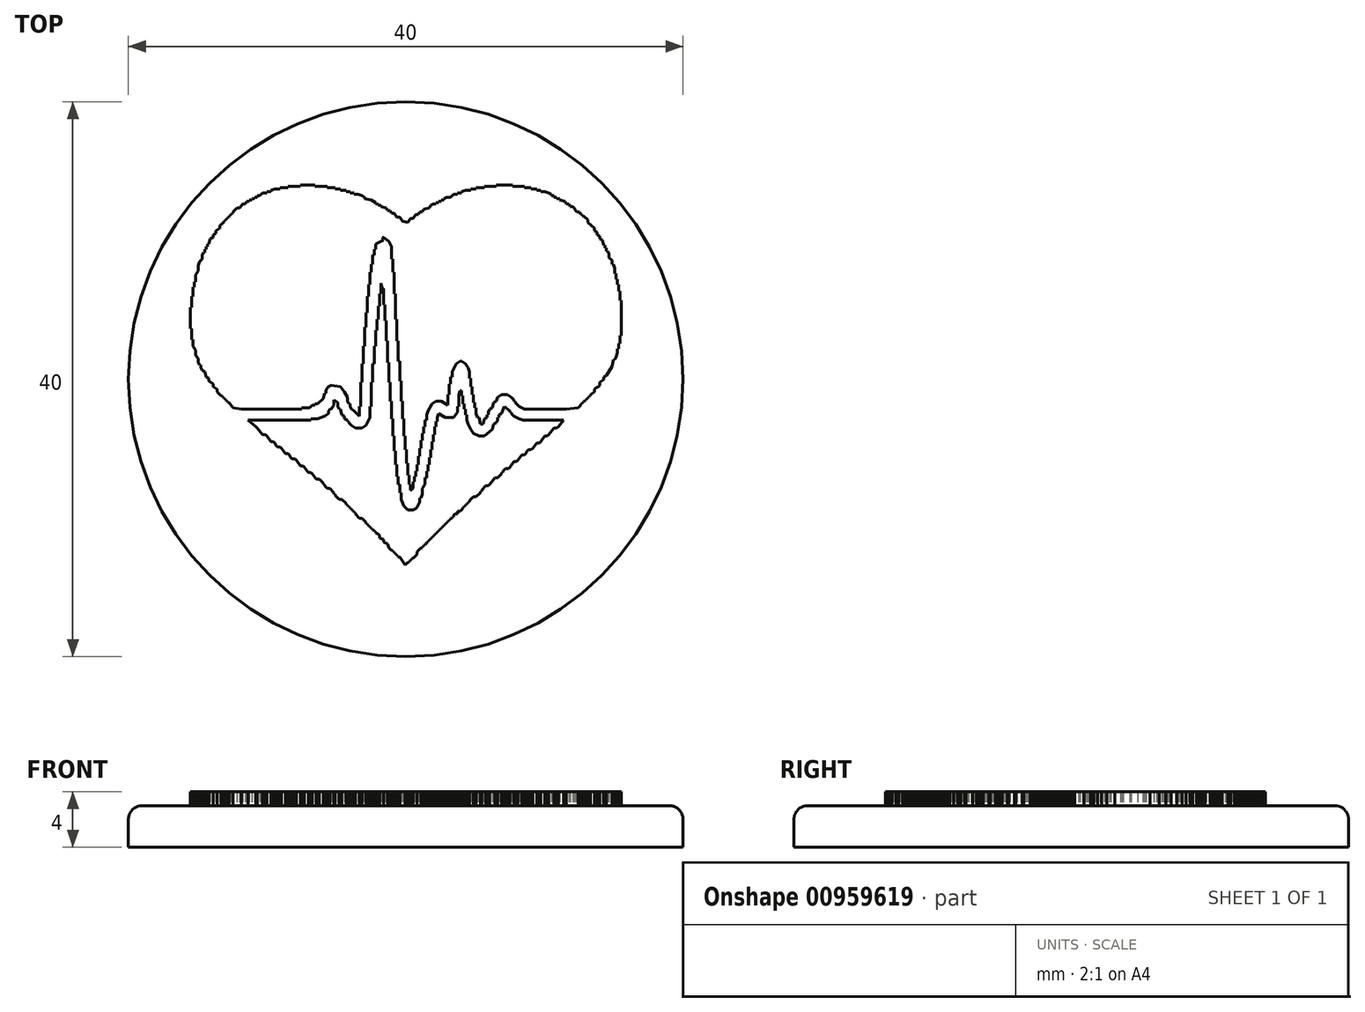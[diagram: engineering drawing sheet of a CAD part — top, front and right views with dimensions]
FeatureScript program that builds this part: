
annotation { "Feature Type Name" : "Feature", "Feature Type Description" : "" }
export const myFeature = defineFeature(function(context is Context, id is Id, definition is map)
    precondition{}
    {
        {
            var Q0;
            Q0=qCreatedBy(makeId("Front.planeOp"),FACE);
            var sketch = newSketch(context, id + "F0", { "sketchPlane" : qUnion([Q0])});
            skLineSegment(sketch, "E0.bottom", {"start": v(-20, 0) * mm, "end": v(0, 0) * mm});
            skLineSegment(sketch, "E0.top", {"start": v(-20, 3) * mm, "end": v(0, 3) * mm});
            skLineSegment(sketch, "E0.left", {"start": v(-20, 0) * mm, "end": v(-20, 3) * mm});
            skLineSegment(sketch, "E0.right", {"start": v(0, 0) * mm, "end": v(0, 3) * mm});
            skSolve(sketch);
        }
        {
            var Q0;
            Q0=qSketchRegion(id+"F0",true);
            var Q1;
            Q1=sQuery(id+"F0.wireOp",EDGE,"E0.right");
            revolve(context, id + "F1", {"surfaceOperationType" : NewSurfaceOperationType.NEW, "entities" : qUnion([Q0]), "axis" : qUnion([Q1]), "revolveType" : RevolveType.FULL});
        }
        {
            var Q0;
            Q0=qCreatedBy(makeId("Top.planeOp"),FACE);
            cPlane(context, id + "F2", {"entities" : qUnion([Q0]), "cplaneType" : CPlaneType.OFFSET, "offset" : 3 * mm, "width" : 150 * mm, "height" : 150 * mm});
        }
        {
            var Q0;
            Q0=qCreatedBy(id+"F2.planeOp",FACE);
            var sketch = newSketch(context, id + "F3", { "sketchPlane" : qUnion([Q0])});
            skLineSegment(sketch, "E1", {"start": v(-7.6, 14) * mm, "end": v(-7.6, 13.9) * mm});
            skLineSegment(sketch, "E2", {"start": v(-7.6, 13.9) * mm, "end": v(-7.9, 13.9) * mm});
            skLineSegment(sketch, "E3", {"start": v(-7.9, 13.9) * mm, "end": v(-8.18, 13.9) * mm});
            skLineSegment(sketch, "E4", {"start": v(-8.18, 13.9) * mm, "end": v(-8.47, 13.9) * mm});
            skLineSegment(sketch, "E5", {"start": v(-8.47, 13.9) * mm, "end": v(-8.47, 13.8) * mm});
            skLineSegment(sketch, "E6", {"start": v(-8.47, 13.8) * mm, "end": v(-9.06, 13.8) * mm});
            skLineSegment(sketch, "E7", {"start": v(-9.06, 13.8) * mm, "end": v(-9.06, 13.7) * mm});
            skLineSegment(sketch, "E8", {"start": v(-9.06, 13.7) * mm, "end": v(-9.44, 13.7) * mm});
            skLineSegment(sketch, "E9", {"start": v(-9.44, 13.7) * mm, "end": v(-9.73, 13.61) * mm});
            skLineSegment(sketch, "E10", {"start": v(-9.73, 13.61) * mm, "end": v(-9.73, 13.52) * mm});
            skLineSegment(sketch, "E11", {"start": v(-9.73, 13.52) * mm, "end": v(-10.02, 13.52) * mm});
            skLineSegment(sketch, "E12", {"start": v(-10.02, 13.52) * mm, "end": v(-10.02, 13.42) * mm});
            skLineSegment(sketch, "E13", {"start": v(-10.02, 13.42) * mm, "end": v(-10.31, 13.42) * mm});
            skLineSegment(sketch, "E14", {"start": v(-10.31, 13.42) * mm, "end": v(-10.5, 13.23) * mm});
            skLineSegment(sketch, "E15", {"start": v(-10.5, 13.23) * mm, "end": v(-10.7, 13.23) * mm});
            skLineSegment(sketch, "E16", {"start": v(-10.7, 13.23) * mm, "end": v(-10.7, 13.13) * mm});
            skLineSegment(sketch, "E17", {"start": v(-10.7, 13.13) * mm, "end": v(-10.9, 13.13) * mm});
            skLineSegment(sketch, "E18", {"start": v(-10.9, 13.13) * mm, "end": v(-10.9, 13.03) * mm});
            skLineSegment(sketch, "E19", {"start": v(-10.9, 13.03) * mm, "end": v(-11.09, 13.03) * mm});
            skLineSegment(sketch, "E20", {"start": v(-11.09, 13.03) * mm, "end": v(-11.09, 12.93) * mm});
            skLineSegment(sketch, "E21", {"start": v(-11.09, 12.93) * mm, "end": v(-11.28, 12.93) * mm});
            skLineSegment(sketch, "E22", {"start": v(-11.28, 12.93) * mm, "end": v(-11.28, 12.84) * mm});
            skLineSegment(sketch, "E23", {"start": v(-11.28, 12.84) * mm, "end": v(-11.48, 12.84) * mm});
            skLineSegment(sketch, "E24", {"start": v(-11.48, 12.84) * mm, "end": v(-11.57, 12.64) * mm});
            skLineSegment(sketch, "E25", {"start": v(-11.57, 12.64) * mm, "end": v(-11.77, 12.64) * mm});
            skLineSegment(sketch, "E26", {"start": v(-11.77, 12.64) * mm, "end": v(-11.96, 12.35) * mm});
            skLineSegment(sketch, "E27", {"start": v(-11.96, 12.35) * mm, "end": v(-12.15, 12.35) * mm});
            skLineSegment(sketch, "E28", {"start": v(-12.15, 12.35) * mm, "end": v(-12.25, 12.26) * mm});
            skLineSegment(sketch, "E29", {"start": v(-12.25, 12.26) * mm, "end": v(-12.45, 12.06) * mm});
            skLineSegment(sketch, "E30", {"start": v(-12.45, 12.06) * mm, "end": v(-12.45, 11.97) * mm});
            skLineSegment(sketch, "E31", {"start": v(-12.45, 11.97) * mm, "end": v(-12.54, 11.97) * mm});
            skLineSegment(sketch, "E32", {"start": v(-12.54, 11.97) * mm, "end": v(-12.54, 11.87) * mm});
            skLineSegment(sketch, "E33", {"start": v(-12.54, 11.87) * mm, "end": v(-12.64, 11.87) * mm});
            skLineSegment(sketch, "E34", {"start": v(-12.64, 11.87) * mm, "end": v(-12.64, 11.77) * mm});
            skLineSegment(sketch, "E35", {"start": v(-12.64, 11.77) * mm, "end": v(-12.74, 11.77) * mm});
            skLineSegment(sketch, "E36", {"start": v(-12.74, 11.77) * mm, "end": v(-12.74, 11.68) * mm});
            skLineSegment(sketch, "E37", {"start": v(-12.74, 11.68) * mm, "end": v(-12.83, 11.68) * mm});
            skLineSegment(sketch, "E38", {"start": v(-12.83, 11.68) * mm, "end": v(-12.83, 11.58) * mm});
            skLineSegment(sketch, "E39", {"start": v(-12.83, 11.58) * mm, "end": v(-12.93, 11.58) * mm});
            skLineSegment(sketch, "E40", {"start": v(-12.93, 11.58) * mm, "end": v(-12.93, 11.48) * mm});
            skLineSegment(sketch, "E41", {"start": v(-12.93, 11.48) * mm, "end": v(-13.03, 11.48) * mm});
            skLineSegment(sketch, "E42", {"start": v(-13.03, 11.48) * mm, "end": v(-13.03, 11.38) * mm});
            skLineSegment(sketch, "E43", {"start": v(-13.03, 11.38) * mm, "end": v(-13.12, 11.38) * mm});
            skLineSegment(sketch, "E44", {"start": v(-13.12, 11.38) * mm, "end": v(-13.12, 11.29) * mm});
            skLineSegment(sketch, "E45", {"start": v(-13.12, 11.29) * mm, "end": v(-13.41, 11.1) * mm});
            skLineSegment(sketch, "E46", {"start": v(-13.41, 11.1) * mm, "end": v(-13.41, 10.9) * mm});
            skLineSegment(sketch, "E47", {"start": v(-13.41, 10.9) * mm, "end": v(-13.7, 10.7) * mm});
            skLineSegment(sketch, "E48", {"start": v(-13.7, 10.7) * mm, "end": v(-13.7, 10.51) * mm});
            skLineSegment(sketch, "E49", {"start": v(-13.7, 10.51) * mm, "end": v(-13.9, 10.42) * mm});
            skLineSegment(sketch, "E50", {"start": v(-13.9, 10.42) * mm, "end": v(-13.9, 10.22) * mm});
            skLineSegment(sketch, "E51", {"start": v(-13.9, 10.22) * mm, "end": v(-14.1, 10.13) * mm});
            skLineSegment(sketch, "E52", {"start": v(-14.1, 10.13) * mm, "end": v(-14.19, 9.74) * mm});
            skLineSegment(sketch, "E53", {"start": v(-14.19, 9.74) * mm, "end": v(-14.29, 9.74) * mm});
            skLineSegment(sketch, "E54", {"start": v(-14.29, 9.74) * mm, "end": v(-14.29, 9.54) * mm});
            skLineSegment(sketch, "E55", {"start": v(-14.29, 9.54) * mm, "end": v(-14.38, 9.54) * mm});
            skLineSegment(sketch, "E56", {"start": v(-14.38, 9.54) * mm, "end": v(-14.38, 9.35) * mm});
            skLineSegment(sketch, "E57", {"start": v(-14.38, 9.35) * mm, "end": v(-14.48, 9.35) * mm});
            skLineSegment(sketch, "E58", {"start": v(-14.48, 9.35) * mm, "end": v(-14.48, 9.16) * mm});
            skLineSegment(sketch, "E59", {"start": v(-14.48, 9.16) * mm, "end": v(-14.58, 9.16) * mm});
            skLineSegment(sketch, "E60", {"start": v(-14.58, 9.16) * mm, "end": v(-14.67, 8.96) * mm});
            skLineSegment(sketch, "E61", {"start": v(-14.67, 8.96) * mm, "end": v(-14.67, 8.67) * mm});
            skLineSegment(sketch, "E62", {"start": v(-14.67, 8.67) * mm, "end": v(-14.87, 8.48) * mm});
            skLineSegment(sketch, "E63", {"start": v(-14.87, 8.48) * mm, "end": v(-14.96, 8.19) * mm});
            skLineSegment(sketch, "E64", {"start": v(-14.96, 8.19) * mm, "end": v(-14.96, 7.8) * mm});
            skLineSegment(sketch, "E65", {"start": v(-14.96, 7.8) * mm, "end": v(-15.16, 7.51) * mm});
            skLineSegment(sketch, "E66", {"start": v(-15.16, 7.51) * mm, "end": v(-15.16, 7.03) * mm});
            skLineSegment(sketch, "E67", {"start": v(-15.16, 7.03) * mm, "end": v(-15.25, 7.03) * mm});
            skLineSegment(sketch, "E68", {"start": v(-15.25, 7.03) * mm, "end": v(-15.25, 6.64) * mm});
            skLineSegment(sketch, "E69", {"start": v(-15.25, 6.64) * mm, "end": v(-15.35, 6.64) * mm});
            skLineSegment(sketch, "E70", {"start": v(-15.35, 6.64) * mm, "end": v(-15.35, 5.96) * mm});
            skLineSegment(sketch, "E71", {"start": v(-15.35, 5.96) * mm, "end": v(-15.45, 5.96) * mm});
            skLineSegment(sketch, "E72", {"start": v(-15.45, 5.96) * mm, "end": v(-15.45, 5.19) * mm});
            skLineSegment(sketch, "E73", {"start": v(-15.45, 5.19) * mm, "end": v(-15.54, 5.19) * mm});
            skLineSegment(sketch, "E74", {"start": v(-15.54, 5.19) * mm, "end": v(-15.54, 4.9) * mm});
            skLineSegment(sketch, "E75", {"start": v(-15.54, 4.9) * mm, "end": v(-15.54, 4.5) * mm});
            skLineSegment(sketch, "E76", {"start": v(-15.54, 4.5) * mm, "end": v(-15.54, 4.41) * mm});
            skLineSegment(sketch, "E77", {"start": v(-15.54, 4.41) * mm, "end": v(-15.54, 4.31) * mm});
            skLineSegment(sketch, "E78", {"start": v(-15.54, 4.31) * mm, "end": v(-15.54, 4.22) * mm});
            skLineSegment(sketch, "E79", {"start": v(-15.54, 4.22) * mm, "end": v(-15.54, 3.64) * mm});
            skLineSegment(sketch, "E80", {"start": v(-15.54, 3.64) * mm, "end": v(-15.45, 3.64) * mm});
            skLineSegment(sketch, "E81", {"start": v(-15.45, 3.64) * mm, "end": v(-15.45, 2.86) * mm});
            skLineSegment(sketch, "E82", {"start": v(-15.45, 2.86) * mm, "end": v(-15.35, 2.86) * mm});
            skLineSegment(sketch, "E83", {"start": v(-15.35, 2.86) * mm, "end": v(-15.35, 2.38) * mm});
            skLineSegment(sketch, "E84", {"start": v(-15.35, 2.38) * mm, "end": v(-15.16, 2.09) * mm});
            skLineSegment(sketch, "E85", {"start": v(-15.16, 2.09) * mm, "end": v(-15.16, 1.7) * mm});
            skLineSegment(sketch, "E86", {"start": v(-15.16, 1.7) * mm, "end": v(-14.96, 1.5) * mm});
            skLineSegment(sketch, "E87", {"start": v(-14.96, 1.5) * mm, "end": v(-14.96, 1.22) * mm});
            skLineSegment(sketch, "E88", {"start": v(-14.96, 1.22) * mm, "end": v(-14.87, 1.02) * mm});
            skLineSegment(sketch, "E89", {"start": v(-14.87, 1.02) * mm, "end": v(-14.77, 1.02) * mm});
            skLineSegment(sketch, "E90", {"start": v(-14.77, 1.02) * mm, "end": v(-14.77, 0.83) * mm});
            skLineSegment(sketch, "E91", {"start": v(-14.77, 0.83) * mm, "end": v(-14.67, 0.63) * mm});
            skLineSegment(sketch, "E92", {"start": v(-14.67, 0.63) * mm, "end": v(-14.48, 0.54) * mm});
            skLineSegment(sketch, "E93", {"start": v(-14.48, 0.54) * mm, "end": v(-14.38, 0.15) * mm});
            skLineSegment(sketch, "E94", {"start": v(-14.38, 0.15) * mm, "end": v(-14.19, 0.05) * mm});
            skLineSegment(sketch, "E95", {"start": v(-14.19, 0.05) * mm, "end": v(-14.19, -0.14) * mm});
            skLineSegment(sketch, "E96", {"start": v(-14.19, -0.14) * mm, "end": v(-13.9, -0.33) * mm});
            skLineSegment(sketch, "E97", {"start": v(-13.9, -0.33) * mm, "end": v(-13.9, -0.53) * mm});
            skLineSegment(sketch, "E98", {"start": v(-13.9, -0.53) * mm, "end": v(-13.6, -0.72) * mm});
            skLineSegment(sketch, "E99", {"start": v(-13.6, -0.72) * mm, "end": v(-13.6, -0.92) * mm});
            skLineSegment(sketch, "E100", {"start": v(-13.6, -0.92) * mm, "end": v(-13.51, -1.01) * mm});
            skLineSegment(sketch, "E101", {"start": v(-13.51, -1.01) * mm, "end": v(-13.32, -1.2) * mm});
            skLineSegment(sketch, "E102", {"start": v(-13.32, -1.2) * mm, "end": v(-13.22, -1.2) * mm});
            skLineSegment(sketch, "E103", {"start": v(-13.22, -1.2) * mm, "end": v(-13.22, -1.3) * mm});
            skLineSegment(sketch, "E104", {"start": v(-13.22, -1.3) * mm, "end": v(-13.12, -1.3) * mm});
            skLineSegment(sketch, "E105", {"start": v(-13.12, -1.3) * mm, "end": v(-13.12, -1.4) * mm});
            skLineSegment(sketch, "E106", {"start": v(-13.12, -1.4) * mm, "end": v(-13.03, -1.4) * mm});
            skLineSegment(sketch, "E107", {"start": v(-13.03, -1.4) * mm, "end": v(-13.03, -1.5) * mm});
            skLineSegment(sketch, "E108", {"start": v(-13.03, -1.5) * mm, "end": v(-12.93, -1.5) * mm});
            skLineSegment(sketch, "E109", {"start": v(-12.93, -1.5) * mm, "end": v(-12.93, -1.6) * mm});
            skLineSegment(sketch, "E110", {"start": v(-12.93, -1.6) * mm, "end": v(-12.83, -1.6) * mm});
            skLineSegment(sketch, "E111", {"start": v(-12.83, -1.6) * mm, "end": v(-12.83, -1.7) * mm});
            skLineSegment(sketch, "E112", {"start": v(-12.83, -1.7) * mm, "end": v(-12.74, -1.7) * mm});
            skLineSegment(sketch, "E113", {"start": v(-12.74, -1.7) * mm, "end": v(-12.45, -2.08) * mm});
            skLineSegment(sketch, "E114", {"start": v(-12.45, -2.08) * mm, "end": v(-12.83, -2.08) * mm});
            skLineSegment(sketch, "E115", {"start": v(-12.83, -2.08) * mm, "end": v(-12.93, -2.08) * mm});
            skLineSegment(sketch, "E116", {"start": v(-12.93, -2.08) * mm, "end": v(-13.03, -2.08) * mm});
            skLineSegment(sketch, "E117", {"start": v(-13.03, -2.08) * mm, "end": v(-13.12, -2.08) * mm});
            skLineSegment(sketch, "E118", {"start": v(-13.12, -2.08) * mm, "end": v(-13.22, -2.08) * mm});
            skLineSegment(sketch, "E119", {"start": v(-13.22, -2.08) * mm, "end": v(-13.32, -2.08) * mm});
            skLineSegment(sketch, "E120", {"start": v(-13.32, -2.08) * mm, "end": v(-13.41, -2.08) * mm});
            skLineSegment(sketch, "E121", {"start": v(-13.41, -2.08) * mm, "end": v(-13.51, -2.08) * mm});
            skLineSegment(sketch, "E122", {"start": v(-13.51, -2.08) * mm, "end": v(-13.6, -2.08) * mm});
            skLineSegment(sketch, "E123", {"start": v(-13.6, -2.08) * mm, "end": v(-13.7, -2.08) * mm});
            skLineSegment(sketch, "E124", {"start": v(-13.7, -2.08) * mm, "end": v(-13.8, -2.08) * mm});
            skLineSegment(sketch, "E125", {"start": v(-13.8, -2.08) * mm, "end": v(-13.9, -2.08) * mm});
            skLineSegment(sketch, "E126", {"start": v(-13.9, -2.08) * mm, "end": v(-14, -2.08) * mm});
            skLineSegment(sketch, "E127", {"start": v(-14, -2.08) * mm, "end": v(-14.1, -2.08) * mm});
            skLineSegment(sketch, "E128", {"start": v(-14.1, -2.08) * mm, "end": v(-14.19, -2.08) * mm});
            skLineSegment(sketch, "E129", {"start": v(-14.19, -2.08) * mm, "end": v(-14.29, -2.08) * mm});
            skLineSegment(sketch, "E130", {"start": v(-14.29, -2.08) * mm, "end": v(-14.38, -2.08) * mm});
            skLineSegment(sketch, "E131", {"start": v(-14.38, -2.08) * mm, "end": v(-14.48, -2.08) * mm});
            skLineSegment(sketch, "E132", {"start": v(-14.48, -2.08) * mm, "end": v(-14.58, -2.08) * mm});
            skLineSegment(sketch, "E133", {"start": v(-14.58, -2.08) * mm, "end": v(-14.67, -2.08) * mm});
            skLineSegment(sketch, "E134", {"start": v(-14.67, -2.08) * mm, "end": v(-14.77, -2.08) * mm});
            skLineSegment(sketch, "E135", {"start": v(-14.77, -2.08) * mm, "end": v(-14.87, -2.08) * mm});
            skLineSegment(sketch, "E136", {"start": v(-14.87, -2.08) * mm, "end": v(-14.96, -2.08) * mm});
            skLineSegment(sketch, "E137", {"start": v(-14.96, -2.08) * mm, "end": v(-15.06, -2.08) * mm});
            skLineSegment(sketch, "E138", {"start": v(-15.06, -2.08) * mm, "end": v(-15.16, -2.08) * mm});
            skLineSegment(sketch, "E139", {"start": v(-15.16, -2.08) * mm, "end": v(-15.25, -2.08) * mm});
            skLineSegment(sketch, "E140", {"start": v(-15.25, -2.08) * mm, "end": v(-15.35, -2.08) * mm});
            skLineSegment(sketch, "E141", {"start": v(-15.35, -2.08) * mm, "end": v(-15.45, -2.08) * mm});
            skLineSegment(sketch, "E142", {"start": v(-15.45, -2.08) * mm, "end": v(-15.54, -2.08) * mm});
            skLineSegment(sketch, "E143", {"start": v(-15.54, -2.08) * mm, "end": v(-15.64, -2.08) * mm});
            skLineSegment(sketch, "E144", {"start": v(-15.64, -2.08) * mm, "end": v(-15.74, -2.08) * mm});
            skLineSegment(sketch, "E145", {"start": v(-15.74, -2.08) * mm, "end": v(-15.84, -2.08) * mm});
            skLineSegment(sketch, "E146", {"start": v(-15.84, -2.08) * mm, "end": v(-15.93, -2.08) * mm});
            skLineSegment(sketch, "E147", {"start": v(-15.93, -2.08) * mm, "end": v(-16.03, -2.08) * mm});
            skLineSegment(sketch, "E148", {"start": v(-16.03, -2.08) * mm, "end": v(-16.13, -2.08) * mm});
            skLineSegment(sketch, "E149", {"start": v(-16.13, -2.08) * mm, "end": v(-16.22, -2.08) * mm});
            skLineSegment(sketch, "E150", {"start": v(-16.22, -2.08) * mm, "end": v(-16.32, -2.08) * mm});
            skLineSegment(sketch, "E151", {"start": v(-16.32, -2.08) * mm, "end": v(-16.42, -2.08) * mm});
            skLineSegment(sketch, "E152", {"start": v(-16.42, -2.08) * mm, "end": v(-16.51, -2.08) * mm});
            skLineSegment(sketch, "E153", {"start": v(-16.51, -2.08) * mm, "end": v(-16.61, -2.08) * mm});
            skLineSegment(sketch, "E154", {"start": v(-16.61, -2.08) * mm, "end": v(-16.7, -2.08) * mm});
            skLineSegment(sketch, "E155", {"start": v(-16.7, -2.08) * mm, "end": v(-16.8, -2.08) * mm});
            skLineSegment(sketch, "E156", {"start": v(-16.8, -2.08) * mm, "end": v(-16.9, -2.08) * mm});
            skLineSegment(sketch, "E157", {"start": v(-16.9, -2.08) * mm, "end": v(-17, -2.08) * mm});
            skLineSegment(sketch, "E158", {"start": v(-17, -2.08) * mm, "end": v(-17.1, -2.08) * mm});
            skLineSegment(sketch, "E159", {"start": v(-17.1, -2.08) * mm, "end": v(-17.2, -2.08) * mm});
            skLineSegment(sketch, "E160", {"start": v(-17.2, -2.08) * mm, "end": v(-17.29, -2.08) * mm});
            skLineSegment(sketch, "E161", {"start": v(-17.29, -2.08) * mm, "end": v(-17.38, -2.08) * mm});
            skLineSegment(sketch, "E162", {"start": v(-17.38, -2.08) * mm, "end": v(-17.48, -2.08) * mm});
            skLineSegment(sketch, "E163", {"start": v(-17.48, -2.08) * mm, "end": v(-17.58, -2.08) * mm});
            skLineSegment(sketch, "E164", {"start": v(-17.58, -2.08) * mm, "end": v(-17.68, -2.08) * mm});
            skLineSegment(sketch, "E165", {"start": v(-17.68, -2.08) * mm, "end": v(-17.77, -2.08) * mm});
            skLineSegment(sketch, "E166", {"start": v(-17.77, -2.08) * mm, "end": v(-17.87, -2.08) * mm});
            skLineSegment(sketch, "E167", {"start": v(-17.87, -2.08) * mm, "end": v(-17.97, -2.08) * mm});
            skLineSegment(sketch, "E168", {"start": v(-17.97, -2.08) * mm, "end": v(-18.06, -2.08) * mm});
            skLineSegment(sketch, "E169", {"start": v(-18.06, -2.08) * mm, "end": v(-18.16, -2.08) * mm});
            skLineSegment(sketch, "E170", {"start": v(-18.16, -2.08) * mm, "end": v(-18.26, -2.08) * mm});
            skLineSegment(sketch, "E171", {"start": v(-18.26, -2.08) * mm, "end": v(-18.35, -2.08) * mm});
            skLineSegment(sketch, "E172", {"start": v(-18.35, -2.08) * mm, "end": v(-18.45, -2.08) * mm});
            skLineSegment(sketch, "E173", {"start": v(-18.45, -2.08) * mm, "end": v(-18.55, -2.08) * mm});
            skLineSegment(sketch, "E174", {"start": v(-18.55, -2.08) * mm, "end": v(-18.64, -2.08) * mm});
            skLineSegment(sketch, "E175", {"start": v(-18.64, -2.08) * mm, "end": v(-18.74, -2.08) * mm});
            skLineSegment(sketch, "E176", {"start": v(-18.74, -2.08) * mm, "end": v(-18.84, -2.08) * mm});
            skLineSegment(sketch, "E177", {"start": v(-18.84, -2.08) * mm, "end": v(-18.93, -2.08) * mm});
            skLineSegment(sketch, "E178", {"start": v(-18.93, -2.08) * mm, "end": v(-19.03, -2.08) * mm});
            skLineSegment(sketch, "E179", {"start": v(-19.03, -2.08) * mm, "end": v(-19.13, -2.08) * mm});
            skLineSegment(sketch, "E180", {"start": v(-19.13, -2.08) * mm, "end": v(-19.23, -2.08) * mm});
            skLineSegment(sketch, "E181", {"start": v(-19.23, -2.08) * mm, "end": v(-19.32, -2.08) * mm});
            skLineSegment(sketch, "E182", {"start": v(-19.32, -2.08) * mm, "end": v(-19.7, -2.08) * mm});
            skLineSegment(sketch, "E183", {"start": v(-19.7, -2.95) * mm, "end": v(-19.32, -2.95) * mm});
            skLineSegment(sketch, "E184", {"start": v(-19.32, -2.95) * mm, "end": v(-19.23, -2.95) * mm});
            skLineSegment(sketch, "E185", {"start": v(-19.23, -2.95) * mm, "end": v(-19.13, -2.95) * mm});
            skLineSegment(sketch, "E186", {"start": v(-19.13, -2.95) * mm, "end": v(-19.03, -2.95) * mm});
            skLineSegment(sketch, "E187", {"start": v(-19.03, -2.95) * mm, "end": v(-18.93, -2.95) * mm});
            skLineSegment(sketch, "E188", {"start": v(-18.93, -2.95) * mm, "end": v(-18.84, -2.95) * mm});
            skLineSegment(sketch, "E189", {"start": v(-18.84, -2.95) * mm, "end": v(-18.74, -2.95) * mm});
            skLineSegment(sketch, "E190", {"start": v(-18.74, -2.95) * mm, "end": v(-18.64, -2.95) * mm});
            skLineSegment(sketch, "E191", {"start": v(-18.64, -2.95) * mm, "end": v(-18.55, -2.95) * mm});
            skLineSegment(sketch, "E192", {"start": v(-18.55, -2.95) * mm, "end": v(-18.45, -2.95) * mm});
            skLineSegment(sketch, "E193", {"start": v(-18.45, -2.95) * mm, "end": v(-18.35, -2.95) * mm});
            skLineSegment(sketch, "E194", {"start": v(-18.35, -2.95) * mm, "end": v(-18.26, -2.95) * mm});
            skLineSegment(sketch, "E195", {"start": v(-18.26, -2.95) * mm, "end": v(-18.16, -2.95) * mm});
            skLineSegment(sketch, "E196", {"start": v(-18.16, -2.95) * mm, "end": v(-18.06, -2.95) * mm});
            skLineSegment(sketch, "E197", {"start": v(-18.06, -2.95) * mm, "end": v(-17.97, -2.95) * mm});
            skLineSegment(sketch, "E198", {"start": v(-17.97, -2.95) * mm, "end": v(-17.87, -2.95) * mm});
            skLineSegment(sketch, "E199", {"start": v(-17.87, -2.95) * mm, "end": v(-17.77, -2.95) * mm});
            skLineSegment(sketch, "E200", {"start": v(-17.77, -2.95) * mm, "end": v(-17.68, -2.95) * mm});
            skLineSegment(sketch, "E201", {"start": v(-17.68, -2.95) * mm, "end": v(-17.58, -2.95) * mm});
            skLineSegment(sketch, "E202", {"start": v(-17.58, -2.95) * mm, "end": v(-17.48, -2.95) * mm});
            skLineSegment(sketch, "E203", {"start": v(-17.48, -2.95) * mm, "end": v(-17.38, -2.95) * mm});
            skLineSegment(sketch, "E204", {"start": v(-17.38, -2.95) * mm, "end": v(-17.29, -2.95) * mm});
            skLineSegment(sketch, "E205", {"start": v(-17.29, -2.95) * mm, "end": v(-17.2, -2.95) * mm});
            skLineSegment(sketch, "E206", {"start": v(-17.2, -2.95) * mm, "end": v(-17.1, -2.95) * mm});
            skLineSegment(sketch, "E207", {"start": v(-17.1, -2.95) * mm, "end": v(-17, -2.95) * mm});
            skLineSegment(sketch, "E208", {"start": v(-17, -2.95) * mm, "end": v(-16.9, -2.95) * mm});
            skLineSegment(sketch, "E209", {"start": v(-16.9, -2.95) * mm, "end": v(-16.8, -2.95) * mm});
            skLineSegment(sketch, "E210", {"start": v(-16.8, -2.95) * mm, "end": v(-16.7, -2.95) * mm});
            skLineSegment(sketch, "E211", {"start": v(-16.7, -2.95) * mm, "end": v(-16.61, -2.95) * mm});
            skLineSegment(sketch, "E212", {"start": v(-16.61, -2.95) * mm, "end": v(-16.51, -2.95) * mm});
            skLineSegment(sketch, "E213", {"start": v(-16.51, -2.95) * mm, "end": v(-16.42, -2.95) * mm});
            skLineSegment(sketch, "E214", {"start": v(-16.42, -2.95) * mm, "end": v(-16.32, -2.95) * mm});
            skLineSegment(sketch, "E215", {"start": v(-16.32, -2.95) * mm, "end": v(-16.22, -2.95) * mm});
            skLineSegment(sketch, "E216", {"start": v(-16.22, -2.95) * mm, "end": v(-16.13, -2.95) * mm});
            skLineSegment(sketch, "E217", {"start": v(-16.13, -2.95) * mm, "end": v(-16.03, -2.95) * mm});
            skLineSegment(sketch, "E218", {"start": v(-16.03, -2.95) * mm, "end": v(-15.93, -2.95) * mm});
            skLineSegment(sketch, "E219", {"start": v(-15.93, -2.95) * mm, "end": v(-15.84, -2.95) * mm});
            skLineSegment(sketch, "E220", {"start": v(-15.84, -2.95) * mm, "end": v(-15.74, -2.95) * mm});
            skLineSegment(sketch, "E221", {"start": v(-15.74, -2.95) * mm, "end": v(-15.64, -2.95) * mm});
            skLineSegment(sketch, "E222", {"start": v(-15.64, -2.95) * mm, "end": v(-15.54, -2.95) * mm});
            skLineSegment(sketch, "E223", {"start": v(-15.54, -2.95) * mm, "end": v(-15.45, -2.95) * mm});
            skLineSegment(sketch, "E224", {"start": v(-15.45, -2.95) * mm, "end": v(-15.35, -2.95) * mm});
            skLineSegment(sketch, "E225", {"start": v(-15.35, -2.95) * mm, "end": v(-15.25, -2.95) * mm});
            skLineSegment(sketch, "E226", {"start": v(-15.25, -2.95) * mm, "end": v(-15.16, -2.95) * mm});
            skLineSegment(sketch, "E227", {"start": v(-15.16, -2.95) * mm, "end": v(-15.06, -2.95) * mm});
            skLineSegment(sketch, "E228", {"start": v(-15.06, -2.95) * mm, "end": v(-14.96, -2.95) * mm});
            skLineSegment(sketch, "E229", {"start": v(-14.96, -2.95) * mm, "end": v(-14.87, -2.95) * mm});
            skLineSegment(sketch, "E230", {"start": v(-14.87, -2.95) * mm, "end": v(-14.77, -2.95) * mm});
            skLineSegment(sketch, "E231", {"start": v(-14.77, -2.95) * mm, "end": v(-14.67, -2.95) * mm});
            skLineSegment(sketch, "E232", {"start": v(-14.67, -2.95) * mm, "end": v(-14.58, -2.95) * mm});
            skLineSegment(sketch, "E233", {"start": v(-14.58, -2.95) * mm, "end": v(-14.48, -2.95) * mm});
            skLineSegment(sketch, "E234", {"start": v(-14.48, -2.95) * mm, "end": v(-14.38, -2.95) * mm});
            skLineSegment(sketch, "E235", {"start": v(-14.38, -2.95) * mm, "end": v(-14.29, -2.95) * mm});
            skLineSegment(sketch, "E236", {"start": v(-14.29, -2.95) * mm, "end": v(-14.19, -2.95) * mm});
            skLineSegment(sketch, "E237", {"start": v(-14.19, -2.95) * mm, "end": v(-14.1, -2.95) * mm});
            skLineSegment(sketch, "E238", {"start": v(-14.1, -2.95) * mm, "end": v(-14, -2.95) * mm});
            skLineSegment(sketch, "E239", {"start": v(-14, -2.95) * mm, "end": v(-13.9, -2.95) * mm});
            skLineSegment(sketch, "E240", {"start": v(-13.9, -2.95) * mm, "end": v(-13.8, -2.95) * mm});
            skLineSegment(sketch, "E241", {"start": v(-13.8, -2.95) * mm, "end": v(-13.7, -2.95) * mm});
            skLineSegment(sketch, "E242", {"start": v(-13.7, -2.95) * mm, "end": v(-13.6, -2.95) * mm});
            skLineSegment(sketch, "E243", {"start": v(-13.6, -2.95) * mm, "end": v(-13.51, -2.95) * mm});
            skLineSegment(sketch, "E244", {"start": v(-13.51, -2.95) * mm, "end": v(-13.41, -2.95) * mm});
            skLineSegment(sketch, "E245", {"start": v(-13.41, -2.95) * mm, "end": v(-13.32, -2.95) * mm});
            skLineSegment(sketch, "E246", {"start": v(-13.32, -2.95) * mm, "end": v(-13.22, -2.95) * mm});
            skLineSegment(sketch, "E247", {"start": v(-13.22, -2.95) * mm, "end": v(-13.12, -2.95) * mm});
            skLineSegment(sketch, "E248", {"start": v(-13.12, -2.95) * mm, "end": v(-13.03, -2.95) * mm});
            skLineSegment(sketch, "E249", {"start": v(-13.03, -2.95) * mm, "end": v(-12.93, -2.95) * mm});
            skLineSegment(sketch, "E250", {"start": v(-12.93, -2.95) * mm, "end": v(-12.83, -2.95) * mm});
            skLineSegment(sketch, "E251", {"start": v(-12.83, -2.95) * mm, "end": v(-12.74, -2.95) * mm});
            skLineSegment(sketch, "E252", {"start": v(-12.74, -2.95) * mm, "end": v(-12.64, -2.95) * mm});
            skLineSegment(sketch, "E253", {"start": v(-12.64, -2.95) * mm, "end": v(-12.54, -2.95) * mm});
            skLineSegment(sketch, "E254", {"start": v(-12.54, -2.95) * mm, "end": v(-12.45, -2.95) * mm});
            skLineSegment(sketch, "E255", {"start": v(-12.45, -2.95) * mm, "end": v(-12.35, -2.95) * mm});
            skLineSegment(sketch, "E256", {"start": v(-12.35, -2.95) * mm, "end": v(-12.25, -2.95) * mm});
            skLineSegment(sketch, "E257", {"start": v(-12.25, -2.95) * mm, "end": v(-12.15, -2.95) * mm});
            skLineSegment(sketch, "E258", {"start": v(-12.15, -2.95) * mm, "end": v(-12.06, -2.95) * mm});
            skLineSegment(sketch, "E259", {"start": v(-11.67, -2.66) * mm, "end": v(-11.96, -2.56) * mm});
            skLineSegment(sketch, "E260", {"start": v(-11.96, -2.56) * mm, "end": v(-12.45, -2.08) * mm});
            skLineSegment(sketch, "E261", {"start": v(-12.45, -2.08) * mm, "end": v(-11.86, -2.17) * mm});
            skLineSegment(sketch, "E262", {"start": v(-11.86, -2.17) * mm, "end": v(-11.77, -2.17) * mm});
            skLineSegment(sketch, "E263", {"start": v(-11.77, -2.17) * mm, "end": v(-11.67, -2.17) * mm});
            skLineSegment(sketch, "E264", {"start": v(-11.67, -2.17) * mm, "end": v(-11.57, -2.17) * mm});
            skLineSegment(sketch, "E265", {"start": v(-11.57, -2.17) * mm, "end": v(-11.48, -2.17) * mm});
            skLineSegment(sketch, "E266", {"start": v(-11.48, -2.17) * mm, "end": v(-11.38, -2.17) * mm});
            skLineSegment(sketch, "E267", {"start": v(-11.38, -2.17) * mm, "end": v(-11.28, -2.17) * mm});
            skLineSegment(sketch, "E268", {"start": v(-11.28, -2.17) * mm, "end": v(-11.19, -2.17) * mm});
            skLineSegment(sketch, "E269", {"start": v(-11.19, -2.17) * mm, "end": v(-11.09, -2.17) * mm});
            skLineSegment(sketch, "E270", {"start": v(-11.09, -2.17) * mm, "end": v(-11, -2.17) * mm});
            skLineSegment(sketch, "E271", {"start": v(-11, -2.17) * mm, "end": v(-10.9, -2.17) * mm});
            skLineSegment(sketch, "E272", {"start": v(-10.9, -2.17) * mm, "end": v(-10.8, -2.17) * mm});
            skLineSegment(sketch, "E273", {"start": v(-10.8, -2.17) * mm, "end": v(-10.7, -2.17) * mm});
            skLineSegment(sketch, "E274", {"start": v(-10.7, -2.17) * mm, "end": v(-10.6, -2.17) * mm});
            skLineSegment(sketch, "E275", {"start": v(-10.6, -2.17) * mm, "end": v(-10.5, -2.17) * mm});
            skLineSegment(sketch, "E276", {"start": v(-10.5, -2.17) * mm, "end": v(-10.41, -2.17) * mm});
            skLineSegment(sketch, "E277", {"start": v(-10.41, -2.17) * mm, "end": v(-10.31, -2.17) * mm});
            skLineSegment(sketch, "E278", {"start": v(-10.31, -2.17) * mm, "end": v(-10.22, -2.17) * mm});
            skLineSegment(sketch, "E279", {"start": v(-10.22, -2.17) * mm, "end": v(-10.12, -2.17) * mm});
            skLineSegment(sketch, "E280", {"start": v(-10.12, -2.17) * mm, "end": v(-10.02, -2.17) * mm});
            skLineSegment(sketch, "E281", {"start": v(-10.02, -2.17) * mm, "end": v(-9.93, -2.17) * mm});
            skLineSegment(sketch, "E282", {"start": v(-9.93, -2.17) * mm, "end": v(-9.83, -2.17) * mm});
            skLineSegment(sketch, "E283", {"start": v(-9.83, -2.17) * mm, "end": v(-9.73, -2.17) * mm});
            skLineSegment(sketch, "E284", {"start": v(-9.73, -2.17) * mm, "end": v(-9.64, -2.17) * mm});
            skLineSegment(sketch, "E285", {"start": v(-9.64, -2.17) * mm, "end": v(-9.54, -2.17) * mm});
            skLineSegment(sketch, "E286", {"start": v(-9.54, -2.17) * mm, "end": v(-9.44, -2.17) * mm});
            skLineSegment(sketch, "E287", {"start": v(-9.44, -2.17) * mm, "end": v(-9.35, -2.17) * mm});
            skLineSegment(sketch, "E288", {"start": v(-9.35, -2.17) * mm, "end": v(-9.25, -2.17) * mm});
            skLineSegment(sketch, "E289", {"start": v(-9.25, -2.17) * mm, "end": v(-9.15, -2.17) * mm});
            skLineSegment(sketch, "E290", {"start": v(-9.15, -2.17) * mm, "end": v(-9.06, -2.17) * mm});
            skLineSegment(sketch, "E291", {"start": v(-9.06, -2.17) * mm, "end": v(-8.96, -2.17) * mm});
            skLineSegment(sketch, "E292", {"start": v(-8.96, -2.17) * mm, "end": v(-8.86, -2.17) * mm});
            skLineSegment(sketch, "E293", {"start": v(-8.86, -2.17) * mm, "end": v(-8.77, -2.17) * mm});
            skLineSegment(sketch, "E294", {"start": v(-8.77, -2.17) * mm, "end": v(-8.67, -2.17) * mm});
            skLineSegment(sketch, "E295", {"start": v(-8.67, -2.17) * mm, "end": v(-8.57, -2.17) * mm});
            skLineSegment(sketch, "E296", {"start": v(-8.57, -2.17) * mm, "end": v(-8.47, -2.17) * mm});
            skLineSegment(sketch, "E297", {"start": v(-8.47, -2.17) * mm, "end": v(-8.38, -2.17) * mm});
            skLineSegment(sketch, "E298", {"start": v(-8.38, -2.17) * mm, "end": v(-8.28, -2.17) * mm});
            skLineSegment(sketch, "E299", {"start": v(-8.28, -2.17) * mm, "end": v(-8.18, -2.17) * mm});
            skLineSegment(sketch, "E300", {"start": v(-8.18, -2.17) * mm, "end": v(-8.09, -2.17) * mm});
            skLineSegment(sketch, "E301", {"start": v(-8.09, -2.17) * mm, "end": v(-7.5, -2.17) * mm});
            skLineSegment(sketch, "E302", {"start": v(-7.5, -2.17) * mm, "end": v(-7.5, -2.08) * mm});
            skLineSegment(sketch, "E303", {"start": v(-7.5, -2.08) * mm, "end": v(-6.92, -2.08) * mm});
            skLineSegment(sketch, "E304", {"start": v(-6.92, -2.08) * mm, "end": v(-6.73, -1.88) * mm});
            skLineSegment(sketch, "E305", {"start": v(-6.73, -1.88) * mm, "end": v(-6.54, -1.88) * mm});
            skLineSegment(sketch, "E306", {"start": v(-6.54, -1.88) * mm, "end": v(-6.54, -1.79) * mm});
            skLineSegment(sketch, "E307", {"start": v(-6.54, -1.79) * mm, "end": v(-6.34, -1.79) * mm});
            skLineSegment(sketch, "E308", {"start": v(-6.34, -1.79) * mm, "end": v(-5.96, -1.4) * mm});
            skLineSegment(sketch, "E309", {"start": v(-5.96, -1.4) * mm, "end": v(-5.86, -1.01) * mm});
            skLineSegment(sketch, "E310", {"start": v(-5.86, -1.01) * mm, "end": v(-5.76, -1.01) * mm});
            skLineSegment(sketch, "E311", {"start": v(-5.76, -1.01) * mm, "end": v(-5.76, -0.82) * mm});
            skLineSegment(sketch, "E312", {"start": v(-5.76, -0.82) * mm, "end": v(-5.67, -0.62) * mm});
            skLineSegment(sketch, "E313", {"start": v(-5.67, -0.62) * mm, "end": v(-5.57, -0.53) * mm});
            skLineSegment(sketch, "E314", {"start": v(-5.57, -0.53) * mm, "end": v(-5.38, -0.43) * mm});
            skLineSegment(sketch, "E315", {"start": v(-5.38, -0.43) * mm, "end": v(-4.7, -0.53) * mm});
            skLineSegment(sketch, "E316", {"start": v(-4.7, -0.53) * mm, "end": v(-4.4, -0.92) * mm});
            skLineSegment(sketch, "E317", {"start": v(-4.4, -0.92) * mm, "end": v(-4.21, -1.3) * mm});
            skLineSegment(sketch, "E318", {"start": v(-4.21, -1.3) * mm, "end": v(-4.21, -1.6) * mm});
            skLineSegment(sketch, "E319", {"start": v(-4.21, -1.6) * mm, "end": v(-4.12, -1.79) * mm});
            skLineSegment(sketch, "E320", {"start": v(-4.12, -1.79) * mm, "end": v(-4.02, -1.79) * mm});
            skLineSegment(sketch, "E321", {"start": v(-4.02, -1.79) * mm, "end": v(-4.02, -1.98) * mm});
            skLineSegment(sketch, "E322", {"start": v(-4.02, -1.98) * mm, "end": v(-3.92, -2.17) * mm});
            skLineSegment(sketch, "E323", {"start": v(-3.92, -2.17) * mm, "end": v(-3.73, -2.27) * mm});
            skLineSegment(sketch, "E324", {"start": v(-3.73, -2.27) * mm, "end": v(-3.34, -2.66) * mm});
            skLineSegment(sketch, "E325", {"start": v(-3.34, -2.66) * mm, "end": v(-3.34, -1.98) * mm});
            skLineSegment(sketch, "E326", {"start": v(-3.34, -1.98) * mm, "end": v(-3.24, -1.98) * mm});
            skLineSegment(sketch, "E327", {"start": v(-3.24, -1.98) * mm, "end": v(-3.24, -1.7) * mm});
            skLineSegment(sketch, "E328", {"start": v(-3.24, -1.7) * mm, "end": v(-3.24, -1.3) * mm});
            skLineSegment(sketch, "E329", {"start": v(-3.24, -1.3) * mm, "end": v(-3.24, -1.2) * mm});
            skLineSegment(sketch, "E330", {"start": v(-3.24, -1.2) * mm, "end": v(-3.24, -1.1) * mm});
            skLineSegment(sketch, "E331", {"start": v(-3.24, -1.1) * mm, "end": v(-3.24, -1.01) * mm});
            skLineSegment(sketch, "E332", {"start": v(-3.24, -1.01) * mm, "end": v(-3.24, -0.92) * mm});
            skLineSegment(sketch, "E333", {"start": v(-3.24, -0.92) * mm, "end": v(-3.24, -0.82) * mm});
            skLineSegment(sketch, "E334", {"start": v(-3.24, -0.82) * mm, "end": v(-3.24, -0.72) * mm});
            skLineSegment(sketch, "E335", {"start": v(-3.24, -0.72) * mm, "end": v(-3.24, -0.62) * mm});
            skLineSegment(sketch, "E336", {"start": v(-3.24, -0.62) * mm, "end": v(-3.24, -0.24) * mm});
            skLineSegment(sketch, "E337", {"start": v(-3.24, -0.24) * mm, "end": v(-3.15, -0.24) * mm});
            skLineSegment(sketch, "E338", {"start": v(-3.15, -0.24) * mm, "end": v(-3.15, 0.05) * mm});
            skLineSegment(sketch, "E339", {"start": v(-3.15, 0.05) * mm, "end": v(-3.15, 0.44) * mm});
            skLineSegment(sketch, "E340", {"start": v(-3.15, 0.44) * mm, "end": v(-3.15, 0.54) * mm});
            skLineSegment(sketch, "E341", {"start": v(-3.15, 0.54) * mm, "end": v(-3.15, 0.63) * mm});
            skLineSegment(sketch, "E342", {"start": v(-3.15, 0.63) * mm, "end": v(-3.15, 0.73) * mm});
            skLineSegment(sketch, "E343", {"start": v(-3.15, 0.73) * mm, "end": v(-3.15, 1.12) * mm});
            skLineSegment(sketch, "E344", {"start": v(-3.15, 1.12) * mm, "end": v(-3.05, 1.12) * mm});
            skLineSegment(sketch, "E345", {"start": v(-3.05, 1.12) * mm, "end": v(-3.05, 1.4) * mm});
            skLineSegment(sketch, "E346", {"start": v(-3.05, 1.4) * mm, "end": v(-3.05, 2.38) * mm});
            skLineSegment(sketch, "E347", {"start": v(-3.05, 2.38) * mm, "end": v(-2.95, 2.38) * mm});
            skLineSegment(sketch, "E348", {"start": v(-2.95, 2.38) * mm, "end": v(-2.95, 2.67) * mm});
            skLineSegment(sketch, "E349", {"start": v(-2.95, 2.67) * mm, "end": v(-2.95, 3.06) * mm});
            skLineSegment(sketch, "E350", {"start": v(-2.95, 3.06) * mm, "end": v(-2.95, 3.15) * mm});
            skLineSegment(sketch, "E351", {"start": v(-2.95, 3.15) * mm, "end": v(-2.95, 3.25) * mm});
            skLineSegment(sketch, "E352", {"start": v(-2.95, 3.25) * mm, "end": v(-2.95, 3.35) * mm});
            skLineSegment(sketch, "E353", {"start": v(-2.95, 3.35) * mm, "end": v(-2.95, 3.73) * mm});
            skLineSegment(sketch, "E354", {"start": v(-2.95, 3.73) * mm, "end": v(-2.86, 3.73) * mm});
            skLineSegment(sketch, "E355", {"start": v(-2.86, 3.73) * mm, "end": v(-2.86, 4.02) * mm});
            skLineSegment(sketch, "E356", {"start": v(-2.86, 4.02) * mm, "end": v(-2.86, 4.8) * mm});
            skLineSegment(sketch, "E357", {"start": v(-2.86, 4.8) * mm, "end": v(-2.76, 4.8) * mm});
            skLineSegment(sketch, "E358", {"start": v(-2.76, 4.8) * mm, "end": v(-2.76, 5.09) * mm});
            skLineSegment(sketch, "E359", {"start": v(-2.76, 5.09) * mm, "end": v(-2.76, 5.96) * mm});
            skLineSegment(sketch, "E360", {"start": v(-2.76, 5.96) * mm, "end": v(-2.66, 5.96) * mm});
            skLineSegment(sketch, "E361", {"start": v(-2.66, 5.96) * mm, "end": v(-2.66, 6.25) * mm});
            skLineSegment(sketch, "E362", {"start": v(-2.66, 6.25) * mm, "end": v(-2.66, 6.54) * mm});
            skLineSegment(sketch, "E363", {"start": v(-2.66, 6.54) * mm, "end": v(-2.66, 6.83) * mm});
            skLineSegment(sketch, "E364", {"start": v(-2.66, 6.83) * mm, "end": v(-2.57, 6.83) * mm});
            skLineSegment(sketch, "E365", {"start": v(-2.57, 6.83) * mm, "end": v(-2.57, 7.12) * mm});
            skLineSegment(sketch, "E366", {"start": v(-2.57, 7.12) * mm, "end": v(-2.57, 7.41) * mm});
            skLineSegment(sketch, "E367", {"start": v(-2.57, 7.41) * mm, "end": v(-2.57, 7.7) * mm});
            skLineSegment(sketch, "E368", {"start": v(-2.57, 7.7) * mm, "end": v(-2.47, 7.7) * mm});
            skLineSegment(sketch, "E369", {"start": v(-2.47, 7.7) * mm, "end": v(-2.47, 8.29) * mm});
            skLineSegment(sketch, "E370", {"start": v(-2.47, 8.29) * mm, "end": v(-2.37, 8.29) * mm});
            skLineSegment(sketch, "E371", {"start": v(-2.37, 8.29) * mm, "end": v(-2.37, 8.96) * mm});
            skLineSegment(sketch, "E372", {"start": v(-2.37, 8.96) * mm, "end": v(-2.28, 8.96) * mm});
            skLineSegment(sketch, "E373", {"start": v(-2.28, 8.96) * mm, "end": v(-2.28, 9.35) * mm});
            skLineSegment(sketch, "E374", {"start": v(-2.28, 9.35) * mm, "end": v(-2.18, 9.35) * mm});
            skLineSegment(sketch, "E375", {"start": v(-2.18, 9.35) * mm, "end": v(-2.18, 9.74) * mm});
            skLineSegment(sketch, "E376", {"start": v(-2.18, 9.74) * mm, "end": v(-1.6, 10.03) * mm});
            skLineSegment(sketch, "E377", {"start": v(-1.6, 10.03) * mm, "end": v(-1.7, 10.22) * mm});
            skLineSegment(sketch, "E378", {"start": v(-1.7, 10.22) * mm, "end": v(-1.6, 10.22) * mm});
            skLineSegment(sketch, "E379", {"start": v(-1.6, 10.22) * mm, "end": v(-1.21, 9.93) * mm});
            skLineSegment(sketch, "E380", {"start": v(-1.21, 9.93) * mm, "end": v(-1.02, 9.54) * mm});
            skLineSegment(sketch, "E381", {"start": v(-1.02, 9.54) * mm, "end": v(-1.02, 9.35) * mm});
            skLineSegment(sketch, "E382", {"start": v(-1.02, 9.35) * mm, "end": v(-1.02, 8.67) * mm});
            skLineSegment(sketch, "E383", {"start": v(-1.02, 8.67) * mm, "end": v(-0.92, 8.67) * mm});
            skLineSegment(sketch, "E384", {"start": v(-0.92, 8.67) * mm, "end": v(-0.92, 8.38) * mm});
            skLineSegment(sketch, "E385", {"start": v(-0.92, 8.38) * mm, "end": v(-0.92, 7.7) * mm});
            skLineSegment(sketch, "E386", {"start": v(-0.92, 7.7) * mm, "end": v(-0.82, 7.7) * mm});
            skLineSegment(sketch, "E387", {"start": v(-0.82, 7.7) * mm, "end": v(-0.82, 7.41) * mm});
            skLineSegment(sketch, "E388", {"start": v(-0.82, 7.41) * mm, "end": v(-0.82, 7.03) * mm});
            skLineSegment(sketch, "E389", {"start": v(-0.82, 7.03) * mm, "end": v(-0.82, 6.93) * mm});
            skLineSegment(sketch, "E390", {"start": v(-0.82, 6.93) * mm, "end": v(-0.82, 6.83) * mm});
            skLineSegment(sketch, "E391", {"start": v(-0.82, 6.83) * mm, "end": v(-0.82, 6.74) * mm});
            skLineSegment(sketch, "E392", {"start": v(-0.82, 6.74) * mm, "end": v(-0.82, 6.15) * mm});
            skLineSegment(sketch, "E393", {"start": v(-0.82, 6.15) * mm, "end": v(-0.73, 6.15) * mm});
            skLineSegment(sketch, "E394", {"start": v(-0.73, 6.15) * mm, "end": v(-0.73, 5.86) * mm});
            skLineSegment(sketch, "E395", {"start": v(-0.73, 5.86) * mm, "end": v(-0.73, 5.48) * mm});
            skLineSegment(sketch, "E396", {"start": v(-0.73, 5.48) * mm, "end": v(-0.73, 5.38) * mm});
            skLineSegment(sketch, "E397", {"start": v(-0.73, 5.38) * mm, "end": v(-0.73, 5.28) * mm});
            skLineSegment(sketch, "E398", {"start": v(-0.73, 5.28) * mm, "end": v(-0.73, 5.19) * mm});
            skLineSegment(sketch, "E399", {"start": v(-0.73, 5.19) * mm, "end": v(-0.73, 5.09) * mm});
            skLineSegment(sketch, "E400", {"start": v(-0.73, 5.09) * mm, "end": v(-0.73, 5) * mm});
            skLineSegment(sketch, "E401", {"start": v(-0.73, 5) * mm, "end": v(-0.73, 4.9) * mm});
            skLineSegment(sketch, "E402", {"start": v(-0.73, 4.9) * mm, "end": v(-0.73, 4.8) * mm});
            skLineSegment(sketch, "E403", {"start": v(-0.73, 4.8) * mm, "end": v(-0.73, 4.31) * mm});
            skLineSegment(sketch, "E404", {"start": v(-0.73, 4.31) * mm, "end": v(-0.63, 4.31) * mm});
            skLineSegment(sketch, "E405", {"start": v(-0.63, 4.31) * mm, "end": v(-0.63, 4.02) * mm});
            skLineSegment(sketch, "E406", {"start": v(-0.63, 4.02) * mm, "end": v(-0.63, 3.64) * mm});
            skLineSegment(sketch, "E407", {"start": v(-0.63, 3.64) * mm, "end": v(-0.63, 3.54) * mm});
            skLineSegment(sketch, "E408", {"start": v(-0.63, 3.54) * mm, "end": v(-0.63, 3.44) * mm});
            skLineSegment(sketch, "E409", {"start": v(-0.63, 3.44) * mm, "end": v(-0.63, 3.35) * mm});
            skLineSegment(sketch, "E410", {"start": v(-0.63, 3.35) * mm, "end": v(-0.63, 2.77) * mm});
            skLineSegment(sketch, "E411", {"start": v(-0.63, 2.77) * mm, "end": v(-0.53, 2.77) * mm});
            skLineSegment(sketch, "E412", {"start": v(-0.53, 2.77) * mm, "end": v(-0.53, 2.47) * mm});
            skLineSegment(sketch, "E413", {"start": v(-0.53, 2.47) * mm, "end": v(-0.53, 2.09) * mm});
            skLineSegment(sketch, "E414", {"start": v(-0.53, 2.09) * mm, "end": v(-0.53, 2) * mm});
            skLineSegment(sketch, "E415", {"start": v(-0.53, 2) * mm, "end": v(-0.53, 1.9) * mm});
            skLineSegment(sketch, "E416", {"start": v(-0.53, 1.9) * mm, "end": v(-0.53, 1.8) * mm});
            skLineSegment(sketch, "E417", {"start": v(-0.53, 1.8) * mm, "end": v(-0.53, 1.31) * mm});
            skLineSegment(sketch, "E418", {"start": v(-0.53, 1.31) * mm, "end": v(-0.44, 1.31) * mm});
            skLineSegment(sketch, "E419", {"start": v(-0.44, 1.31) * mm, "end": v(-0.44, 1.02) * mm});
            skLineSegment(sketch, "E420", {"start": v(-0.44, 1.02) * mm, "end": v(-0.44, 0.63) * mm});
            skLineSegment(sketch, "E421", {"start": v(-0.44, 0.63) * mm, "end": v(-0.44, 0.54) * mm});
            skLineSegment(sketch, "E422", {"start": v(-0.44, 0.54) * mm, "end": v(-0.44, 0.44) * mm});
            skLineSegment(sketch, "E423", {"start": v(-0.44, 0.44) * mm, "end": v(-0.44, 0.34) * mm});
            skLineSegment(sketch, "E424", {"start": v(-0.44, 0.34) * mm, "end": v(-0.44, -0.14) * mm});
            skLineSegment(sketch, "E425", {"start": v(-0.44, -0.14) * mm, "end": v(-0.34, -0.14) * mm});
            skLineSegment(sketch, "E426", {"start": v(-0.34, -0.14) * mm, "end": v(-0.34, -0.43) * mm});
            skLineSegment(sketch, "E427", {"start": v(-0.34, -0.43) * mm, "end": v(-0.34, -0.82) * mm});
            skLineSegment(sketch, "E428", {"start": v(-0.34, -0.82) * mm, "end": v(-0.34, -0.92) * mm});
            skLineSegment(sketch, "E429", {"start": v(-0.34, -0.92) * mm, "end": v(-0.34, -1.01) * mm});
            skLineSegment(sketch, "E430", {"start": v(-0.34, -1.01) * mm, "end": v(-0.34, -1.1) * mm});
            skLineSegment(sketch, "E431", {"start": v(-0.34, -1.1) * mm, "end": v(-0.34, -1.6) * mm});
            skLineSegment(sketch, "E432", {"start": v(-0.34, -1.6) * mm, "end": v(-0.24, -1.6) * mm});
            skLineSegment(sketch, "E433", {"start": v(-0.24, -1.6) * mm, "end": v(-0.24, -1.88) * mm});
            skLineSegment(sketch, "E434", {"start": v(-0.24, -1.88) * mm, "end": v(-0.24, -2.85) * mm});
            skLineSegment(sketch, "E435", {"start": v(-0.24, -2.85) * mm, "end": v(-0.15, -2.85) * mm});
            skLineSegment(sketch, "E436", {"start": v(-0.15, -2.85) * mm, "end": v(-0.15, -3.14) * mm});
            skLineSegment(sketch, "E437", {"start": v(-0.15, -3.14) * mm, "end": v(-0.15, -4.11) * mm});
            skLineSegment(sketch, "E438", {"start": v(-0.15, -4.11) * mm, "end": v(-0.05, -4.11) * mm});
            skLineSegment(sketch, "E439", {"start": v(-0.05, -4.11) * mm, "end": v(-0.05, -4.4) * mm});
            skLineSegment(sketch, "E440", {"start": v(-0.05, -4.4) * mm, "end": v(-0.05, -5.08) * mm});
            skLineSegment(sketch, "E441", {"start": v(-0.05, -5.08) * mm, "end": v(0.05, -5.08) * mm});
            skLineSegment(sketch, "E442", {"start": v(0.05, -5.08) * mm, "end": v(0.05, -5.37) * mm});
            skLineSegment(sketch, "E443", {"start": v(0.05, -5.37) * mm, "end": v(0.05, -6.05) * mm});
            skLineSegment(sketch, "E444", {"start": v(0.05, -6.05) * mm, "end": v(0.15, -6.05) * mm});
            skLineSegment(sketch, "E445", {"start": v(0.15, -6.05) * mm, "end": v(0.15, -6.34) * mm});
            skLineSegment(sketch, "E446", {"start": v(0.15, -6.34) * mm, "end": v(0.15, -6.63) * mm});
            skLineSegment(sketch, "E447", {"start": v(0.15, -6.63) * mm, "end": v(0.15, -6.92) * mm});
            skLineSegment(sketch, "E448", {"start": v(0.15, -6.92) * mm, "end": v(0.24, -6.92) * mm});
            skLineSegment(sketch, "E449", {"start": v(0.24, -6.92) * mm, "end": v(0.24, -7.6) * mm});
            skLineSegment(sketch, "E450", {"start": v(0.24, -7.6) * mm, "end": v(0.34, -7.6) * mm});
            skLineSegment(sketch, "E451", {"start": v(0.34, -7.6) * mm, "end": v(0.34, -7.99) * mm});
            skLineSegment(sketch, "E452", {"start": v(0.34, -7.99) * mm, "end": v(0.44, -7.99) * mm});
            skLineSegment(sketch, "E453", {"start": v(0.44, -7.99) * mm, "end": v(0.53, -7.8) * mm});
            skLineSegment(sketch, "E454", {"start": v(0.53, -7.8) * mm, "end": v(0.53, -7.4) * mm});
            skLineSegment(sketch, "E455", {"start": v(0.53, -7.4) * mm, "end": v(0.63, -7.4) * mm});
            skLineSegment(sketch, "E456", {"start": v(0.63, -7.4) * mm, "end": v(0.63, -7.02) * mm});
            skLineSegment(sketch, "E457", {"start": v(0.63, -7.02) * mm, "end": v(0.73, -7.02) * mm});
            skLineSegment(sketch, "E458", {"start": v(0.73, -7.02) * mm, "end": v(0.73, -6.63) * mm});
            skLineSegment(sketch, "E459", {"start": v(0.73, -6.63) * mm, "end": v(0.82, -6.63) * mm});
            skLineSegment(sketch, "E460", {"start": v(0.82, -6.63) * mm, "end": v(0.82, -6.15) * mm});
            skLineSegment(sketch, "E461", {"start": v(0.82, -6.15) * mm, "end": v(0.92, -6.15) * mm});
            skLineSegment(sketch, "E462", {"start": v(0.92, -6.15) * mm, "end": v(0.92, -5.56) * mm});
            skLineSegment(sketch, "E463", {"start": v(0.92, -5.56) * mm, "end": v(1.02, -5.56) * mm});
            skLineSegment(sketch, "E464", {"start": v(1.02, -5.56) * mm, "end": v(1.02, -4.98) * mm});
            skLineSegment(sketch, "E465", {"start": v(1.02, -4.98) * mm, "end": v(1.11, -4.98) * mm});
            skLineSegment(sketch, "E466", {"start": v(1.11, -4.98) * mm, "end": v(1.11, -4.4) * mm});
            skLineSegment(sketch, "E467", {"start": v(1.11, -4.4) * mm, "end": v(1.21, -4.4) * mm});
            skLineSegment(sketch, "E468", {"start": v(1.21, -4.4) * mm, "end": v(1.21, -3.92) * mm});
            skLineSegment(sketch, "E469", {"start": v(1.21, -3.92) * mm, "end": v(1.3, -3.92) * mm});
            skLineSegment(sketch, "E470", {"start": v(1.3, -3.92) * mm, "end": v(1.3, -3.43) * mm});
            skLineSegment(sketch, "E471", {"start": v(1.3, -3.43) * mm, "end": v(1.4, -3.43) * mm});
            skLineSegment(sketch, "E472", {"start": v(1.4, -3.43) * mm, "end": v(1.4, -2.95) * mm});
            skLineSegment(sketch, "E473", {"start": v(1.4, -2.95) * mm, "end": v(1.5, -2.95) * mm});
            skLineSegment(sketch, "E474", {"start": v(1.5, -2.95) * mm, "end": v(1.5, -2.56) * mm});
            skLineSegment(sketch, "E475", {"start": v(1.5, -2.56) * mm, "end": v(1.6, -2.27) * mm});
            skLineSegment(sketch, "E476", {"start": v(1.6, -2.27) * mm, "end": v(1.89, -1.79) * mm});
            skLineSegment(sketch, "E477", {"start": v(1.89, -1.79) * mm, "end": v(2.18, -1.6) * mm});
            skLineSegment(sketch, "E478", {"start": v(2.18, -1.6) * mm, "end": v(2.57, -1.6) * mm});
            skLineSegment(sketch, "E479", {"start": v(2.57, -1.6) * mm, "end": v(3.05, -1.88) * mm});
            skLineSegment(sketch, "E480", {"start": v(3.05, -1.88) * mm, "end": v(3.05, -1.1) * mm});
            skLineSegment(sketch, "E481", {"start": v(3.05, -1.1) * mm, "end": v(3.15, -1.1) * mm});
            skLineSegment(sketch, "E482", {"start": v(3.15, -1.1) * mm, "end": v(3.15, -0.33) * mm});
            skLineSegment(sketch, "E483", {"start": v(3.15, -0.33) * mm, "end": v(3.24, -0.33) * mm});
            skLineSegment(sketch, "E484", {"start": v(3.24, -0.33) * mm, "end": v(3.24, 0.15) * mm});
            skLineSegment(sketch, "E485", {"start": v(3.24, 0.15) * mm, "end": v(3.34, 0.15) * mm});
            skLineSegment(sketch, "E486", {"start": v(3.34, 0.15) * mm, "end": v(3.34, 0.54) * mm});
            skLineSegment(sketch, "E487", {"start": v(3.34, 0.54) * mm, "end": v(3.63, 1.12) * mm});
            skLineSegment(sketch, "E488", {"start": v(3.63, 1.12) * mm, "end": v(3.92, 1.31) * mm});
            skLineSegment(sketch, "E489", {"start": v(3.92, 1.31) * mm, "end": v(4.02, 1.31) * mm});
            skLineSegment(sketch, "E490", {"start": v(4.02, 1.31) * mm, "end": v(4.3, 1.12) * mm});
            skLineSegment(sketch, "E491", {"start": v(4.3, 1.12) * mm, "end": v(4.5, 0.83) * mm});
            skLineSegment(sketch, "E492", {"start": v(4.5, 0.83) * mm, "end": v(4.6, 0.54) * mm});
            skLineSegment(sketch, "E493", {"start": v(4.6, 0.54) * mm, "end": v(4.6, 0.05) * mm});
            skLineSegment(sketch, "E494", {"start": v(4.6, 0.05) * mm, "end": v(4.7, 0.05) * mm});
            skLineSegment(sketch, "E495", {"start": v(4.7, 0.05) * mm, "end": v(4.7, -0.53) * mm});
            skLineSegment(sketch, "E496", {"start": v(4.7, -0.53) * mm, "end": v(4.8, -0.53) * mm});
            skLineSegment(sketch, "E497", {"start": v(4.8, -0.53) * mm, "end": v(4.8, -1.1) * mm});
            skLineSegment(sketch, "E498", {"start": v(4.8, -1.1) * mm, "end": v(4.9, -1.1) * mm});
            skLineSegment(sketch, "E499", {"start": v(4.9, -1.1) * mm, "end": v(4.9, -1.7) * mm});
            skLineSegment(sketch, "E500", {"start": v(4.9, -1.7) * mm, "end": v(4.99, -1.7) * mm});
            skLineSegment(sketch, "E501", {"start": v(4.99, -1.7) * mm, "end": v(4.99, -2.08) * mm});
            skLineSegment(sketch, "E502", {"start": v(4.99, -2.08) * mm, "end": v(5.08, -2.08) * mm});
            skLineSegment(sketch, "E503", {"start": v(5.08, -2.08) * mm, "end": v(5.08, -2.46) * mm});
            skLineSegment(sketch, "E504", {"start": v(5.08, -2.46) * mm, "end": v(5.18, -2.76) * mm});
            skLineSegment(sketch, "E505", {"start": v(5.18, -2.76) * mm, "end": v(5.28, -2.76) * mm});
            skLineSegment(sketch, "E506", {"start": v(5.28, -2.76) * mm, "end": v(5.38, -3.24) * mm});
            skLineSegment(sketch, "E507", {"start": v(5.38, -3.24) * mm, "end": v(5.57, -3.24) * mm});
            skLineSegment(sketch, "E508", {"start": v(5.57, -3.24) * mm, "end": v(5.67, -2.85) * mm});
            skLineSegment(sketch, "E509", {"start": v(5.67, -2.85) * mm, "end": v(5.86, -2.76) * mm});
            skLineSegment(sketch, "E510", {"start": v(5.86, -2.76) * mm, "end": v(5.86, -2.56) * mm});
            skLineSegment(sketch, "E511", {"start": v(5.86, -2.56) * mm, "end": v(5.96, -2.56) * mm});
            skLineSegment(sketch, "E512", {"start": v(5.96, -2.56) * mm, "end": v(5.96, -2.37) * mm});
            skLineSegment(sketch, "E513", {"start": v(5.96, -2.37) * mm, "end": v(6.05, -2.17) * mm});
            skLineSegment(sketch, "E514", {"start": v(6.05, -2.17) * mm, "end": v(6.25, -2.08) * mm});
            skLineSegment(sketch, "E515", {"start": v(6.25, -2.08) * mm, "end": v(6.34, -1.7) * mm});
            skLineSegment(sketch, "E516", {"start": v(6.34, -1.7) * mm, "end": v(6.54, -1.6) * mm});
            skLineSegment(sketch, "E517", {"start": v(6.54, -1.6) * mm, "end": v(6.63, -1.3) * mm});
            skLineSegment(sketch, "E518", {"start": v(6.63, -1.3) * mm, "end": v(6.92, -1.1) * mm});
            skLineSegment(sketch, "E519", {"start": v(6.92, -1.1) * mm, "end": v(7.31, -1.1) * mm});
            skLineSegment(sketch, "E520", {"start": v(7.31, -1.1) * mm, "end": v(7.6, -1.3) * mm});
            skLineSegment(sketch, "E521", {"start": v(7.6, -1.3) * mm, "end": v(7.8, -1.5) * mm});
            skLineSegment(sketch, "E522", {"start": v(7.8, -1.5) * mm, "end": v(7.8, -1.6) * mm});
            skLineSegment(sketch, "E523", {"start": v(7.8, -1.6) * mm, "end": v(7.9, -1.6) * mm});
            skLineSegment(sketch, "E524", {"start": v(7.9, -1.6) * mm, "end": v(7.9, -1.7) * mm});
            skLineSegment(sketch, "E525", {"start": v(7.9, -1.7) * mm, "end": v(8.18, -1.98) * mm});
            skLineSegment(sketch, "E526", {"start": v(8.18, -1.98) * mm, "end": v(8.57, -2.17) * mm});
            skLineSegment(sketch, "E527", {"start": v(8.57, -2.17) * mm, "end": v(8.96, -2.17) * mm});
            skLineSegment(sketch, "E528", {"start": v(8.96, -2.17) * mm, "end": v(9.06, -2.17) * mm});
            skLineSegment(sketch, "E529", {"start": v(9.06, -2.17) * mm, "end": v(9.15, -2.17) * mm});
            skLineSegment(sketch, "E530", {"start": v(9.15, -2.17) * mm, "end": v(9.25, -2.17) * mm});
            skLineSegment(sketch, "E531", {"start": v(9.25, -2.17) * mm, "end": v(9.35, -2.17) * mm});
            skLineSegment(sketch, "E532", {"start": v(9.35, -2.17) * mm, "end": v(9.44, -2.17) * mm});
            skLineSegment(sketch, "E533", {"start": v(9.44, -2.17) * mm, "end": v(9.54, -2.17) * mm});
            skLineSegment(sketch, "E534", {"start": v(9.54, -2.17) * mm, "end": v(9.64, -2.17) * mm});
            skLineSegment(sketch, "E535", {"start": v(9.64, -2.17) * mm, "end": v(9.73, -2.17) * mm});
            skLineSegment(sketch, "E536", {"start": v(9.73, -2.17) * mm, "end": v(9.83, -2.17) * mm});
            skLineSegment(sketch, "E537", {"start": v(9.83, -2.17) * mm, "end": v(9.93, -2.17) * mm});
            skLineSegment(sketch, "E538", {"start": v(9.93, -2.17) * mm, "end": v(10.02, -2.17) * mm});
            skLineSegment(sketch, "E539", {"start": v(10.02, -2.17) * mm, "end": v(10.12, -2.17) * mm});
            skLineSegment(sketch, "E540", {"start": v(10.12, -2.17) * mm, "end": v(10.22, -2.17) * mm});
            skLineSegment(sketch, "E541", {"start": v(10.22, -2.17) * mm, "end": v(10.31, -2.17) * mm});
            skLineSegment(sketch, "E542", {"start": v(10.31, -2.17) * mm, "end": v(10.41, -2.17) * mm});
            skLineSegment(sketch, "E543", {"start": v(10.41, -2.17) * mm, "end": v(10.5, -2.17) * mm});
            skLineSegment(sketch, "E544", {"start": v(10.5, -2.17) * mm, "end": v(10.6, -2.17) * mm});
            skLineSegment(sketch, "E545", {"start": v(10.6, -2.17) * mm, "end": v(10.7, -2.17) * mm});
            skLineSegment(sketch, "E546", {"start": v(10.7, -2.17) * mm, "end": v(10.8, -2.17) * mm});
            skLineSegment(sketch, "E547", {"start": v(10.8, -2.17) * mm, "end": v(10.9, -2.17) * mm});
            skLineSegment(sketch, "E548", {"start": v(10.9, -2.17) * mm, "end": v(11, -2.17) * mm});
            skLineSegment(sketch, "E549", {"start": v(11, -2.17) * mm, "end": v(11.09, -2.17) * mm});
            skLineSegment(sketch, "E550", {"start": v(11.09, -2.17) * mm, "end": v(11.19, -2.17) * mm});
            skLineSegment(sketch, "E551", {"start": v(11.19, -2.17) * mm, "end": v(11.28, -2.17) * mm});
            skLineSegment(sketch, "E552", {"start": v(11.28, -2.17) * mm, "end": v(11.38, -2.17) * mm});
            skLineSegment(sketch, "E553", {"start": v(11.38, -2.17) * mm, "end": v(11.48, -2.17) * mm});
            skLineSegment(sketch, "E554", {"start": v(11.48, -2.17) * mm, "end": v(11.57, -2.17) * mm});
            skLineSegment(sketch, "E555", {"start": v(11.57, -2.17) * mm, "end": v(12.45, -2.08) * mm});
            skLineSegment(sketch, "E556", {"start": v(12.45, -2.08) * mm, "end": v(12.06, -2.37) * mm});
            skLineSegment(sketch, "E557", {"start": v(12.06, -2.37) * mm, "end": v(12.06, -2.46) * mm});
            skLineSegment(sketch, "E558", {"start": v(12.06, -2.46) * mm, "end": v(11.96, -2.46) * mm});
            skLineSegment(sketch, "E559", {"start": v(11.96, -2.46) * mm, "end": v(11.96, -2.56) * mm});
            skLineSegment(sketch, "E560", {"start": v(11.96, -2.56) * mm, "end": v(11.86, -2.56) * mm});
            skLineSegment(sketch, "E561", {"start": v(11.86, -2.56) * mm, "end": v(11.86, -2.66) * mm});
            skLineSegment(sketch, "E562", {"start": v(11.86, -2.66) * mm, "end": v(11.77, -2.66) * mm});
            skLineSegment(sketch, "E563", {"start": v(11.77, -2.66) * mm, "end": v(11.77, -2.76) * mm});
            skLineSegment(sketch, "E564", {"start": v(11.76, -2.75) * mm, "end": v(11.42, -2.93) * mm});
            skLineSegment(sketch, "E565", {"start": v(11.42, -2.93) * mm, "end": v(11.96, -2.93) * mm});
            skLineSegment(sketch, "E566", {"start": v(11.96, -2.95) * mm, "end": v(12.06, -2.95) * mm});
            skLineSegment(sketch, "E567", {"start": v(12.06, -2.95) * mm, "end": v(12.15, -2.95) * mm});
            skLineSegment(sketch, "E568", {"start": v(12.15, -2.95) * mm, "end": v(12.25, -2.95) * mm});
            skLineSegment(sketch, "E569", {"start": v(12.25, -2.95) * mm, "end": v(12.35, -2.95) * mm});
            skLineSegment(sketch, "E570", {"start": v(12.35, -2.95) * mm, "end": v(12.45, -2.95) * mm});
            skLineSegment(sketch, "E571", {"start": v(12.45, -2.95) * mm, "end": v(12.54, -2.95) * mm});
            skLineSegment(sketch, "E572", {"start": v(12.54, -2.95) * mm, "end": v(12.64, -2.95) * mm});
            skLineSegment(sketch, "E573", {"start": v(12.64, -2.95) * mm, "end": v(12.74, -2.95) * mm});
            skLineSegment(sketch, "E574", {"start": v(12.74, -2.95) * mm, "end": v(12.83, -2.95) * mm});
            skLineSegment(sketch, "E575", {"start": v(12.83, -2.95) * mm, "end": v(12.93, -2.95) * mm});
            skLineSegment(sketch, "E576", {"start": v(12.93, -2.95) * mm, "end": v(13.03, -2.95) * mm});
            skLineSegment(sketch, "E577", {"start": v(13.03, -2.95) * mm, "end": v(13.12, -2.95) * mm});
            skLineSegment(sketch, "E578", {"start": v(13.12, -2.95) * mm, "end": v(13.22, -2.95) * mm});
            skLineSegment(sketch, "E579", {"start": v(13.22, -2.95) * mm, "end": v(13.32, -2.95) * mm});
            skLineSegment(sketch, "E580", {"start": v(13.32, -2.95) * mm, "end": v(13.41, -2.95) * mm});
            skLineSegment(sketch, "E581", {"start": v(13.41, -2.95) * mm, "end": v(13.51, -2.95) * mm});
            skLineSegment(sketch, "E582", {"start": v(13.51, -2.95) * mm, "end": v(13.6, -2.95) * mm});
            skLineSegment(sketch, "E583", {"start": v(13.6, -2.95) * mm, "end": v(13.7, -2.95) * mm});
            skLineSegment(sketch, "E584", {"start": v(13.7, -2.95) * mm, "end": v(13.8, -2.95) * mm});
            skLineSegment(sketch, "E585", {"start": v(13.8, -2.95) * mm, "end": v(13.9, -2.95) * mm});
            skLineSegment(sketch, "E586", {"start": v(13.9, -2.95) * mm, "end": v(14, -2.95) * mm});
            skLineSegment(sketch, "E587", {"start": v(14, -2.95) * mm, "end": v(14.1, -2.95) * mm});
            skLineSegment(sketch, "E588", {"start": v(14.1, -2.95) * mm, "end": v(14.19, -2.95) * mm});
            skLineSegment(sketch, "E589", {"start": v(14.19, -2.95) * mm, "end": v(14.29, -2.95) * mm});
            skLineSegment(sketch, "E590", {"start": v(14.29, -2.95) * mm, "end": v(14.38, -2.95) * mm});
            skLineSegment(sketch, "E591", {"start": v(14.38, -2.95) * mm, "end": v(14.48, -2.95) * mm});
            skLineSegment(sketch, "E592", {"start": v(14.48, -2.95) * mm, "end": v(14.58, -2.95) * mm});
            skLineSegment(sketch, "E593", {"start": v(14.58, -2.95) * mm, "end": v(14.67, -2.95) * mm});
            skLineSegment(sketch, "E594", {"start": v(14.67, -2.95) * mm, "end": v(14.77, -2.95) * mm});
            skLineSegment(sketch, "E595", {"start": v(14.77, -2.95) * mm, "end": v(14.87, -2.95) * mm});
            skLineSegment(sketch, "E596", {"start": v(14.87, -2.95) * mm, "end": v(14.96, -2.95) * mm});
            skLineSegment(sketch, "E597", {"start": v(14.96, -2.95) * mm, "end": v(15.06, -2.95) * mm});
            skLineSegment(sketch, "E598", {"start": v(15.06, -2.95) * mm, "end": v(15.16, -2.95) * mm});
            skLineSegment(sketch, "E599", {"start": v(15.16, -2.95) * mm, "end": v(15.25, -2.95) * mm});
            skLineSegment(sketch, "E600", {"start": v(15.25, -2.95) * mm, "end": v(15.35, -2.95) * mm});
            skLineSegment(sketch, "E601", {"start": v(15.35, -2.95) * mm, "end": v(15.45, -2.95) * mm});
            skLineSegment(sketch, "E602", {"start": v(15.45, -2.95) * mm, "end": v(15.54, -2.95) * mm});
            skLineSegment(sketch, "E603", {"start": v(15.54, -2.95) * mm, "end": v(15.64, -2.95) * mm});
            skLineSegment(sketch, "E604", {"start": v(15.64, -2.95) * mm, "end": v(15.74, -2.95) * mm});
            skLineSegment(sketch, "E605", {"start": v(15.74, -2.95) * mm, "end": v(15.84, -2.95) * mm});
            skLineSegment(sketch, "E606", {"start": v(15.84, -2.95) * mm, "end": v(15.93, -2.95) * mm});
            skLineSegment(sketch, "E607", {"start": v(15.93, -2.95) * mm, "end": v(16.03, -2.95) * mm});
            skLineSegment(sketch, "E608", {"start": v(16.03, -2.95) * mm, "end": v(16.13, -2.95) * mm});
            skLineSegment(sketch, "E609", {"start": v(16.13, -2.95) * mm, "end": v(16.22, -2.95) * mm});
            skLineSegment(sketch, "E610", {"start": v(16.22, -2.95) * mm, "end": v(16.32, -2.95) * mm});
            skLineSegment(sketch, "E611", {"start": v(16.32, -2.95) * mm, "end": v(16.42, -2.95) * mm});
            skLineSegment(sketch, "E612", {"start": v(16.42, -2.95) * mm, "end": v(16.51, -2.95) * mm});
            skLineSegment(sketch, "E613", {"start": v(16.51, -2.95) * mm, "end": v(16.61, -2.95) * mm});
            skLineSegment(sketch, "E614", {"start": v(16.61, -2.95) * mm, "end": v(16.7, -2.95) * mm});
            skLineSegment(sketch, "E615", {"start": v(16.7, -2.95) * mm, "end": v(16.8, -2.95) * mm});
            skLineSegment(sketch, "E616", {"start": v(16.8, -2.95) * mm, "end": v(16.9, -2.95) * mm});
            skLineSegment(sketch, "E617", {"start": v(16.9, -2.95) * mm, "end": v(17, -2.95) * mm});
            skLineSegment(sketch, "E618", {"start": v(17, -2.95) * mm, "end": v(17.1, -2.95) * mm});
            skLineSegment(sketch, "E619", {"start": v(17.1, -2.95) * mm, "end": v(17.2, -2.95) * mm});
            skLineSegment(sketch, "E620", {"start": v(17.2, -2.95) * mm, "end": v(17.29, -2.95) * mm});
            skLineSegment(sketch, "E621", {"start": v(17.29, -2.95) * mm, "end": v(17.38, -2.95) * mm});
            skLineSegment(sketch, "E622", {"start": v(17.38, -2.95) * mm, "end": v(17.48, -2.95) * mm});
            skLineSegment(sketch, "E623", {"start": v(17.48, -2.95) * mm, "end": v(17.58, -2.95) * mm});
            skLineSegment(sketch, "E624", {"start": v(17.58, -2.95) * mm, "end": v(17.68, -2.95) * mm});
            skLineSegment(sketch, "E625", {"start": v(17.68, -2.95) * mm, "end": v(17.77, -2.95) * mm});
            skLineSegment(sketch, "E626", {"start": v(17.77, -2.95) * mm, "end": v(17.87, -2.95) * mm});
            skLineSegment(sketch, "E627", {"start": v(17.87, -2.95) * mm, "end": v(17.97, -2.95) * mm});
            skLineSegment(sketch, "E628", {"start": v(17.97, -2.95) * mm, "end": v(18.06, -2.95) * mm});
            skLineSegment(sketch, "E629", {"start": v(18.06, -2.95) * mm, "end": v(18.16, -2.95) * mm});
            skLineSegment(sketch, "E630", {"start": v(18.16, -2.95) * mm, "end": v(18.26, -2.95) * mm});
            skLineSegment(sketch, "E631", {"start": v(18.26, -2.95) * mm, "end": v(18.35, -2.95) * mm});
            skLineSegment(sketch, "E632", {"start": v(18.35, -2.95) * mm, "end": v(18.45, -2.95) * mm});
            skLineSegment(sketch, "E633", {"start": v(18.45, -2.95) * mm, "end": v(18.55, -2.95) * mm});
            skLineSegment(sketch, "E634", {"start": v(18.55, -2.95) * mm, "end": v(18.64, -2.95) * mm});
            skLineSegment(sketch, "E635", {"start": v(18.64, -2.95) * mm, "end": v(18.74, -2.95) * mm});
            skLineSegment(sketch, "E636", {"start": v(18.74, -2.95) * mm, "end": v(18.84, -2.95) * mm});
            skLineSegment(sketch, "E637", {"start": v(18.84, -2.95) * mm, "end": v(18.93, -2.95) * mm});
            skLineSegment(sketch, "E638", {"start": v(18.93, -2.95) * mm, "end": v(19.03, -2.95) * mm});
            skLineSegment(sketch, "E639", {"start": v(19.03, -2.95) * mm, "end": v(19.13, -2.95) * mm});
            skLineSegment(sketch, "E640", {"start": v(19.13, -2.95) * mm, "end": v(19.23, -2.95) * mm});
            skLineSegment(sketch, "E641", {"start": v(19.23, -2.95) * mm, "end": v(19.32, -2.95) * mm});
            skLineSegment(sketch, "E642", {"start": v(19.32, -2.95) * mm, "end": v(19.42, -2.95) * mm});
            skLineSegment(sketch, "E643", {"start": v(19.42, -2.95) * mm, "end": v(19.52, -2.95) * mm});
            skLineSegment(sketch, "E644", {"start": v(19.52, -2.95) * mm, "end": v(19.61, -2.95) * mm});
            skLineSegment(sketch, "E645", {"start": v(19.61, -2.95) * mm, "end": v(20.3, -2.95) * mm});
            skLineSegment(sketch, "E646", {"start": v(20.3, -2.08) * mm, "end": v(19.9, -2.08) * mm});
            skLineSegment(sketch, "E647", {"start": v(19.9, -2.08) * mm, "end": v(19.8, -2.08) * mm});
            skLineSegment(sketch, "E648", {"start": v(19.8, -2.08) * mm, "end": v(19.7, -2.08) * mm});
            skLineSegment(sketch, "E649", {"start": v(19.7, -2.08) * mm, "end": v(19.61, -2.08) * mm});
            skLineSegment(sketch, "E650", {"start": v(19.61, -2.08) * mm, "end": v(19.52, -2.08) * mm});
            skLineSegment(sketch, "E651", {"start": v(19.52, -2.08) * mm, "end": v(19.42, -2.08) * mm});
            skLineSegment(sketch, "E652", {"start": v(19.42, -2.08) * mm, "end": v(19.32, -2.08) * mm});
            skLineSegment(sketch, "E653", {"start": v(19.32, -2.08) * mm, "end": v(19.23, -2.08) * mm});
            skLineSegment(sketch, "E654", {"start": v(19.23, -2.08) * mm, "end": v(19.13, -2.08) * mm});
            skLineSegment(sketch, "E655", {"start": v(19.13, -2.08) * mm, "end": v(19.03, -2.08) * mm});
            skLineSegment(sketch, "E656", {"start": v(19.03, -2.08) * mm, "end": v(18.93, -2.08) * mm});
            skLineSegment(sketch, "E657", {"start": v(18.93, -2.08) * mm, "end": v(18.84, -2.08) * mm});
            skLineSegment(sketch, "E658", {"start": v(18.84, -2.08) * mm, "end": v(18.74, -2.08) * mm});
            skLineSegment(sketch, "E659", {"start": v(18.74, -2.08) * mm, "end": v(18.64, -2.08) * mm});
            skLineSegment(sketch, "E660", {"start": v(18.64, -2.08) * mm, "end": v(18.55, -2.08) * mm});
            skLineSegment(sketch, "E661", {"start": v(18.55, -2.08) * mm, "end": v(18.45, -2.08) * mm});
            skLineSegment(sketch, "E662", {"start": v(18.45, -2.08) * mm, "end": v(18.35, -2.08) * mm});
            skLineSegment(sketch, "E663", {"start": v(18.35, -2.08) * mm, "end": v(18.26, -2.08) * mm});
            skLineSegment(sketch, "E664", {"start": v(18.26, -2.08) * mm, "end": v(18.16, -2.08) * mm});
            skLineSegment(sketch, "E665", {"start": v(18.16, -2.08) * mm, "end": v(18.06, -2.08) * mm});
            skLineSegment(sketch, "E666", {"start": v(18.06, -2.08) * mm, "end": v(17.97, -2.08) * mm});
            skLineSegment(sketch, "E667", {"start": v(17.97, -2.08) * mm, "end": v(17.87, -2.08) * mm});
            skLineSegment(sketch, "E668", {"start": v(17.87, -2.08) * mm, "end": v(17.77, -2.08) * mm});
            skLineSegment(sketch, "E669", {"start": v(17.77, -2.08) * mm, "end": v(17.68, -2.08) * mm});
            skLineSegment(sketch, "E670", {"start": v(17.68, -2.08) * mm, "end": v(17.58, -2.08) * mm});
            skLineSegment(sketch, "E671", {"start": v(17.58, -2.08) * mm, "end": v(17.48, -2.08) * mm});
            skLineSegment(sketch, "E672", {"start": v(17.48, -2.08) * mm, "end": v(17.38, -2.08) * mm});
            skLineSegment(sketch, "E673", {"start": v(17.38, -2.08) * mm, "end": v(17.29, -2.08) * mm});
            skLineSegment(sketch, "E674", {"start": v(17.29, -2.08) * mm, "end": v(17.2, -2.08) * mm});
            skLineSegment(sketch, "E675", {"start": v(17.2, -2.08) * mm, "end": v(17.1, -2.08) * mm});
            skLineSegment(sketch, "E676", {"start": v(17.1, -2.08) * mm, "end": v(17, -2.08) * mm});
            skLineSegment(sketch, "E677", {"start": v(17, -2.08) * mm, "end": v(16.9, -2.08) * mm});
            skLineSegment(sketch, "E678", {"start": v(16.9, -2.08) * mm, "end": v(16.8, -2.08) * mm});
            skLineSegment(sketch, "E679", {"start": v(16.8, -2.08) * mm, "end": v(16.7, -2.08) * mm});
            skLineSegment(sketch, "E680", {"start": v(16.7, -2.08) * mm, "end": v(16.61, -2.08) * mm});
            skLineSegment(sketch, "E681", {"start": v(16.61, -2.08) * mm, "end": v(16.51, -2.08) * mm});
            skLineSegment(sketch, "E682", {"start": v(16.51, -2.08) * mm, "end": v(16.42, -2.08) * mm});
            skLineSegment(sketch, "E683", {"start": v(16.42, -2.08) * mm, "end": v(16.32, -2.08) * mm});
            skLineSegment(sketch, "E684", {"start": v(16.32, -2.08) * mm, "end": v(16.22, -2.08) * mm});
            skLineSegment(sketch, "E685", {"start": v(16.22, -2.08) * mm, "end": v(16.13, -2.08) * mm});
            skLineSegment(sketch, "E686", {"start": v(16.13, -2.08) * mm, "end": v(16.03, -2.08) * mm});
            skLineSegment(sketch, "E687", {"start": v(16.03, -2.08) * mm, "end": v(15.93, -2.08) * mm});
            skLineSegment(sketch, "E688", {"start": v(15.93, -2.08) * mm, "end": v(15.84, -2.08) * mm});
            skLineSegment(sketch, "E689", {"start": v(15.84, -2.08) * mm, "end": v(15.74, -2.08) * mm});
            skLineSegment(sketch, "E690", {"start": v(15.74, -2.08) * mm, "end": v(15.64, -2.08) * mm});
            skLineSegment(sketch, "E691", {"start": v(15.64, -2.08) * mm, "end": v(15.54, -2.08) * mm});
            skLineSegment(sketch, "E692", {"start": v(15.54, -2.08) * mm, "end": v(15.45, -2.08) * mm});
            skLineSegment(sketch, "E693", {"start": v(15.45, -2.08) * mm, "end": v(15.35, -2.08) * mm});
            skLineSegment(sketch, "E694", {"start": v(15.35, -2.08) * mm, "end": v(15.25, -2.08) * mm});
            skLineSegment(sketch, "E695", {"start": v(15.25, -2.08) * mm, "end": v(15.16, -2.08) * mm});
            skLineSegment(sketch, "E696", {"start": v(15.16, -2.08) * mm, "end": v(15.06, -2.08) * mm});
            skLineSegment(sketch, "E697", {"start": v(15.06, -2.08) * mm, "end": v(14.96, -2.08) * mm});
            skLineSegment(sketch, "E698", {"start": v(14.96, -2.08) * mm, "end": v(14.87, -2.08) * mm});
            skLineSegment(sketch, "E699", {"start": v(14.87, -2.08) * mm, "end": v(14.77, -2.08) * mm});
            skLineSegment(sketch, "E700", {"start": v(14.77, -2.08) * mm, "end": v(14.67, -2.08) * mm});
            skLineSegment(sketch, "E701", {"start": v(14.67, -2.08) * mm, "end": v(14.58, -2.08) * mm});
            skLineSegment(sketch, "E702", {"start": v(14.58, -2.08) * mm, "end": v(14.48, -2.08) * mm});
            skLineSegment(sketch, "E703", {"start": v(14.48, -2.08) * mm, "end": v(14.38, -2.08) * mm});
            skLineSegment(sketch, "E704", {"start": v(14.38, -2.08) * mm, "end": v(14.29, -2.08) * mm});
            skLineSegment(sketch, "E705", {"start": v(14.29, -2.08) * mm, "end": v(14.19, -2.08) * mm});
            skLineSegment(sketch, "E706", {"start": v(14.19, -2.08) * mm, "end": v(14.1, -2.08) * mm});
            skLineSegment(sketch, "E707", {"start": v(14.1, -2.08) * mm, "end": v(14, -2.08) * mm});
            skLineSegment(sketch, "E708", {"start": v(14, -2.08) * mm, "end": v(13.9, -2.08) * mm});
            skLineSegment(sketch, "E709", {"start": v(13.9, -2.08) * mm, "end": v(13.8, -2.08) * mm});
            skLineSegment(sketch, "E710", {"start": v(13.8, -2.08) * mm, "end": v(13.7, -2.08) * mm});
            skLineSegment(sketch, "E711", {"start": v(13.7, -2.08) * mm, "end": v(13.6, -2.08) * mm});
            skLineSegment(sketch, "E712", {"start": v(13.6, -2.08) * mm, "end": v(13.51, -2.08) * mm});
            skLineSegment(sketch, "E713", {"start": v(13.51, -2.08) * mm, "end": v(13.41, -2.08) * mm});
            skLineSegment(sketch, "E714", {"start": v(13.41, -2.08) * mm, "end": v(13.32, -2.08) * mm});
            skLineSegment(sketch, "E715", {"start": v(13.32, -2.08) * mm, "end": v(13.22, -2.08) * mm});
            skLineSegment(sketch, "E716", {"start": v(13.22, -2.08) * mm, "end": v(13.12, -2.08) * mm});
            skLineSegment(sketch, "E717", {"start": v(13.12, -2.08) * mm, "end": v(13.03, -2.08) * mm});
            skLineSegment(sketch, "E718", {"start": v(13.03, -2.08) * mm, "end": v(12.45, -2.08) * mm});
            skLineSegment(sketch, "E719", {"start": v(12.45, -2.08) * mm, "end": v(12.64, -1.88) * mm});
            skLineSegment(sketch, "E720", {"start": v(12.64, -1.88) * mm, "end": v(12.64, -1.79) * mm});
            skLineSegment(sketch, "E721", {"start": v(12.64, -1.79) * mm, "end": v(12.74, -1.79) * mm});
            skLineSegment(sketch, "E722", {"start": v(12.74, -1.79) * mm, "end": v(12.74, -1.7) * mm});
            skLineSegment(sketch, "E723", {"start": v(12.74, -1.7) * mm, "end": v(12.83, -1.7) * mm});
            skLineSegment(sketch, "E724", {"start": v(12.83, -1.7) * mm, "end": v(12.83, -1.6) * mm});
            skLineSegment(sketch, "E725", {"start": v(12.83, -1.6) * mm, "end": v(12.93, -1.6) * mm});
            skLineSegment(sketch, "E726", {"start": v(12.93, -1.6) * mm, "end": v(12.93, -1.5) * mm});
            skLineSegment(sketch, "E727", {"start": v(12.93, -1.5) * mm, "end": v(13.03, -1.5) * mm});
            skLineSegment(sketch, "E728", {"start": v(13.03, -1.5) * mm, "end": v(13.03, -1.4) * mm});
            skLineSegment(sketch, "E729", {"start": v(13.03, -1.4) * mm, "end": v(13.12, -1.4) * mm});
            skLineSegment(sketch, "E730", {"start": v(13.12, -1.4) * mm, "end": v(13.12, -1.3) * mm});
            skLineSegment(sketch, "E731", {"start": v(13.12, -1.3) * mm, "end": v(13.22, -1.3) * mm});
            skLineSegment(sketch, "E732", {"start": v(13.22, -1.3) * mm, "end": v(13.22, -1.2) * mm});
            skLineSegment(sketch, "E733", {"start": v(13.22, -1.2) * mm, "end": v(13.32, -1.2) * mm});
            skLineSegment(sketch, "E734", {"start": v(13.32, -1.2) * mm, "end": v(13.32, -1.1) * mm});
            skLineSegment(sketch, "E735", {"start": v(13.32, -1.1) * mm, "end": v(13.6, -0.92) * mm});
            skLineSegment(sketch, "E736", {"start": v(13.6, -0.92) * mm, "end": v(13.6, -0.72) * mm});
            skLineSegment(sketch, "E737", {"start": v(13.6, -0.72) * mm, "end": v(13.7, -0.62) * mm});
            skLineSegment(sketch, "E738", {"start": v(13.7, -0.62) * mm, "end": v(13.9, -0.53) * mm});
            skLineSegment(sketch, "E739", {"start": v(13.9, -0.53) * mm, "end": v(14, -0.43) * mm});
            skLineSegment(sketch, "E740", {"start": v(14, -0.43) * mm, "end": v(14, -0.24) * mm});
            skLineSegment(sketch, "E741", {"start": v(14, -0.24) * mm, "end": v(14.29, -0.04) * mm});
            skLineSegment(sketch, "E742", {"start": v(14.29, -0.04) * mm, "end": v(14.29, 0.15) * mm});
            skLineSegment(sketch, "E743", {"start": v(14.29, 0.15) * mm, "end": v(14.48, 0.25) * mm});
            skLineSegment(sketch, "E744", {"start": v(14.48, 0.25) * mm, "end": v(14.87, 0.92) * mm});
            skLineSegment(sketch, "E745", {"start": v(14.87, 0.92) * mm, "end": v(14.96, 1.4) * mm});
            skLineSegment(sketch, "E746", {"start": v(14.96, 1.4) * mm, "end": v(15.06, 1.4) * mm});
            skLineSegment(sketch, "E747", {"start": v(15.06, 1.4) * mm, "end": v(15.16, 1.6) * mm});
            skLineSegment(sketch, "E748", {"start": v(15.16, 1.6) * mm, "end": v(15.25, 1.9) * mm});
            skLineSegment(sketch, "E749", {"start": v(15.25, 1.9) * mm, "end": v(15.25, 2.18) * mm});
            skLineSegment(sketch, "E750", {"start": v(15.25, 2.18) * mm, "end": v(15.35, 2.18) * mm});
            skLineSegment(sketch, "E751", {"start": v(15.35, 2.18) * mm, "end": v(15.35, 2.57) * mm});
            skLineSegment(sketch, "E752", {"start": v(15.35, 2.57) * mm, "end": v(15.45, 2.57) * mm});
            skLineSegment(sketch, "E753", {"start": v(15.45, 2.57) * mm, "end": v(15.45, 3.15) * mm});
            skLineSegment(sketch, "E754", {"start": v(15.45, 3.15) * mm, "end": v(15.54, 3.15) * mm});
            skLineSegment(sketch, "E755", {"start": v(15.54, 3.15) * mm, "end": v(15.54, 3.44) * mm});
            skLineSegment(sketch, "E756", {"start": v(15.54, 3.44) * mm, "end": v(15.54, 3.83) * mm});
            skLineSegment(sketch, "E757", {"start": v(15.54, 3.83) * mm, "end": v(15.54, 3.93) * mm});
            skLineSegment(sketch, "E758", {"start": v(15.54, 3.93) * mm, "end": v(15.54, 4.02) * mm});
            skLineSegment(sketch, "E759", {"start": v(15.54, 4.02) * mm, "end": v(15.54, 4.12) * mm});
            skLineSegment(sketch, "E760", {"start": v(15.54, 4.12) * mm, "end": v(15.54, 4.22) * mm});
            skLineSegment(sketch, "E761", {"start": v(15.54, 4.22) * mm, "end": v(15.54, 4.31) * mm});
            skLineSegment(sketch, "E762", {"start": v(15.54, 4.31) * mm, "end": v(15.54, 4.41) * mm});
            skLineSegment(sketch, "E763", {"start": v(15.54, 4.41) * mm, "end": v(15.54, 4.5) * mm});
            skLineSegment(sketch, "E764", {"start": v(15.54, 4.5) * mm, "end": v(15.54, 4.6) * mm});
            skLineSegment(sketch, "E765", {"start": v(15.54, 4.6) * mm, "end": v(15.54, 4.7) * mm});
            skLineSegment(sketch, "E766", {"start": v(15.54, 4.7) * mm, "end": v(15.54, 4.8) * mm});
            skLineSegment(sketch, "E767", {"start": v(15.54, 4.8) * mm, "end": v(15.54, 4.9) * mm});
            skLineSegment(sketch, "E768", {"start": v(15.54, 4.9) * mm, "end": v(15.54, 5) * mm});
            skLineSegment(sketch, "E769", {"start": v(15.54, 5) * mm, "end": v(15.54, 5.09) * mm});
            skLineSegment(sketch, "E770", {"start": v(15.54, 5.09) * mm, "end": v(15.54, 5.19) * mm});
            skLineSegment(sketch, "E771", {"start": v(15.54, 5.19) * mm, "end": v(15.54, 5.28) * mm});
            skLineSegment(sketch, "E772", {"start": v(15.54, 5.28) * mm, "end": v(15.54, 5.67) * mm});
            skLineSegment(sketch, "E773", {"start": v(15.54, 5.67) * mm, "end": v(15.45, 5.67) * mm});
            skLineSegment(sketch, "E774", {"start": v(15.45, 5.67) * mm, "end": v(15.45, 6.35) * mm});
            skLineSegment(sketch, "E775", {"start": v(15.45, 6.35) * mm, "end": v(15.35, 6.35) * mm});
            skLineSegment(sketch, "E776", {"start": v(15.35, 6.35) * mm, "end": v(15.35, 6.83) * mm});
            skLineSegment(sketch, "E777", {"start": v(15.35, 6.83) * mm, "end": v(15.25, 6.83) * mm});
            skLineSegment(sketch, "E778", {"start": v(15.25, 6.83) * mm, "end": v(15.25, 7.22) * mm});
            skLineSegment(sketch, "E779", {"start": v(15.25, 7.22) * mm, "end": v(15.16, 7.22) * mm});
            skLineSegment(sketch, "E780", {"start": v(15.16, 7.22) * mm, "end": v(15.16, 7.6) * mm});
            skLineSegment(sketch, "E781", {"start": v(15.16, 7.6) * mm, "end": v(15.06, 7.6) * mm});
            skLineSegment(sketch, "E782", {"start": v(15.06, 7.6) * mm, "end": v(15.06, 8) * mm});
            skLineSegment(sketch, "E783", {"start": v(15.06, 8) * mm, "end": v(14.96, 8.29) * mm});
            skLineSegment(sketch, "E784", {"start": v(14.96, 8.29) * mm, "end": v(14.87, 8.29) * mm});
            skLineSegment(sketch, "E785", {"start": v(14.87, 8.29) * mm, "end": v(14.87, 8.58) * mm});
            skLineSegment(sketch, "E786", {"start": v(14.87, 8.58) * mm, "end": v(14.67, 8.77) * mm});
            skLineSegment(sketch, "E787", {"start": v(14.67, 8.77) * mm, "end": v(14.67, 9.06) * mm});
            skLineSegment(sketch, "E788", {"start": v(14.67, 9.06) * mm, "end": v(14.58, 9.25) * mm});
            skLineSegment(sketch, "E789", {"start": v(14.58, 9.25) * mm, "end": v(14.48, 9.25) * mm});
            skLineSegment(sketch, "E790", {"start": v(14.48, 9.25) * mm, "end": v(14.48, 9.45) * mm});
            skLineSegment(sketch, "E791", {"start": v(14.48, 9.45) * mm, "end": v(14.38, 9.45) * mm});
            skLineSegment(sketch, "E792", {"start": v(14.38, 9.45) * mm, "end": v(14.38, 9.64) * mm});
            skLineSegment(sketch, "E793", {"start": v(14.38, 9.64) * mm, "end": v(14.29, 9.64) * mm});
            skLineSegment(sketch, "E794", {"start": v(14.29, 9.64) * mm, "end": v(14.19, 10.03) * mm});
            skLineSegment(sketch, "E795", {"start": v(14.19, 10.03) * mm, "end": v(14, 10.13) * mm});
            skLineSegment(sketch, "E796", {"start": v(14, 10.13) * mm, "end": v(14, 10.32) * mm});
            skLineSegment(sketch, "E797", {"start": v(14, 10.32) * mm, "end": v(13.8, 10.42) * mm});
            skLineSegment(sketch, "E798", {"start": v(13.8, 10.42) * mm, "end": v(13.8, 10.61) * mm});
            skLineSegment(sketch, "E799", {"start": v(13.8, 10.61) * mm, "end": v(13.6, 10.7) * mm});
            skLineSegment(sketch, "E800", {"start": v(13.6, 10.7) * mm, "end": v(13.6, 10.9) * mm});
            skLineSegment(sketch, "E801", {"start": v(13.6, 10.9) * mm, "end": v(13.12, 11.29) * mm});
            skLineSegment(sketch, "E802", {"start": v(13.12, 11.29) * mm, "end": v(13.12, 11.48) * mm});
            skLineSegment(sketch, "E803", {"start": v(13.12, 11.48) * mm, "end": v(13.03, 11.58) * mm});
            skLineSegment(sketch, "E804", {"start": v(13.03, 11.58) * mm, "end": v(12.83, 11.77) * mm});
            skLineSegment(sketch, "E805", {"start": v(12.83, 11.77) * mm, "end": v(12.74, 11.77) * mm});
            skLineSegment(sketch, "E806", {"start": v(12.74, 11.77) * mm, "end": v(12.74, 11.87) * mm});
            skLineSegment(sketch, "E807", {"start": v(12.74, 11.87) * mm, "end": v(12.64, 11.87) * mm});
            skLineSegment(sketch, "E808", {"start": v(12.64, 11.87) * mm, "end": v(12.54, 12.06) * mm});
            skLineSegment(sketch, "E809", {"start": v(12.54, 12.06) * mm, "end": v(12.35, 12.06) * mm});
            skLineSegment(sketch, "E810", {"start": v(12.35, 12.06) * mm, "end": v(12.25, 12.16) * mm});
            skLineSegment(sketch, "E811", {"start": v(12.25, 12.16) * mm, "end": v(12.15, 12.35) * mm});
            skLineSegment(sketch, "E812", {"start": v(12.15, 12.35) * mm, "end": v(12.06, 12.45) * mm});
            skLineSegment(sketch, "E813", {"start": v(12.06, 12.45) * mm, "end": v(11.86, 12.45) * mm});
            skLineSegment(sketch, "E814", {"start": v(11.86, 12.45) * mm, "end": v(11.77, 12.64) * mm});
            skLineSegment(sketch, "E815", {"start": v(11.77, 12.64) * mm, "end": v(11.57, 12.64) * mm});
            skLineSegment(sketch, "E816", {"start": v(11.57, 12.64) * mm, "end": v(11.48, 12.84) * mm});
            skLineSegment(sketch, "E817", {"start": v(11.48, 12.84) * mm, "end": v(11.09, 12.93) * mm});
            skLineSegment(sketch, "E818", {"start": v(11.09, 12.93) * mm, "end": v(11.09, 13.03) * mm});
            skLineSegment(sketch, "E819", {"start": v(11.09, 13.03) * mm, "end": v(10.9, 13.03) * mm});
            skLineSegment(sketch, "E820", {"start": v(10.9, 13.03) * mm, "end": v(10.9, 13.13) * mm});
            skLineSegment(sketch, "E821", {"start": v(10.9, 13.13) * mm, "end": v(10.7, 13.13) * mm});
            skLineSegment(sketch, "E822", {"start": v(10.7, 13.13) * mm, "end": v(10.7, 13.23) * mm});
            skLineSegment(sketch, "E823", {"start": v(10.7, 13.23) * mm, "end": v(10.5, 13.23) * mm});
            skLineSegment(sketch, "E824", {"start": v(10.5, 13.23) * mm, "end": v(10.5, 13.32) * mm});
            skLineSegment(sketch, "E825", {"start": v(10.5, 13.32) * mm, "end": v(10.31, 13.42) * mm});
            skLineSegment(sketch, "E826", {"start": v(10.31, 13.42) * mm, "end": v(10.02, 13.52) * mm});
            skLineSegment(sketch, "E827", {"start": v(10.02, 13.52) * mm, "end": v(9.73, 13.52) * mm});
            skLineSegment(sketch, "E828", {"start": v(9.73, 13.52) * mm, "end": v(9.73, 13.61) * mm});
            skLineSegment(sketch, "E829", {"start": v(9.73, 13.61) * mm, "end": v(9.44, 13.61) * mm});
            skLineSegment(sketch, "E830", {"start": v(9.44, 13.61) * mm, "end": v(9.44, 13.7) * mm});
            skLineSegment(sketch, "E831", {"start": v(9.44, 13.7) * mm, "end": v(9.06, 13.7) * mm});
            skLineSegment(sketch, "E832", {"start": v(9.06, 13.7) * mm, "end": v(9.06, 13.8) * mm});
            skLineSegment(sketch, "E833", {"start": v(9.06, 13.8) * mm, "end": v(8.57, 13.8) * mm});
            skLineSegment(sketch, "E834", {"start": v(8.57, 13.8) * mm, "end": v(8.57, 13.9) * mm});
            skLineSegment(sketch, "E835", {"start": v(8.57, 13.9) * mm, "end": v(8.28, 13.9) * mm});
            skLineSegment(sketch, "E836", {"start": v(8.28, 13.9) * mm, "end": v(8, 13.9) * mm});
            skLineSegment(sketch, "E837", {"start": v(8, 13.9) * mm, "end": v(7.7, 13.9) * mm});
            skLineSegment(sketch, "E838", {"start": v(7.7, 13.9) * mm, "end": v(7.7, 14) * mm});
            skLineSegment(sketch, "E839", {"start": v(7.7, 14) * mm, "end": v(7.4, 14) * mm});
            skLineSegment(sketch, "E840", {"start": v(7.4, 14) * mm, "end": v(6.54, 14) * mm});
            skLineSegment(sketch, "E841", {"start": v(6.54, 14) * mm, "end": v(6.54, 13.9) * mm});
            skLineSegment(sketch, "E842", {"start": v(6.54, 13.9) * mm, "end": v(6.25, 13.9) * mm});
            skLineSegment(sketch, "E843", {"start": v(6.25, 13.9) * mm, "end": v(5.96, 13.9) * mm});
            skLineSegment(sketch, "E844", {"start": v(5.96, 13.9) * mm, "end": v(5.67, 13.9) * mm});
            skLineSegment(sketch, "E845", {"start": v(5.67, 13.9) * mm, "end": v(5.67, 13.8) * mm});
            skLineSegment(sketch, "E846", {"start": v(5.67, 13.8) * mm, "end": v(5.08, 13.8) * mm});
            skLineSegment(sketch, "E847", {"start": v(5.08, 13.8) * mm, "end": v(5.08, 13.7) * mm});
            skLineSegment(sketch, "E848", {"start": v(5.08, 13.7) * mm, "end": v(4.7, 13.7) * mm});
            skLineSegment(sketch, "E849", {"start": v(4.7, 13.7) * mm, "end": v(4.7, 13.61) * mm});
            skLineSegment(sketch, "E850", {"start": v(4.7, 13.61) * mm, "end": v(4.3, 13.61) * mm});
            skLineSegment(sketch, "E851", {"start": v(4.3, 13.61) * mm, "end": v(4.02, 13.52) * mm});
            skLineSegment(sketch, "E852", {"start": v(4.02, 13.52) * mm, "end": v(4.02, 13.42) * mm});
            skLineSegment(sketch, "E853", {"start": v(4.02, 13.42) * mm, "end": v(3.73, 13.42) * mm});
            skLineSegment(sketch, "E854", {"start": v(3.73, 13.42) * mm, "end": v(3.73, 13.32) * mm});
            skLineSegment(sketch, "E855", {"start": v(3.73, 13.32) * mm, "end": v(3.44, 13.32) * mm});
            skLineSegment(sketch, "E856", {"start": v(3.44, 13.32) * mm, "end": v(3.24, 13.13) * mm});
            skLineSegment(sketch, "E857", {"start": v(3.24, 13.13) * mm, "end": v(2.95, 13.13) * mm});
            skLineSegment(sketch, "E858", {"start": v(2.95, 13.13) * mm, "end": v(2.76, 13.03) * mm});
            skLineSegment(sketch, "E859", {"start": v(2.76, 13.03) * mm, "end": v(2.76, 12.93) * mm});
            skLineSegment(sketch, "E860", {"start": v(2.76, 12.93) * mm, "end": v(2.57, 12.93) * mm});
            skLineSegment(sketch, "E861", {"start": v(2.57, 12.93) * mm, "end": v(2.57, 12.84) * mm});
            skLineSegment(sketch, "E862", {"start": v(2.57, 12.84) * mm, "end": v(2.37, 12.84) * mm});
            skLineSegment(sketch, "E863", {"start": v(2.37, 12.84) * mm, "end": v(2.37, 12.74) * mm});
            skLineSegment(sketch, "E864", {"start": v(2.37, 12.74) * mm, "end": v(2.18, 12.74) * mm});
            skLineSegment(sketch, "E865", {"start": v(2.18, 12.74) * mm, "end": v(2.18, 12.64) * mm});
            skLineSegment(sketch, "E866", {"start": v(2.18, 12.64) * mm, "end": v(1.99, 12.64) * mm});
            skLineSegment(sketch, "E867", {"start": v(1.99, 12.64) * mm, "end": v(1.8, 12.55) * mm});
            skLineSegment(sketch, "E868", {"start": v(1.8, 12.55) * mm, "end": v(1.7, 12.35) * mm});
            skLineSegment(sketch, "E869", {"start": v(1.7, 12.35) * mm, "end": v(1.3, 12.26) * mm});
            skLineSegment(sketch, "E870", {"start": v(1.3, 12.26) * mm, "end": v(1.21, 12.06) * mm});
            skLineSegment(sketch, "E871", {"start": v(1.21, 12.06) * mm, "end": v(1.02, 12.06) * mm});
            skLineSegment(sketch, "E872", {"start": v(1.02, 12.06) * mm, "end": v(0.92, 11.87) * mm});
            skLineSegment(sketch, "E873", {"start": v(0.92, 11.87) * mm, "end": v(0.73, 11.87) * mm});
            skLineSegment(sketch, "E874", {"start": v(0.73, 11.87) * mm, "end": v(0.53, 11.58) * mm});
            skLineSegment(sketch, "E875", {"start": v(0.53, 11.58) * mm, "end": v(0.34, 11.58) * mm});
            skLineSegment(sketch, "E876", {"start": v(0.34, 11.58) * mm, "end": v(0.15, 11.29) * mm});
            skLineSegment(sketch, "E877", {"start": v(0.15, 11.29) * mm, "end": v(-0.24, 11.38) * mm});
            skLineSegment(sketch, "E878", {"start": v(-0.24, 11.38) * mm, "end": v(-0.44, 11.68) * mm});
            skLineSegment(sketch, "E879", {"start": v(-0.44, 11.68) * mm, "end": v(-0.63, 11.68) * mm});
            skLineSegment(sketch, "E880", {"start": v(-0.63, 11.68) * mm, "end": v(-0.82, 11.97) * mm});
            skLineSegment(sketch, "E881", {"start": v(-0.82, 11.97) * mm, "end": v(-1.02, 11.97) * mm});
            skLineSegment(sketch, "E882", {"start": v(-1.02, 11.97) * mm, "end": v(-1.11, 12.16) * mm});
            skLineSegment(sketch, "E883", {"start": v(-1.11, 12.16) * mm, "end": v(-1.3, 12.16) * mm});
            skLineSegment(sketch, "E884", {"start": v(-1.3, 12.16) * mm, "end": v(-1.4, 12.35) * mm});
            skLineSegment(sketch, "E885", {"start": v(-1.4, 12.35) * mm, "end": v(-1.8, 12.45) * mm});
            skLineSegment(sketch, "E886", {"start": v(-1.8, 12.45) * mm, "end": v(-1.8, 12.55) * mm});
            skLineSegment(sketch, "E887", {"start": v(-1.8, 12.55) * mm, "end": v(-1.99, 12.55) * mm});
            skLineSegment(sketch, "E888", {"start": v(-1.99, 12.55) * mm, "end": v(-1.99, 12.64) * mm});
            skLineSegment(sketch, "E889", {"start": v(-1.99, 12.64) * mm, "end": v(-2.18, 12.64) * mm});
            skLineSegment(sketch, "E890", {"start": v(-2.18, 12.64) * mm, "end": v(-2.18, 12.74) * mm});
            skLineSegment(sketch, "E891", {"start": v(-2.18, 12.74) * mm, "end": v(-2.47, 12.93) * mm});
            skLineSegment(sketch, "E892", {"start": v(-2.47, 12.93) * mm, "end": v(-2.95, 13.03) * mm});
            skLineSegment(sketch, "E893", {"start": v(-2.95, 13.03) * mm, "end": v(-2.95, 13.13) * mm});
            skLineSegment(sketch, "E894", {"start": v(-2.95, 13.13) * mm, "end": v(-3.15, 13.23) * mm});
            skLineSegment(sketch, "E895", {"start": v(-3.15, 13.23) * mm, "end": v(-3.44, 13.32) * mm});
            skLineSegment(sketch, "E896", {"start": v(-3.44, 13.32) * mm, "end": v(-3.73, 13.32) * mm});
            skLineSegment(sketch, "E897", {"start": v(-3.73, 13.32) * mm, "end": v(-3.73, 13.42) * mm});
            skLineSegment(sketch, "E898", {"start": v(-3.73, 13.42) * mm, "end": v(-4.02, 13.42) * mm});
            skLineSegment(sketch, "E899", {"start": v(-4.02, 13.42) * mm, "end": v(-4.02, 13.52) * mm});
            skLineSegment(sketch, "E900", {"start": v(-4.02, 13.52) * mm, "end": v(-4.3, 13.52) * mm});
            skLineSegment(sketch, "E901", {"start": v(-4.3, 13.52) * mm, "end": v(-4.3, 13.61) * mm});
            skLineSegment(sketch, "E902", {"start": v(-4.3, 13.61) * mm, "end": v(-4.7, 13.61) * mm});
            skLineSegment(sketch, "E903", {"start": v(-4.7, 13.61) * mm, "end": v(-4.7, 13.7) * mm});
            skLineSegment(sketch, "E904", {"start": v(-4.7, 13.7) * mm, "end": v(-5.08, 13.7) * mm});
            skLineSegment(sketch, "E905", {"start": v(-5.08, 13.7) * mm, "end": v(-5.08, 13.8) * mm});
            skLineSegment(sketch, "E906", {"start": v(-5.08, 13.8) * mm, "end": v(-5.67, 13.8) * mm});
            skLineSegment(sketch, "E907", {"start": v(-5.67, 13.8) * mm, "end": v(-5.67, 13.9) * mm});
            skLineSegment(sketch, "E908", {"start": v(-5.67, 13.9) * mm, "end": v(-5.96, 13.9) * mm});
            skLineSegment(sketch, "E909", {"start": v(-5.96, 13.9) * mm, "end": v(-6.25, 13.9) * mm});
            skLineSegment(sketch, "E910", {"start": v(-6.25, 13.9) * mm, "end": v(-6.54, 13.9) * mm});
            skLineSegment(sketch, "E911", {"start": v(-6.54, 13.9) * mm, "end": v(-6.54, 14) * mm});
            skLineSegment(sketch, "E912", {"start": v(-6.54, 14) * mm, "end": v(-6.83, 14) * mm});
            skLineSegment(sketch, "E913", {"start": v(-6.83, 14) * mm, "end": v(-7.6, 14) * mm});
            skLineSegment(sketch, "E914", {"start": v(-8.18, 13.52) * mm, "end": v(-8.18, 13.42) * mm});
            skLineSegment(sketch, "E915", {"start": v(-8.18, 13.42) * mm, "end": v(-8.77, 13.42) * mm});
            skLineSegment(sketch, "E916", {"start": v(-8.77, 13.42) * mm, "end": v(-8.77, 13.32) * mm});
            skLineSegment(sketch, "E917", {"start": v(-8.77, 13.32) * mm, "end": v(-9.15, 13.32) * mm});
            skLineSegment(sketch, "E918", {"start": v(-9.15, 13.32) * mm, "end": v(-9.15, 13.23) * mm});
            skLineSegment(sketch, "E919", {"start": v(-9.15, 13.23) * mm, "end": v(-9.54, 13.23) * mm});
            skLineSegment(sketch, "E920", {"start": v(-9.54, 13.23) * mm, "end": v(-9.83, 13.13) * mm});
            skLineSegment(sketch, "E921", {"start": v(-9.83, 13.13) * mm, "end": v(-10.02, 12.93) * mm});
            skLineSegment(sketch, "E922", {"start": v(-10.02, 12.93) * mm, "end": v(-10.31, 12.93) * mm});
            skLineSegment(sketch, "E923", {"start": v(-10.31, 12.93) * mm, "end": v(-10.5, 12.84) * mm});
            skLineSegment(sketch, "E924", {"start": v(-10.5, 12.84) * mm, "end": v(-10.5, 12.74) * mm});
            skLineSegment(sketch, "E925", {"start": v(-10.5, 12.74) * mm, "end": v(-10.7, 12.74) * mm});
            skLineSegment(sketch, "E926", {"start": v(-10.7, 12.74) * mm, "end": v(-10.9, 12.64) * mm});
            skLineSegment(sketch, "E927", {"start": v(-10.9, 12.64) * mm, "end": v(-11, 12.45) * mm});
            skLineSegment(sketch, "E928", {"start": v(-11, 12.45) * mm, "end": v(-11.38, 12.35) * mm});
            skLineSegment(sketch, "E929", {"start": v(-11.38, 12.35) * mm, "end": v(-11.57, 12.06) * mm});
            skLineSegment(sketch, "E930", {"start": v(-11.57, 12.06) * mm, "end": v(-11.77, 12.06) * mm});
            skLineSegment(sketch, "E931", {"start": v(-11.77, 12.06) * mm, "end": v(-11.86, 11.97) * mm});
            skLineSegment(sketch, "E932", {"start": v(-11.86, 11.97) * mm, "end": v(-12.06, 11.77) * mm});
            skLineSegment(sketch, "E933", {"start": v(-12.06, 11.77) * mm, "end": v(-12.06, 11.68) * mm});
            skLineSegment(sketch, "E934", {"start": v(-12.06, 11.68) * mm, "end": v(-12.15, 11.68) * mm});
            skLineSegment(sketch, "E935", {"start": v(-12.15, 11.68) * mm, "end": v(-12.15, 11.58) * mm});
            skLineSegment(sketch, "E936", {"start": v(-12.15, 11.58) * mm, "end": v(-12.25, 11.58) * mm});
            skLineSegment(sketch, "E937", {"start": v(-12.25, 11.58) * mm, "end": v(-12.25, 11.48) * mm});
            skLineSegment(sketch, "E938", {"start": v(-12.25, 11.48) * mm, "end": v(-12.35, 11.48) * mm});
            skLineSegment(sketch, "E939", {"start": v(-12.35, 11.48) * mm, "end": v(-12.35, 11.38) * mm});
            skLineSegment(sketch, "E940", {"start": v(-12.35, 11.38) * mm, "end": v(-12.45, 11.38) * mm});
            skLineSegment(sketch, "E941", {"start": v(-12.45, 11.38) * mm, "end": v(-12.45, 11.29) * mm});
            skLineSegment(sketch, "E942", {"start": v(-12.45, 11.29) * mm, "end": v(-12.54, 11.29) * mm});
            skLineSegment(sketch, "E943", {"start": v(-12.54, 11.29) * mm, "end": v(-12.54, 11.2) * mm});
            skLineSegment(sketch, "E944", {"start": v(-12.54, 11.2) * mm, "end": v(-12.64, 11.2) * mm});
            skLineSegment(sketch, "E945", {"start": v(-12.64, 11.2) * mm, "end": v(-12.64, 11.1) * mm});
            skLineSegment(sketch, "E946", {"start": v(-12.64, 11.1) * mm, "end": v(-12.74, 11.1) * mm});
            skLineSegment(sketch, "E947", {"start": v(-12.74, 11.1) * mm, "end": v(-12.74, 11) * mm});
            skLineSegment(sketch, "E948", {"start": v(-12.74, 11) * mm, "end": v(-12.93, 10.9) * mm});
            skLineSegment(sketch, "E949", {"start": v(-12.93, 10.9) * mm, "end": v(-12.93, 10.7) * mm});
            skLineSegment(sketch, "E950", {"start": v(-12.93, 10.7) * mm, "end": v(-13.22, 10.51) * mm});
            skLineSegment(sketch, "E951", {"start": v(-13.22, 10.51) * mm, "end": v(-13.22, 10.32) * mm});
            skLineSegment(sketch, "E952", {"start": v(-13.22, 10.32) * mm, "end": v(-13.41, 10.22) * mm});
            skLineSegment(sketch, "E953", {"start": v(-13.41, 10.22) * mm, "end": v(-13.51, 9.84) * mm});
            skLineSegment(sketch, "E954", {"start": v(-13.51, 9.84) * mm, "end": v(-13.7, 9.74) * mm});
            skLineSegment(sketch, "E955", {"start": v(-13.7, 9.74) * mm, "end": v(-13.7, 9.54) * mm});
            skLineSegment(sketch, "E956", {"start": v(-13.7, 9.54) * mm, "end": v(-13.8, 9.54) * mm});
            skLineSegment(sketch, "E957", {"start": v(-13.8, 9.54) * mm, "end": v(-13.8, 9.35) * mm});
            skLineSegment(sketch, "E958", {"start": v(-13.8, 9.35) * mm, "end": v(-14, 9.16) * mm});
            skLineSegment(sketch, "E959", {"start": v(-14, 9.16) * mm, "end": v(-14, 8.87) * mm});
            skLineSegment(sketch, "E960", {"start": v(-14, 8.87) * mm, "end": v(-14.19, 8.67) * mm});
            skLineSegment(sketch, "E961", {"start": v(-14.19, 8.67) * mm, "end": v(-14.29, 8.38) * mm});
            skLineSegment(sketch, "E962", {"start": v(-14.29, 8.38) * mm, "end": v(-14.29, 8.1) * mm});
            skLineSegment(sketch, "E963", {"start": v(-14.29, 8.1) * mm, "end": v(-14.38, 8.1) * mm});
            skLineSegment(sketch, "E964", {"start": v(-14.38, 8.1) * mm, "end": v(-14.38, 7.8) * mm});
            skLineSegment(sketch, "E965", {"start": v(-14.38, 7.8) * mm, "end": v(-14.48, 7.8) * mm});
            skLineSegment(sketch, "E966", {"start": v(-14.48, 7.8) * mm, "end": v(-14.48, 7.51) * mm});
            skLineSegment(sketch, "E967", {"start": v(-14.48, 7.51) * mm, "end": v(-14.58, 7.51) * mm});
            skLineSegment(sketch, "E968", {"start": v(-14.58, 7.51) * mm, "end": v(-14.58, 7.03) * mm});
            skLineSegment(sketch, "E969", {"start": v(-14.58, 7.03) * mm, "end": v(-14.67, 7.03) * mm});
            skLineSegment(sketch, "E970", {"start": v(-14.67, 7.03) * mm, "end": v(-14.67, 6.54) * mm});
            skLineSegment(sketch, "E971", {"start": v(-14.67, 6.54) * mm, "end": v(-14.77, 6.54) * mm});
            skLineSegment(sketch, "E972", {"start": v(-14.77, 6.54) * mm, "end": v(-14.77, 5.96) * mm});
            skLineSegment(sketch, "E973", {"start": v(-14.77, 5.96) * mm, "end": v(-14.87, 5.96) * mm});
            skLineSegment(sketch, "E974", {"start": v(-14.87, 5.96) * mm, "end": v(-14.87, 5.67) * mm});
            skLineSegment(sketch, "E975", {"start": v(-14.87, 5.67) * mm, "end": v(-14.87, 5) * mm});
            skLineSegment(sketch, "E976", {"start": v(-14.87, 5) * mm, "end": v(-14.96, 5) * mm});
            skLineSegment(sketch, "E977", {"start": v(-14.96, 5) * mm, "end": v(-14.96, 4.7) * mm});
            skLineSegment(sketch, "E978", {"start": v(-14.96, 4.7) * mm, "end": v(-14.96, 3.83) * mm});
            skLineSegment(sketch, "E979", {"start": v(-14.96, 3.83) * mm, "end": v(-14.87, 3.83) * mm});
            skLineSegment(sketch, "E980", {"start": v(-14.87, 3.83) * mm, "end": v(-14.87, 3.06) * mm});
            skLineSegment(sketch, "E981", {"start": v(-14.87, 3.06) * mm, "end": v(-14.77, 3.06) * mm});
            skLineSegment(sketch, "E982", {"start": v(-14.77, 3.06) * mm, "end": v(-14.77, 3.35) * mm});
            skLineSegment(sketch, "E983", {"start": v(-14.77, 3.35) * mm, "end": v(-14.77, 3.73) * mm});
            skLineSegment(sketch, "E984", {"start": v(-14.77, 3.73) * mm, "end": v(-14.77, 3.83) * mm});
            skLineSegment(sketch, "E985", {"start": v(-14.77, 3.83) * mm, "end": v(-14.77, 3.93) * mm});
            skLineSegment(sketch, "E986", {"start": v(-14.77, 3.93) * mm, "end": v(-14.77, 4.02) * mm});
            skLineSegment(sketch, "E987", {"start": v(-14.77, 4.02) * mm, "end": v(-14.77, 4.12) * mm});
            skLineSegment(sketch, "E988", {"start": v(-14.77, 4.12) * mm, "end": v(-14.77, 4.22) * mm});
            skLineSegment(sketch, "E989", {"start": v(-14.77, 4.22) * mm, "end": v(-14.77, 4.31) * mm});
            skLineSegment(sketch, "E990", {"start": v(-14.77, 4.31) * mm, "end": v(-14.77, 4.41) * mm});
            skLineSegment(sketch, "E991", {"start": v(-14.77, 4.41) * mm, "end": v(-14.77, 5.09) * mm});
            skLineSegment(sketch, "E992", {"start": v(-14.77, 5.09) * mm, "end": v(-14.67, 5.09) * mm});
            skLineSegment(sketch, "E993", {"start": v(-14.67, 5.09) * mm, "end": v(-14.67, 5.67) * mm});
            skLineSegment(sketch, "E994", {"start": v(-14.67, 5.67) * mm, "end": v(-14.58, 5.67) * mm});
            skLineSegment(sketch, "E995", {"start": v(-14.58, 5.67) * mm, "end": v(-14.58, 6.15) * mm});
            skLineSegment(sketch, "E996", {"start": v(-14.58, 6.15) * mm, "end": v(-14.48, 6.15) * mm});
            skLineSegment(sketch, "E997", {"start": v(-14.48, 6.15) * mm, "end": v(-14.48, 6.64) * mm});
            skLineSegment(sketch, "E998", {"start": v(-14.48, 6.64) * mm, "end": v(-14.38, 6.64) * mm});
            skLineSegment(sketch, "E999", {"start": v(-14.38, 6.64) * mm, "end": v(-14.38, 7.03) * mm});
            skLineSegment(sketch, "E1000", {"start": v(-14.38, 7.03) * mm, "end": v(-14.29, 7.32) * mm});
            skLineSegment(sketch, "E1001", {"start": v(-14.29, 7.32) * mm, "end": v(-14.19, 7.32) * mm});
            skLineSegment(sketch, "E1002", {"start": v(-14.19, 7.32) * mm, "end": v(-14.19, 7.6) * mm});
            skLineSegment(sketch, "E1003", {"start": v(-14.19, 7.6) * mm, "end": v(-14.1, 7.6) * mm});
            skLineSegment(sketch, "E1004", {"start": v(-14.1, 7.6) * mm, "end": v(-14.1, 7.9) * mm});
            skLineSegment(sketch, "E1005", {"start": v(-14.1, 7.9) * mm, "end": v(-13.8, 8.58) * mm});
            skLineSegment(sketch, "E1006", {"start": v(-13.8, 8.58) * mm, "end": v(-13.6, 8.67) * mm});
            skLineSegment(sketch, "E1007", {"start": v(-13.6, 8.67) * mm, "end": v(-13.6, 8.96) * mm});
            skLineSegment(sketch, "E1008", {"start": v(-13.6, 8.96) * mm, "end": v(-13.41, 9.06) * mm});
            skLineSegment(sketch, "E1009", {"start": v(-13.41, 9.06) * mm, "end": v(-13.41, 9.35) * mm});
            skLineSegment(sketch, "E1010", {"start": v(-13.41, 9.35) * mm, "end": v(-13.12, 9.54) * mm});
            skLineSegment(sketch, "E1011", {"start": v(-13.12, 9.54) * mm, "end": v(-13.12, 9.74) * mm});
            skLineSegment(sketch, "E1012", {"start": v(-13.12, 9.74) * mm, "end": v(-12.93, 10.03) * mm});
            skLineSegment(sketch, "E1013", {"start": v(-12.93, 10.03) * mm, "end": v(-12.45, 9.93) * mm});
            skLineSegment(sketch, "E1014", {"start": v(-2.95, 10.03) * mm, "end": v(-2.76, 9.84) * mm});
            skLineSegment(sketch, "E1015", {"start": v(-2.76, 9.84) * mm, "end": v(-2.76, 10.22) * mm});
            skLineSegment(sketch, "E1016", {"start": v(-2.76, 10.22) * mm, "end": v(-2.37, 9.84) * mm});
            skLineSegment(sketch, "E1017", {"start": v(-2.37, 9.84) * mm, "end": v(-2.28, 9.84) * mm});
            skLineSegment(sketch, "E1018", {"start": v(-2.28, 9.84) * mm, "end": v(-2.28, 10.13) * mm});
            skLineSegment(sketch, "E1019", {"start": v(-1.99, 9.93) * mm, "end": v(-1.7, 10.32) * mm});
            skLineSegment(sketch, "E1020", {"start": v(-1.7, 10.32) * mm, "end": v(-1.5, 10.32) * mm});
            skLineSegment(sketch, "E1021", {"start": v(-1.5, 10.32) * mm, "end": v(-1.4, 10.13) * mm});
            skLineSegment(sketch, "E1022", {"start": v(-1.4, 10.13) * mm, "end": v(-1.21, 10.13) * mm});
            skLineSegment(sketch, "E1023", {"start": v(-1.21, 10.13) * mm, "end": v(-1.02, 9.93) * mm});
            skLineSegment(sketch, "E1024", {"start": v(-1.02, 9.93) * mm, "end": v(-1.21, 10.32) * mm});
            skLineSegment(sketch, "E1025", {"start": v(-1.21, 10.32) * mm, "end": v(-0.82, 10.03) * mm});
            skLineSegment(sketch, "E1026", {"start": v(-0.82, 10.03) * mm, "end": v(-1.11, 10.61) * mm});
            skLineSegment(sketch, "E1027", {"start": v(-1.11, 10.61) * mm, "end": v(-1.02, 10.61) * mm});
            skLineSegment(sketch, "E1028", {"start": v(-1.02, 10.61) * mm, "end": v(-0.92, 10.32) * mm});
            skLineSegment(sketch, "E1029", {"start": v(12.74, 9.93) * mm, "end": v(13.32, 9.84) * mm});
            skLineSegment(sketch, "E1030", {"start": v(13.32, 9.84) * mm, "end": v(13.32, 10.13) * mm});
            skLineSegment(sketch, "E1031", {"start": v(13.32, 10.13) * mm, "end": v(12.93, 10.03) * mm});
            skLineSegment(sketch, "E1032", {"start": v(12.93, 10.03) * mm, "end": v(12.74, 10.32) * mm});
            skLineSegment(sketch, "E1033", {"start": v(12.74, 10.32) * mm, "end": v(13.12, 10.13) * mm});
            skLineSegment(sketch, "E1034", {"start": v(13.12, 10.13) * mm, "end": v(12.93, 10.51) * mm});
            skLineSegment(sketch, "E1035", {"start": v(12.93, 10.51) * mm, "end": v(12.93, 10.7) * mm});
            skLineSegment(sketch, "E1036", {"start": v(12.93, 10.7) * mm, "end": v(12.83, 10.8) * mm});
            skLineSegment(sketch, "E1037", {"start": v(12.83, 10.8) * mm, "end": v(12.74, 10.8) * mm});
            skLineSegment(sketch, "E1038", {"start": v(12.74, 10.8) * mm, "end": v(12.64, 10.9) * mm});
            skLineSegment(sketch, "E1039", {"start": v(12.64, 10.9) * mm, "end": v(12.64, 11.1) * mm});
            skLineSegment(sketch, "E1040", {"start": v(12.64, 11.1) * mm, "end": v(12.45, 11.1) * mm});
            skLineSegment(sketch, "E1041", {"start": v(12.45, 11.1) * mm, "end": v(12.45, 11.29) * mm});
            skLineSegment(sketch, "E1042", {"start": v(12.45, 11.29) * mm, "end": v(12.35, 11.38) * mm});
            skLineSegment(sketch, "E1043", {"start": v(12.35, 11.38) * mm, "end": v(12.25, 11.48) * mm});
            skLineSegment(sketch, "E1044", {"start": v(12.25, 11.48) * mm, "end": v(12.15, 11.48) * mm});
            skLineSegment(sketch, "E1045", {"start": v(12.15, 11.48) * mm, "end": v(12.15, 11.58) * mm});
            skLineSegment(sketch, "E1046", {"start": v(12.15, 11.58) * mm, "end": v(12.06, 11.58) * mm});
            skLineSegment(sketch, "E1047", {"start": v(12.06, 11.58) * mm, "end": v(11.86, 11.87) * mm});
            skLineSegment(sketch, "E1048", {"start": v(11.86, 11.87) * mm, "end": v(11.67, 11.87) * mm});
            skLineSegment(sketch, "E1049", {"start": v(11.67, 11.87) * mm, "end": v(11.48, 12.16) * mm});
            skLineSegment(sketch, "E1050", {"start": v(11.48, 12.16) * mm, "end": v(11.28, 12.16) * mm});
            skLineSegment(sketch, "E1051", {"start": v(11.28, 12.16) * mm, "end": v(11.19, 12.35) * mm});
            skLineSegment(sketch, "E1052", {"start": v(11.19, 12.35) * mm, "end": v(11, 12.35) * mm});
            skLineSegment(sketch, "E1053", {"start": v(11, 12.35) * mm, "end": v(10.9, 12.55) * mm});
            skLineSegment(sketch, "E1054", {"start": v(10.9, 12.55) * mm, "end": v(10.6, 12.55) * mm});
            skLineSegment(sketch, "E1055", {"start": v(10.6, 12.55) * mm, "end": v(10.5, 12.74) * mm});
            skLineSegment(sketch, "E1056", {"start": v(10.5, 12.74) * mm, "end": v(10.12, 12.93) * mm});
            skLineSegment(sketch, "E1057", {"start": v(10.12, 12.93) * mm, "end": v(9.83, 13.03) * mm});
            skLineSegment(sketch, "E1058", {"start": v(9.83, 13.03) * mm, "end": v(9.54, 13.03) * mm});
            skLineSegment(sketch, "E1059", {"start": v(9.54, 13.03) * mm, "end": v(9.54, 13.13) * mm});
            skLineSegment(sketch, "E1060", {"start": v(9.54, 13.13) * mm, "end": v(9.25, 13.13) * mm});
            skLineSegment(sketch, "E1061", {"start": v(9.25, 13.13) * mm, "end": v(9.25, 13.23) * mm});
            skLineSegment(sketch, "E1062", {"start": v(9.25, 13.23) * mm, "end": v(8.77, 13.23) * mm});
            skLineSegment(sketch, "E1063", {"start": v(8.77, 13.23) * mm, "end": v(8.77, 13.32) * mm});
            skLineSegment(sketch, "E1064", {"start": v(8.77, 13.32) * mm, "end": v(8.38, 13.32) * mm});
            skLineSegment(sketch, "E1065", {"start": v(8.38, 13.32) * mm, "end": v(8.38, 13.42) * mm});
            skLineSegment(sketch, "E1066", {"start": v(8.38, 13.42) * mm, "end": v(8.09, 13.42) * mm});
            skLineSegment(sketch, "E1067", {"start": v(8.09, 13.42) * mm, "end": v(7.7, 13.42) * mm});
            skLineSegment(sketch, "E1068", {"start": v(7.7, 13.42) * mm, "end": v(7.6, 13.42) * mm});
            skLineSegment(sketch, "E1069", {"start": v(7.6, 13.42) * mm, "end": v(7.5, 13.42) * mm});
            skLineSegment(sketch, "E1070", {"start": v(7.5, 13.42) * mm, "end": v(7.4, 13.42) * mm});
            skLineSegment(sketch, "E1071", {"start": v(7.4, 13.42) * mm, "end": v(7.31, 13.42) * mm});
            skLineSegment(sketch, "E1072", {"start": v(7.31, 13.42) * mm, "end": v(7.22, 13.42) * mm});
            skLineSegment(sketch, "E1073", {"start": v(7.22, 13.42) * mm, "end": v(7.12, 13.42) * mm});
            skLineSegment(sketch, "E1074", {"start": v(7.12, 13.42) * mm, "end": v(7.02, 13.42) * mm});
            skLineSegment(sketch, "E1075", {"start": v(7.02, 13.42) * mm, "end": v(6.92, 13.42) * mm});
            skLineSegment(sketch, "E1076", {"start": v(6.92, 13.42) * mm, "end": v(6.83, 13.42) * mm});
            skLineSegment(sketch, "E1077", {"start": v(6.83, 13.42) * mm, "end": v(6.73, 13.42) * mm});
            skLineSegment(sketch, "E1078", {"start": v(6.73, 13.42) * mm, "end": v(6.63, 13.42) * mm});
            skLineSegment(sketch, "E1079", {"start": v(6.63, 13.42) * mm, "end": v(6.54, 13.42) * mm});
            skLineSegment(sketch, "E1080", {"start": v(6.54, 13.42) * mm, "end": v(6.44, 13.42) * mm});
            skLineSegment(sketch, "E1081", {"start": v(6.44, 13.42) * mm, "end": v(6.34, 13.42) * mm});
            skLineSegment(sketch, "E1082", {"start": v(6.34, 13.42) * mm, "end": v(6.25, 13.42) * mm});
            skLineSegment(sketch, "E1083", {"start": v(6.25, 13.42) * mm, "end": v(5.86, 13.42) * mm});
            skLineSegment(sketch, "E1084", {"start": v(5.86, 13.42) * mm, "end": v(5.86, 13.32) * mm});
            skLineSegment(sketch, "E1085", {"start": v(5.86, 13.32) * mm, "end": v(5.28, 13.32) * mm});
            skLineSegment(sketch, "E1086", {"start": v(5.28, 13.32) * mm, "end": v(5.28, 13.23) * mm});
            skLineSegment(sketch, "E1087", {"start": v(5.28, 13.23) * mm, "end": v(4.9, 13.23) * mm});
            skLineSegment(sketch, "E1088", {"start": v(4.9, 13.23) * mm, "end": v(4.9, 13.13) * mm});
            skLineSegment(sketch, "E1089", {"start": v(4.9, 13.13) * mm, "end": v(4.5, 13.13) * mm});
            skLineSegment(sketch, "E1090", {"start": v(4.5, 13.13) * mm, "end": v(4.21, 13.03) * mm});
            skLineSegment(sketch, "E1091", {"start": v(4.21, 13.03) * mm, "end": v(4.21, 12.93) * mm});
            skLineSegment(sketch, "E1092", {"start": v(4.21, 12.93) * mm, "end": v(3.92, 12.93) * mm});
            skLineSegment(sketch, "E1093", {"start": v(3.92, 12.93) * mm, "end": v(3.92, 12.84) * mm});
            skLineSegment(sketch, "E1094", {"start": v(3.92, 12.84) * mm, "end": v(3.63, 12.84) * mm});
            skLineSegment(sketch, "E1095", {"start": v(3.63, 12.84) * mm, "end": v(3.44, 12.64) * mm});
            skLineSegment(sketch, "E1096", {"start": v(3.44, 12.64) * mm, "end": v(3.15, 12.64) * mm});
            skLineSegment(sketch, "E1097", {"start": v(3.15, 12.64) * mm, "end": v(2.95, 12.55) * mm});
            skLineSegment(sketch, "E1098", {"start": v(2.95, 12.55) * mm, "end": v(2.95, 12.45) * mm});
            skLineSegment(sketch, "E1099", {"start": v(2.95, 12.45) * mm, "end": v(2.76, 12.45) * mm});
            skLineSegment(sketch, "E1100", {"start": v(2.76, 12.45) * mm, "end": v(2.76, 12.35) * mm});
            skLineSegment(sketch, "E1101", {"start": v(2.76, 12.35) * mm, "end": v(2.57, 12.35) * mm});
            skLineSegment(sketch, "E1102", {"start": v(2.57, 12.35) * mm, "end": v(2.57, 12.26) * mm});
            skLineSegment(sketch, "E1103", {"start": v(2.57, 12.26) * mm, "end": v(2.37, 12.26) * mm});
            skLineSegment(sketch, "E1104", {"start": v(2.37, 12.26) * mm, "end": v(2.28, 12.06) * mm});
            skLineSegment(sketch, "E1105", {"start": v(2.28, 12.06) * mm, "end": v(1.89, 11.97) * mm});
            skLineSegment(sketch, "E1106", {"start": v(1.89, 11.97) * mm, "end": v(1.8, 11.77) * mm});
            skLineSegment(sketch, "E1107", {"start": v(1.8, 11.77) * mm, "end": v(1.6, 11.77) * mm});
            skLineSegment(sketch, "E1108", {"start": v(1.6, 11.77) * mm, "end": v(1.5, 11.58) * mm});
            skLineSegment(sketch, "E1109", {"start": v(1.5, 11.58) * mm, "end": v(1.3, 11.58) * mm});
            skLineSegment(sketch, "E1110", {"start": v(1.3, 11.58) * mm, "end": v(1.21, 11.38) * mm});
            skLineSegment(sketch, "E1111", {"start": v(1.21, 11.38) * mm, "end": v(1.02, 11.38) * mm});
            skLineSegment(sketch, "E1112", {"start": v(1.02, 11.38) * mm, "end": v(0.63, 10.9) * mm});
            skLineSegment(sketch, "E1113", {"start": v(0.63, 10.9) * mm, "end": v(0.44, 10.9) * mm});
            skLineSegment(sketch, "E1114", {"start": v(0.44, 10.9) * mm, "end": v(0.34, 10.7) * mm});
            skLineSegment(sketch, "E1115", {"start": v(0.34, 10.7) * mm, "end": v(-0.24, 10.7) * mm});
            skLineSegment(sketch, "E1116", {"start": v(-0.24, 10.7) * mm, "end": v(-0.53, 10.9) * mm});
            skLineSegment(sketch, "E1117", {"start": v(-0.53, 10.9) * mm, "end": v(-0.82, 11.29) * mm});
            skLineSegment(sketch, "E1118", {"start": v(-0.82, 11.29) * mm, "end": v(-1.02, 11.29) * mm});
            skLineSegment(sketch, "E1119", {"start": v(-1.02, 11.29) * mm, "end": v(-1.21, 11.58) * mm});
            skLineSegment(sketch, "E1120", {"start": v(-1.21, 11.58) * mm, "end": v(-1.4, 11.58) * mm});
            skLineSegment(sketch, "E1121", {"start": v(-1.4, 11.58) * mm, "end": v(-1.5, 11.77) * mm});
            skLineSegment(sketch, "E1122", {"start": v(-1.5, 11.77) * mm, "end": v(-1.7, 11.77) * mm});
            skLineSegment(sketch, "E1123", {"start": v(-1.7, 11.77) * mm, "end": v(-1.8, 11.97) * mm});
            skLineSegment(sketch, "E1124", {"start": v(-1.8, 11.97) * mm, "end": v(-1.99, 11.97) * mm});
            skLineSegment(sketch, "E1125", {"start": v(-1.99, 11.97) * mm, "end": v(-2.08, 12.16) * mm});
            skLineSegment(sketch, "E1126", {"start": v(-2.08, 12.16) * mm, "end": v(-2.47, 12.26) * mm});
            skLineSegment(sketch, "E1127", {"start": v(-2.47, 12.26) * mm, "end": v(-2.47, 12.35) * mm});
            skLineSegment(sketch, "E1128", {"start": v(-2.47, 12.35) * mm, "end": v(-2.66, 12.35) * mm});
            skLineSegment(sketch, "E1129", {"start": v(-2.66, 12.35) * mm, "end": v(-2.66, 12.45) * mm});
            skLineSegment(sketch, "E1130", {"start": v(-2.66, 12.45) * mm, "end": v(-2.86, 12.45) * mm});
            skLineSegment(sketch, "E1131", {"start": v(-2.86, 12.45) * mm, "end": v(-2.86, 12.55) * mm});
            skLineSegment(sketch, "E1132", {"start": v(-2.86, 12.55) * mm, "end": v(-3.05, 12.55) * mm});
            skLineSegment(sketch, "E1133", {"start": v(-3.05, 12.55) * mm, "end": v(-3.05, 12.64) * mm});
            skLineSegment(sketch, "E1134", {"start": v(-3.05, 12.64) * mm, "end": v(-3.24, 12.74) * mm});
            skLineSegment(sketch, "E1135", {"start": v(-3.24, 12.74) * mm, "end": v(-3.54, 12.74) * mm});
            skLineSegment(sketch, "E1136", {"start": v(-3.54, 12.74) * mm, "end": v(-3.73, 12.93) * mm});
            skLineSegment(sketch, "E1137", {"start": v(-3.73, 12.93) * mm, "end": v(-4.02, 13.03) * mm});
            skLineSegment(sketch, "E1138", {"start": v(-4.02, 13.03) * mm, "end": v(-4.3, 13.03) * mm});
            skLineSegment(sketch, "E1139", {"start": v(-4.3, 13.03) * mm, "end": v(-4.3, 13.13) * mm});
            skLineSegment(sketch, "E1140", {"start": v(-4.3, 13.13) * mm, "end": v(-4.7, 13.13) * mm});
            skLineSegment(sketch, "E1141", {"start": v(-4.7, 13.13) * mm, "end": v(-4.7, 13.23) * mm});
            skLineSegment(sketch, "E1142", {"start": v(-4.7, 13.23) * mm, "end": v(-5.08, 13.23) * mm});
            skLineSegment(sketch, "E1143", {"start": v(-5.08, 13.23) * mm, "end": v(-5.08, 13.32) * mm});
            skLineSegment(sketch, "E1144", {"start": v(-5.08, 13.32) * mm, "end": v(-5.57, 13.32) * mm});
            skLineSegment(sketch, "E1145", {"start": v(-5.57, 13.32) * mm, "end": v(-5.57, 13.42) * mm});
            skLineSegment(sketch, "E1146", {"start": v(-5.57, 13.42) * mm, "end": v(-6.25, 13.42) * mm});
            skLineSegment(sketch, "E1147", {"start": v(-6.25, 13.42) * mm, "end": v(-6.25, 13.52) * mm});
            skLineSegment(sketch, "E1148", {"start": v(-6.25, 13.52) * mm, "end": v(-6.54, 13.52) * mm});
            skLineSegment(sketch, "E1149", {"start": v(-6.54, 13.52) * mm, "end": v(-6.92, 13.52) * mm});
            skLineSegment(sketch, "E1150", {"start": v(-6.92, 13.52) * mm, "end": v(-7.02, 13.52) * mm});
            skLineSegment(sketch, "E1151", {"start": v(-7.02, 13.52) * mm, "end": v(-7.12, 13.52) * mm});
            skLineSegment(sketch, "E1152", {"start": v(-7.12, 13.52) * mm, "end": v(-7.22, 13.52) * mm});
            skLineSegment(sketch, "E1153", {"start": v(-7.22, 13.52) * mm, "end": v(-7.31, 13.52) * mm});
            skLineSegment(sketch, "E1154", {"start": v(-7.31, 13.52) * mm, "end": v(-7.4, 13.52) * mm});
            skLineSegment(sketch, "E1155", {"start": v(-7.4, 13.52) * mm, "end": v(-7.5, 13.52) * mm});
            skLineSegment(sketch, "E1156", {"start": v(-7.5, 13.52) * mm, "end": v(-7.6, 13.52) * mm});
            skLineSegment(sketch, "E1157", {"start": v(-7.6, 13.52) * mm, "end": v(-8.18, 13.52) * mm});
            skLineSegment(sketch, "E1158", {"start": v(-0.63, 10.8) * mm, "end": v(-0.53, 10.7) * mm});
            skLineSegment(sketch, "E1159", {"start": v(-0.53, 10.7) * mm, "end": v(-0.63, 10.8) * mm});
            skLineSegment(sketch, "E1160", {"start": v(0.82, 10.8) * mm, "end": v(0.92, 10.7) * mm});
            skLineSegment(sketch, "E1161", {"start": v(0.92, 10.7) * mm, "end": v(0.82, 10.8) * mm});
            skLineSegment(sketch, "E1162", {"start": v(-2.57, 10.61) * mm, "end": v(-2.47, 10.51) * mm});
            skLineSegment(sketch, "E1163", {"start": v(-2.47, 10.51) * mm, "end": v(-2.57, 10.61) * mm});
            skLineSegment(sketch, "E1164", {"start": v(-2.24, 10.55) * mm, "end": v(-2.21, 10.48) * mm});
            skLineSegment(sketch, "E1165", {"start": v(-2.21, 10.48) * mm, "end": v(-2.24, 10.55) * mm});
            skLineSegment(sketch, "E1166", {"start": v(-0.92, 10.61) * mm, "end": v(-0.92, 10.51) * mm});
            skLineSegment(sketch, "E1167", {"start": v(-0.92, 10.51) * mm, "end": v(-0.82, 10.51) * mm});
            skLineSegment(sketch, "E1168", {"start": v(-0.82, 10.51) * mm, "end": v(-0.73, 10.51) * mm});
            skLineSegment(sketch, "E1169", {"start": v(-0.63, 10.51) * mm, "end": v(-0.63, 10.61) * mm});
            skLineSegment(sketch, "E1170", {"start": v(-0.63, 10.61) * mm, "end": v(-0.73, 10.61) * mm});
            skLineSegment(sketch, "E1171", {"start": v(-0.73, 10.61) * mm, "end": v(-0.92, 10.61) * mm});
            skLineSegment(sketch, "E1172", {"start": v(-0.37, 10.58) * mm, "end": v(-0.3, 10.55) * mm});
            skLineSegment(sketch, "E1173", {"start": v(-0.3, 10.55) * mm, "end": v(-0.37, 10.58) * mm});
            skLineSegment(sketch, "E1174", {"start": v(0.02, 10.58) * mm, "end": v(0.08, 10.55) * mm});
            skLineSegment(sketch, "E1175", {"start": v(0.08, 10.55) * mm, "end": v(0.02, 10.58) * mm});
            skLineSegment(sketch, "E1176", {"start": v(0.34, 10.61) * mm, "end": v(0.44, 10.51) * mm});
            skLineSegment(sketch, "E1177", {"start": v(0.44, 10.51) * mm, "end": v(0.34, 10.61) * mm});
            skLineSegment(sketch, "E1178", {"start": v(0.82, 10.61) * mm, "end": v(0.92, 10.51) * mm});
            skLineSegment(sketch, "E1179", {"start": v(0.92, 10.51) * mm, "end": v(0.82, 10.61) * mm});
            skLineSegment(sketch, "E1180", {"start": v(-1.6, 10.51) * mm, "end": v(-1.5, 10.42) * mm});
            skLineSegment(sketch, "E1181", {"start": v(-1.5, 10.42) * mm, "end": v(-1.6, 10.51) * mm});
            skLineSegment(sketch, "E1182", {"start": v(12.83, 10.51) * mm, "end": v(12.93, 10.42) * mm});
            skLineSegment(sketch, "E1183", {"start": v(12.93, 10.42) * mm, "end": v(12.83, 10.51) * mm});
            skLineSegment(sketch, "E1184", {"start": v(-1.8, 10.42) * mm, "end": v(-1.89, 10.22) * mm});
            skLineSegment(sketch, "E1185", {"start": v(-1.89, 10.22) * mm, "end": v(-1.8, 10.42) * mm});
            skLineSegment(sketch, "E1186", {"start": v(-1.37, 10.35) * mm, "end": v(-1.34, 10.29) * mm});
            skLineSegment(sketch, "E1187", {"start": v(-1.34, 10.29) * mm, "end": v(-1.37, 10.35) * mm});
            skLineSegment(sketch, "E1188", {"start": v(-2.57, 9.84) * mm, "end": v(-2.47, 9.74) * mm});
            skLineSegment(sketch, "E1189", {"start": v(-2.47, 9.74) * mm, "end": v(-2.57, 9.84) * mm});
            skLineSegment(sketch, "E1190", {"start": v(12.93, 9.84) * mm, "end": v(13.03, 9.74) * mm});
            skLineSegment(sketch, "E1191", {"start": v(13.03, 9.74) * mm, "end": v(12.93, 9.84) * mm});
            skLineSegment(sketch, "E1192", {"start": v(13.41, 9.74) * mm, "end": v(13.51, 9.64) * mm});
            skLineSegment(sketch, "E1193", {"start": v(13.51, 9.64) * mm, "end": v(13.41, 9.74) * mm});
            skLineSegment(sketch, "E1194", {"start": v(-12.93, 9.54) * mm, "end": v(-12.83, 9.45) * mm});
            skLineSegment(sketch, "E1195", {"start": v(-12.83, 9.45) * mm, "end": v(-12.93, 9.54) * mm});
            skLineSegment(sketch, "E1196", {"start": v(-2.47, 9.54) * mm, "end": v(-2.37, 9.45) * mm});
            skLineSegment(sketch, "E1197", {"start": v(-2.37, 9.45) * mm, "end": v(-2.47, 9.54) * mm});
            skLineSegment(sketch, "E1198", {"start": v(-1.8, 6.93) * mm, "end": v(-1.8, 6.15) * mm});
            skLineSegment(sketch, "E1199", {"start": v(-1.8, 6.15) * mm, "end": v(-1.89, 6.15) * mm});
            skLineSegment(sketch, "E1200", {"start": v(-1.89, 6.15) * mm, "end": v(-1.89, 5.86) * mm});
            skLineSegment(sketch, "E1201", {"start": v(-1.89, 5.86) * mm, "end": v(-1.89, 5.57) * mm});
            skLineSegment(sketch, "E1202", {"start": v(-1.89, 5.57) * mm, "end": v(-1.89, 5.28) * mm});
            skLineSegment(sketch, "E1203", {"start": v(-1.89, 5.28) * mm, "end": v(-1.99, 5.28) * mm});
            skLineSegment(sketch, "E1204", {"start": v(-1.99, 5.28) * mm, "end": v(-1.99, 5) * mm});
            skLineSegment(sketch, "E1205", {"start": v(-1.99, 5) * mm, "end": v(-1.99, 4.31) * mm});
            skLineSegment(sketch, "E1206", {"start": v(-1.99, 4.31) * mm, "end": v(-2.08, 4.31) * mm});
            skLineSegment(sketch, "E1207", {"start": v(-2.08, 4.31) * mm, "end": v(-2.08, 3.54) * mm});
            skLineSegment(sketch, "E1208", {"start": v(-2.08, 3.54) * mm, "end": v(-2.18, 3.54) * mm});
            skLineSegment(sketch, "E1209", {"start": v(-2.18, 3.54) * mm, "end": v(-2.18, 3.25) * mm});
            skLineSegment(sketch, "E1210", {"start": v(-2.18, 3.25) * mm, "end": v(-2.18, 2.38) * mm});
            skLineSegment(sketch, "E1211", {"start": v(-2.18, 2.38) * mm, "end": v(-2.28, 2.38) * mm});
            skLineSegment(sketch, "E1212", {"start": v(-2.28, 2.38) * mm, "end": v(-2.28, 2.09) * mm});
            skLineSegment(sketch, "E1213", {"start": v(-2.28, 2.09) * mm, "end": v(-2.28, 1.12) * mm});
            skLineSegment(sketch, "E1214", {"start": v(-2.28, 1.12) * mm, "end": v(-2.37, 1.12) * mm});
            skLineSegment(sketch, "E1215", {"start": v(-2.37, 1.12) * mm, "end": v(-2.37, 0.83) * mm});
            skLineSegment(sketch, "E1216", {"start": v(-2.37, 0.83) * mm, "end": v(-2.37, 0.44) * mm});
            skLineSegment(sketch, "E1217", {"start": v(-2.37, 0.44) * mm, "end": v(-2.37, 0.34) * mm});
            skLineSegment(sketch, "E1218", {"start": v(-2.37, 0.34) * mm, "end": v(-2.37, 0.25) * mm});
            skLineSegment(sketch, "E1219", {"start": v(-2.37, 0.25) * mm, "end": v(-2.37, 0.15) * mm});
            skLineSegment(sketch, "E1220", {"start": v(-2.37, 0.15) * mm, "end": v(-2.37, -0.24) * mm});
            skLineSegment(sketch, "E1221", {"start": v(-2.37, -0.24) * mm, "end": v(-2.47, -0.24) * mm});
            skLineSegment(sketch, "E1222", {"start": v(-2.47, -0.24) * mm, "end": v(-2.47, -0.53) * mm});
            skLineSegment(sketch, "E1223", {"start": v(-2.47, -0.53) * mm, "end": v(-2.47, -0.92) * mm});
            skLineSegment(sketch, "E1224", {"start": v(-2.47, -0.92) * mm, "end": v(-2.47, -1.01) * mm});
            skLineSegment(sketch, "E1225", {"start": v(-2.47, -1.01) * mm, "end": v(-2.47, -1.1) * mm});
            skLineSegment(sketch, "E1226", {"start": v(-2.47, -1.1) * mm, "end": v(-2.47, -1.2) * mm});
            skLineSegment(sketch, "E1227", {"start": v(-2.47, -1.2) * mm, "end": v(-2.47, -1.3) * mm});
            skLineSegment(sketch, "E1228", {"start": v(-2.47, -1.3) * mm, "end": v(-2.47, -1.4) * mm});
            skLineSegment(sketch, "E1229", {"start": v(-2.47, -1.4) * mm, "end": v(-2.47, -1.5) * mm});
            skLineSegment(sketch, "E1230", {"start": v(-2.47, -1.5) * mm, "end": v(-2.47, -1.6) * mm});
            skLineSegment(sketch, "E1231", {"start": v(-2.47, -1.6) * mm, "end": v(-2.47, -1.98) * mm});
            skLineSegment(sketch, "E1232", {"start": v(-2.47, -1.98) * mm, "end": v(-2.57, -1.98) * mm});
            skLineSegment(sketch, "E1233", {"start": v(-2.57, -1.98) * mm, "end": v(-2.57, -2.76) * mm});
            skLineSegment(sketch, "E1234", {"start": v(-2.57, -2.76) * mm, "end": v(-2.86, -3.34) * mm});
            skLineSegment(sketch, "E1235", {"start": v(-2.86, -3.34) * mm, "end": v(-3.15, -3.53) * mm});
            skLineSegment(sketch, "E1236", {"start": v(-3.15, -3.53) * mm, "end": v(-3.63, -3.53) * mm});
            skLineSegment(sketch, "E1237", {"start": v(-3.63, -3.53) * mm, "end": v(-3.92, -3.34) * mm});
            skLineSegment(sketch, "E1238", {"start": v(-3.92, -3.34) * mm, "end": v(-4.12, -3.14) * mm});
            skLineSegment(sketch, "E1239", {"start": v(-4.12, -3.14) * mm, "end": v(-4.12, -3.05) * mm});
            skLineSegment(sketch, "E1240", {"start": v(-4.12, -3.05) * mm, "end": v(-4.21, -3.05) * mm});
            skLineSegment(sketch, "E1241", {"start": v(-4.21, -3.05) * mm, "end": v(-4.21, -2.95) * mm});
            skLineSegment(sketch, "E1242", {"start": v(-4.21, -2.95) * mm, "end": v(-4.4, -2.85) * mm});
            skLineSegment(sketch, "E1243", {"start": v(-4.4, -2.85) * mm, "end": v(-4.4, -2.66) * mm});
            skLineSegment(sketch, "E1244", {"start": v(-4.4, -2.66) * mm, "end": v(-4.6, -2.56) * mm});
            skLineSegment(sketch, "E1245", {"start": v(-4.6, -2.56) * mm, "end": v(-4.7, -2.17) * mm});
            skLineSegment(sketch, "E1246", {"start": v(-4.7, -2.17) * mm, "end": v(-4.8, -2.17) * mm});
            skLineSegment(sketch, "E1247", {"start": v(-4.8, -2.17) * mm, "end": v(-4.9, -1.98) * mm});
            skLineSegment(sketch, "E1248", {"start": v(-4.9, -1.98) * mm, "end": v(-4.9, -1.7) * mm});
            skLineSegment(sketch, "E1249", {"start": v(-4.9, -1.7) * mm, "end": v(-5.18, -1.5) * mm});
            skLineSegment(sketch, "E1250", {"start": v(-5.18, -1.5) * mm, "end": v(-5.18, -1.88) * mm});
            skLineSegment(sketch, "E1251", {"start": v(-5.18, -1.88) * mm, "end": v(-5.38, -2.17) * mm});
            skLineSegment(sketch, "E1252", {"start": v(-5.38, -2.17) * mm, "end": v(-5.47, -2.17) * mm});
            skLineSegment(sketch, "E1253", {"start": v(-5.47, -2.17) * mm, "end": v(-5.57, -2.27) * mm});
            skLineSegment(sketch, "E1254", {"start": v(-5.57, -2.27) * mm, "end": v(-5.57, -2.46) * mm});
            skLineSegment(sketch, "E1255", {"start": v(-5.57, -2.46) * mm, "end": v(-5.86, -2.66) * mm});
            skLineSegment(sketch, "E1256", {"start": v(-5.86, -2.66) * mm, "end": v(-6.34, -2.85) * mm});
            skLineSegment(sketch, "E1257", {"start": v(-6.34, -2.85) * mm, "end": v(-6.83, -2.85) * mm});
            skLineSegment(sketch, "E1258", {"start": v(-6.83, -2.85) * mm, "end": v(-6.83, -2.95) * mm});
            skLineSegment(sketch, "E1259", {"start": v(-6.83, -2.95) * mm, "end": v(-7.12, -2.95) * mm});
            skLineSegment(sketch, "E1260", {"start": v(-7.12, -2.95) * mm, "end": v(-7.5, -2.95) * mm});
            skLineSegment(sketch, "E1261", {"start": v(-7.5, -2.95) * mm, "end": v(-7.6, -2.95) * mm});
            skLineSegment(sketch, "E1262", {"start": v(-7.6, -2.95) * mm, "end": v(-7.7, -2.95) * mm});
            skLineSegment(sketch, "E1263", {"start": v(-7.7, -2.95) * mm, "end": v(-7.8, -2.95) * mm});
            skLineSegment(sketch, "E1264", {"start": v(-7.8, -2.95) * mm, "end": v(-7.9, -2.95) * mm});
            skLineSegment(sketch, "E1265", {"start": v(-7.9, -2.95) * mm, "end": v(-8, -2.95) * mm});
            skLineSegment(sketch, "E1266", {"start": v(-8, -2.95) * mm, "end": v(-8.09, -2.95) * mm});
            skLineSegment(sketch, "E1267", {"start": v(-8.09, -2.95) * mm, "end": v(-8.18, -2.95) * mm});
            skLineSegment(sketch, "E1268", {"start": v(-8.18, -2.95) * mm, "end": v(-8.28, -2.95) * mm});
            skLineSegment(sketch, "E1269", {"start": v(-8.28, -2.95) * mm, "end": v(-8.38, -2.95) * mm});
            skLineSegment(sketch, "E1270", {"start": v(-8.38, -2.95) * mm, "end": v(-8.47, -2.95) * mm});
            skLineSegment(sketch, "E1271", {"start": v(-8.47, -2.95) * mm, "end": v(-8.57, -2.95) * mm});
            skLineSegment(sketch, "E1272", {"start": v(-8.57, -2.95) * mm, "end": v(-8.67, -2.95) * mm});
            skLineSegment(sketch, "E1273", {"start": v(-8.67, -2.95) * mm, "end": v(-8.77, -2.95) * mm});
            skLineSegment(sketch, "E1274", {"start": v(-8.77, -2.95) * mm, "end": v(-8.86, -2.95) * mm});
            skLineSegment(sketch, "E1275", {"start": v(-8.86, -2.95) * mm, "end": v(-8.96, -2.95) * mm});
            skLineSegment(sketch, "E1276", {"start": v(-8.96, -2.95) * mm, "end": v(-9.06, -2.95) * mm});
            skLineSegment(sketch, "E1277", {"start": v(-9.06, -2.95) * mm, "end": v(-9.15, -2.95) * mm});
            skLineSegment(sketch, "E1278", {"start": v(-9.15, -2.95) * mm, "end": v(-9.25, -2.95) * mm});
            skLineSegment(sketch, "E1279", {"start": v(-9.25, -2.95) * mm, "end": v(-9.35, -2.95) * mm});
            skLineSegment(sketch, "E1280", {"start": v(-9.35, -2.95) * mm, "end": v(-9.44, -2.95) * mm});
            skLineSegment(sketch, "E1281", {"start": v(-9.44, -2.95) * mm, "end": v(-9.54, -2.95) * mm});
            skLineSegment(sketch, "E1282", {"start": v(-9.54, -2.95) * mm, "end": v(-9.64, -2.95) * mm});
            skLineSegment(sketch, "E1283", {"start": v(-9.64, -2.95) * mm, "end": v(-9.73, -2.95) * mm});
            skLineSegment(sketch, "E1284", {"start": v(-9.73, -2.95) * mm, "end": v(-9.83, -2.95) * mm});
            skLineSegment(sketch, "E1285", {"start": v(-9.83, -2.95) * mm, "end": v(-9.93, -2.95) * mm});
            skLineSegment(sketch, "E1286", {"start": v(-9.93, -2.95) * mm, "end": v(-10.02, -2.95) * mm});
            skLineSegment(sketch, "E1287", {"start": v(-10.02, -2.95) * mm, "end": v(-10.12, -2.95) * mm});
            skLineSegment(sketch, "E1288", {"start": v(-10.12, -2.95) * mm, "end": v(-10.22, -2.95) * mm});
            skLineSegment(sketch, "E1289", {"start": v(-10.22, -2.95) * mm, "end": v(-10.31, -2.95) * mm});
            skLineSegment(sketch, "E1290", {"start": v(-10.31, -2.95) * mm, "end": v(-10.41, -2.95) * mm});
            skLineSegment(sketch, "E1291", {"start": v(-10.41, -2.95) * mm, "end": v(-10.5, -2.95) * mm});
            skLineSegment(sketch, "E1292", {"start": v(-10.5, -2.95) * mm, "end": v(-10.6, -2.95) * mm});
            skLineSegment(sketch, "E1293", {"start": v(-10.6, -2.95) * mm, "end": v(-10.7, -2.95) * mm});
            skLineSegment(sketch, "E1294", {"start": v(-10.7, -2.95) * mm, "end": v(-10.8, -2.95) * mm});
            skLineSegment(sketch, "E1295", {"start": v(-10.8, -2.95) * mm, "end": v(-10.9, -2.95) * mm});
            skLineSegment(sketch, "E1296", {"start": v(-10.9, -2.95) * mm, "end": v(-11.38, -2.95) * mm});
            skLineSegment(sketch, "E1297", {"start": v(-10.8, -3.43) * mm, "end": v(-10.7, -3.53) * mm});
            skLineSegment(sketch, "E1298", {"start": v(-10.7, -3.53) * mm, "end": v(-10.31, -4.01) * mm});
            skLineSegment(sketch, "E1299", {"start": v(-10.31, -4.01) * mm, "end": v(-10.12, -4.01) * mm});
            skLineSegment(sketch, "E1300", {"start": v(-10.12, -4.01) * mm, "end": v(-10.02, -4.11) * mm});
            skLineSegment(sketch, "E1301", {"start": v(-10.02, -4.11) * mm, "end": v(-9.73, -4.5) * mm});
            skLineSegment(sketch, "E1302", {"start": v(-9.73, -4.5) * mm, "end": v(-9.54, -4.5) * mm});
            skLineSegment(sketch, "E1303", {"start": v(-9.54, -4.5) * mm, "end": v(-9.44, -4.6) * mm});
            skLineSegment(sketch, "E1304", {"start": v(-9.44, -4.6) * mm, "end": v(-9.35, -4.79) * mm});
            skLineSegment(sketch, "E1305", {"start": v(-9.35, -4.79) * mm, "end": v(-9.25, -4.89) * mm});
            skLineSegment(sketch, "E1306", {"start": v(-9.25, -4.89) * mm, "end": v(-9.06, -4.89) * mm});
            skLineSegment(sketch, "E1307", {"start": v(-9.06, -4.89) * mm, "end": v(-8.96, -4.98) * mm});
            skLineSegment(sketch, "E1308", {"start": v(-8.96, -4.98) * mm, "end": v(-8.67, -5.37) * mm});
            skLineSegment(sketch, "E1309", {"start": v(-8.67, -5.37) * mm, "end": v(-8.47, -5.37) * mm});
            skLineSegment(sketch, "E1310", {"start": v(-8.47, -5.37) * mm, "end": v(-8.38, -5.47) * mm});
            skLineSegment(sketch, "E1311", {"start": v(-8.38, -5.47) * mm, "end": v(-8.28, -5.66) * mm});
            skLineSegment(sketch, "E1312", {"start": v(-8.28, -5.66) * mm, "end": v(-8.18, -5.76) * mm});
            skLineSegment(sketch, "E1313", {"start": v(-8.18, -5.76) * mm, "end": v(-8, -5.76) * mm});
            skLineSegment(sketch, "E1314", {"start": v(-8, -5.76) * mm, "end": v(-7.9, -5.85) * mm});
            skLineSegment(sketch, "E1315", {"start": v(-7.9, -5.85) * mm, "end": v(-7.6, -6.24) * mm});
            skLineSegment(sketch, "E1316", {"start": v(-7.6, -6.24) * mm, "end": v(-7.4, -6.24) * mm});
            skLineSegment(sketch, "E1317", {"start": v(-7.4, -6.24) * mm, "end": v(-7.31, -6.34) * mm});
            skLineSegment(sketch, "E1318", {"start": v(-7.31, -6.34) * mm, "end": v(-7.02, -6.73) * mm});
            skLineSegment(sketch, "E1319", {"start": v(-7.02, -6.73) * mm, "end": v(-6.83, -6.73) * mm});
            skLineSegment(sketch, "E1320", {"start": v(-6.83, -6.73) * mm, "end": v(-6.73, -6.82) * mm});
            skLineSegment(sketch, "E1321", {"start": v(-6.73, -6.82) * mm, "end": v(-6.44, -7.21) * mm});
            skLineSegment(sketch, "E1322", {"start": v(-6.44, -7.21) * mm, "end": v(-6.25, -7.21) * mm});
            skLineSegment(sketch, "E1323", {"start": v(-6.25, -7.21) * mm, "end": v(-6.15, -7.3) * mm});
            skLineSegment(sketch, "E1324", {"start": v(-6.15, -7.3) * mm, "end": v(-5.96, -7.5) * mm});
            skLineSegment(sketch, "E1325", {"start": v(-5.96, -7.5) * mm, "end": v(-5.96, -7.6) * mm});
            skLineSegment(sketch, "E1326", {"start": v(-5.96, -7.6) * mm, "end": v(-5.86, -7.6) * mm});
            skLineSegment(sketch, "E1327", {"start": v(-5.86, -7.6) * mm, "end": v(-5.86, -7.7) * mm});
            skLineSegment(sketch, "E1328", {"start": v(-5.86, -7.7) * mm, "end": v(-5.67, -7.89) * mm});
            skLineSegment(sketch, "E1329", {"start": v(-5.67, -7.89) * mm, "end": v(-5.47, -7.89) * mm});
            skLineSegment(sketch, "E1330", {"start": v(-5.47, -7.89) * mm, "end": v(-5.38, -7.99) * mm});
            skLineSegment(sketch, "E1331", {"start": v(-5.38, -7.99) * mm, "end": v(-5.18, -8.18) * mm});
            skLineSegment(sketch, "E1332", {"start": v(-5.18, -8.18) * mm, "end": v(-5.18, -8.28) * mm});
            skLineSegment(sketch, "E1333", {"start": v(-5.18, -8.28) * mm, "end": v(-5.08, -8.28) * mm});
            skLineSegment(sketch, "E1334", {"start": v(-5.08, -8.28) * mm, "end": v(-5.08, -8.37) * mm});
            skLineSegment(sketch, "E1335", {"start": v(-5.08, -8.37) * mm, "end": v(-4.8, -8.66) * mm});
            skLineSegment(sketch, "E1336", {"start": v(-4.8, -8.66) * mm, "end": v(-4.6, -8.66) * mm});
            skLineSegment(sketch, "E1337", {"start": v(-4.6, -8.66) * mm, "end": v(-4.5, -8.76) * mm});
            skLineSegment(sketch, "E1338", {"start": v(-4.5, -8.76) * mm, "end": v(-4.3, -8.95) * mm});
            skLineSegment(sketch, "E1339", {"start": v(-4.3, -8.95) * mm, "end": v(-4.3, -9.05) * mm});
            skLineSegment(sketch, "E1340", {"start": v(-4.3, -9.05) * mm, "end": v(-4.21, -9.05) * mm});
            skLineSegment(sketch, "E1341", {"start": v(-4.21, -9.05) * mm, "end": v(-4.21, -9.15) * mm});
            skLineSegment(sketch, "E1342", {"start": v(-4.21, -9.15) * mm, "end": v(-4.12, -9.15) * mm});
            skLineSegment(sketch, "E1343", {"start": v(-4.12, -9.15) * mm, "end": v(-4.12, -9.24) * mm});
            skLineSegment(sketch, "E1344", {"start": v(-4.12, -9.24) * mm, "end": v(-4.02, -9.24) * mm});
            skLineSegment(sketch, "E1345", {"start": v(-4.02, -9.24) * mm, "end": v(-4.02, -9.34) * mm});
            skLineSegment(sketch, "E1346", {"start": v(-4.02, -9.34) * mm, "end": v(-3.92, -9.34) * mm});
            skLineSegment(sketch, "E1347", {"start": v(-3.92, -9.34) * mm, "end": v(-3.92, -9.44) * mm});
            skLineSegment(sketch, "E1348", {"start": v(-3.92, -9.44) * mm, "end": v(-3.83, -9.44) * mm});
            skLineSegment(sketch, "E1349", {"start": v(-3.83, -9.44) * mm, "end": v(-3.83, -9.54) * mm});
            skLineSegment(sketch, "E1350", {"start": v(-3.83, -9.54) * mm, "end": v(-3.73, -9.54) * mm});
            skLineSegment(sketch, "E1351", {"start": v(-3.73, -9.54) * mm, "end": v(-3.73, -9.63) * mm});
            skLineSegment(sketch, "E1352", {"start": v(-3.73, -9.63) * mm, "end": v(-3.63, -9.63) * mm});
            skLineSegment(sketch, "E1353", {"start": v(-3.63, -9.63) * mm, "end": v(-3.63, -9.73) * mm});
            skLineSegment(sketch, "E1354", {"start": v(-3.63, -9.73) * mm, "end": v(-3.34, -10.02) * mm});
            skLineSegment(sketch, "E1355", {"start": v(-3.34, -10.02) * mm, "end": v(-3.15, -10.02) * mm});
            skLineSegment(sketch, "E1356", {"start": v(-3.15, -10.02) * mm, "end": v(-3.05, -10.12) * mm});
            skLineSegment(sketch, "E1357", {"start": v(-3.05, -10.12) * mm, "end": v(-2.86, -10.3) * mm});
            skLineSegment(sketch, "E1358", {"start": v(-2.86, -10.3) * mm, "end": v(-2.86, -10.4) * mm});
            skLineSegment(sketch, "E1359", {"start": v(-2.86, -10.4) * mm, "end": v(-2.76, -10.4) * mm});
            skLineSegment(sketch, "E1360", {"start": v(-2.76, -10.4) * mm, "end": v(-2.76, -10.5) * mm});
            skLineSegment(sketch, "E1361", {"start": v(-2.76, -10.5) * mm, "end": v(-2.66, -10.5) * mm});
            skLineSegment(sketch, "E1362", {"start": v(-2.66, -10.5) * mm, "end": v(-2.66, -10.6) * mm});
            skLineSegment(sketch, "E1363", {"start": v(-2.66, -10.6) * mm, "end": v(-2.57, -10.6) * mm});
            skLineSegment(sketch, "E1364", {"start": v(-2.57, -10.6) * mm, "end": v(-2.57, -10.7) * mm});
            skLineSegment(sketch, "E1365", {"start": v(-2.57, -10.7) * mm, "end": v(-2.47, -10.7) * mm});
            skLineSegment(sketch, "E1366", {"start": v(-2.47, -10.7) * mm, "end": v(-2.47, -10.8) * mm});
            skLineSegment(sketch, "E1367", {"start": v(-2.47, -10.8) * mm, "end": v(-2.37, -10.8) * mm});
            skLineSegment(sketch, "E1368", {"start": v(-2.37, -10.8) * mm, "end": v(-2.37, -10.9) * mm});
            skLineSegment(sketch, "E1369", {"start": v(-2.37, -10.9) * mm, "end": v(-2.28, -10.9) * mm});
            skLineSegment(sketch, "E1370", {"start": v(-2.28, -10.9) * mm, "end": v(-2.28, -10.99) * mm});
            skLineSegment(sketch, "E1371", {"start": v(-2.28, -10.99) * mm, "end": v(-2.18, -10.99) * mm});
            skLineSegment(sketch, "E1372", {"start": v(-2.18, -10.99) * mm, "end": v(-2.18, -11.08) * mm});
            skLineSegment(sketch, "E1373", {"start": v(-2.18, -11.08) * mm, "end": v(-1.99, -11.18) * mm});
            skLineSegment(sketch, "E1374", {"start": v(-1.99, -11.18) * mm, "end": v(-1.89, -11.28) * mm});
            skLineSegment(sketch, "E1375", {"start": v(-1.89, -11.28) * mm, "end": v(-1.89, -11.47) * mm});
            skLineSegment(sketch, "E1376", {"start": v(-1.89, -11.47) * mm, "end": v(-1.6, -11.57) * mm});
            skLineSegment(sketch, "E1377", {"start": v(-1.6, -11.57) * mm, "end": v(-1.6, -11.76) * mm});
            skLineSegment(sketch, "E1378", {"start": v(-1.6, -11.76) * mm, "end": v(-1.3, -11.86) * mm});
            skLineSegment(sketch, "E1379", {"start": v(-1.3, -11.86) * mm, "end": v(-1.21, -12.15) * mm});
            skLineSegment(sketch, "E1380", {"start": v(-1.21, -12.15) * mm, "end": v(-1.02, -12.34) * mm});
            skLineSegment(sketch, "E1381", {"start": v(-1.02, -12.34) * mm, "end": v(-0.92, -12.34) * mm});
            skLineSegment(sketch, "E1382", {"start": v(-0.92, -12.34) * mm, "end": v(-0.92, -12.44) * mm});
            skLineSegment(sketch, "E1383", {"start": v(-0.92, -12.44) * mm, "end": v(-0.82, -12.44) * mm});
            skLineSegment(sketch, "E1384", {"start": v(-0.82, -12.44) * mm, "end": v(-0.82, -12.54) * mm});
            skLineSegment(sketch, "E1385", {"start": v(-0.82, -12.54) * mm, "end": v(-0.73, -12.54) * mm});
            skLineSegment(sketch, "E1386", {"start": v(-0.73, -12.54) * mm, "end": v(-0.73, -12.63) * mm});
            skLineSegment(sketch, "E1387", {"start": v(-0.73, -12.63) * mm, "end": v(-0.63, -12.63) * mm});
            skLineSegment(sketch, "E1388", {"start": v(-0.63, -12.63) * mm, "end": v(-0.63, -12.73) * mm});
            skLineSegment(sketch, "E1389", {"start": v(-0.63, -12.73) * mm, "end": v(-0.53, -12.73) * mm});
            skLineSegment(sketch, "E1390", {"start": v(-0.53, -12.73) * mm, "end": v(-0.53, -12.83) * mm});
            skLineSegment(sketch, "E1391", {"start": v(-0.53, -12.83) * mm, "end": v(-0.44, -12.83) * mm});
            skLineSegment(sketch, "E1392", {"start": v(-0.44, -12.83) * mm, "end": v(-0.05, -13.4) * mm});
            skLineSegment(sketch, "E1393", {"start": v(-0.05, -13.4) * mm, "end": v(0.15, -13.22) * mm});
            skLineSegment(sketch, "E1394", {"start": v(0.15, -13.22) * mm, "end": v(0.24, -13.22) * mm});
            skLineSegment(sketch, "E1395", {"start": v(0.24, -13.22) * mm, "end": v(0.24, -13.12) * mm});
            skLineSegment(sketch, "E1396", {"start": v(0.24, -13.12) * mm, "end": v(0.34, -13.12) * mm});
            skLineSegment(sketch, "E1397", {"start": v(0.34, -13.12) * mm, "end": v(0.34, -13.02) * mm});
            skLineSegment(sketch, "E1398", {"start": v(0.34, -13.02) * mm, "end": v(0.44, -13.02) * mm});
            skLineSegment(sketch, "E1399", {"start": v(0.44, -13.02) * mm, "end": v(0.44, -12.92) * mm});
            skLineSegment(sketch, "E1400", {"start": v(0.44, -12.92) * mm, "end": v(0.53, -12.92) * mm});
            skLineSegment(sketch, "E1401", {"start": v(0.53, -12.92) * mm, "end": v(0.82, -12.63) * mm});
            skLineSegment(sketch, "E1402", {"start": v(0.82, -12.63) * mm, "end": v(0.82, -12.44) * mm});
            skLineSegment(sketch, "E1403", {"start": v(0.82, -12.44) * mm, "end": v(0.92, -12.34) * mm});
            skLineSegment(sketch, "E1404", {"start": v(0.92, -12.34) * mm, "end": v(1.11, -12.15) * mm});
            skLineSegment(sketch, "E1405", {"start": v(1.11, -12.15) * mm, "end": v(1.21, -12.15) * mm});
            skLineSegment(sketch, "E1406", {"start": v(1.21, -12.15) * mm, "end": v(1.21, -12.05) * mm});
            skLineSegment(sketch, "E1407", {"start": v(1.21, -12.05) * mm, "end": v(1.3, -12.05) * mm});
            skLineSegment(sketch, "E1408", {"start": v(1.3, -12.05) * mm, "end": v(1.3, -11.96) * mm});
            skLineSegment(sketch, "E1409", {"start": v(1.3, -11.96) * mm, "end": v(1.4, -11.96) * mm});
            skLineSegment(sketch, "E1410", {"start": v(1.4, -11.96) * mm, "end": v(1.4, -11.86) * mm});
            skLineSegment(sketch, "E1411", {"start": v(1.4, -11.86) * mm, "end": v(1.5, -11.86) * mm});
            skLineSegment(sketch, "E1412", {"start": v(1.5, -11.86) * mm, "end": v(1.5, -11.76) * mm});
            skLineSegment(sketch, "E1413", {"start": v(1.5, -11.76) * mm, "end": v(1.6, -11.76) * mm});
            skLineSegment(sketch, "E1414", {"start": v(1.6, -11.76) * mm, "end": v(1.6, -11.67) * mm});
            skLineSegment(sketch, "E1415", {"start": v(1.6, -11.67) * mm, "end": v(1.7, -11.67) * mm});
            skLineSegment(sketch, "E1416", {"start": v(1.7, -11.67) * mm, "end": v(1.7, -11.57) * mm});
            skLineSegment(sketch, "E1417", {"start": v(1.7, -11.57) * mm, "end": v(1.8, -11.57) * mm});
            skLineSegment(sketch, "E1418", {"start": v(1.8, -11.57) * mm, "end": v(1.8, -11.47) * mm});
            skLineSegment(sketch, "E1419", {"start": v(1.8, -11.47) * mm, "end": v(1.89, -11.47) * mm});
            skLineSegment(sketch, "E1420", {"start": v(1.89, -11.47) * mm, "end": v(1.89, -11.38) * mm});
            skLineSegment(sketch, "E1421", {"start": v(1.89, -11.38) * mm, "end": v(1.99, -11.38) * mm});
            skLineSegment(sketch, "E1422", {"start": v(1.99, -11.38) * mm, "end": v(1.99, -11.28) * mm});
            skLineSegment(sketch, "E1423", {"start": v(1.99, -11.28) * mm, "end": v(2.08, -11.28) * mm});
            skLineSegment(sketch, "E1424", {"start": v(2.08, -11.28) * mm, "end": v(2.08, -11.18) * mm});
            skLineSegment(sketch, "E1425", {"start": v(2.08, -11.18) * mm, "end": v(2.18, -11.18) * mm});
            skLineSegment(sketch, "E1426", {"start": v(2.18, -11.18) * mm, "end": v(2.18, -11.08) * mm});
            skLineSegment(sketch, "E1427", {"start": v(2.18, -11.08) * mm, "end": v(2.28, -11.08) * mm});
            skLineSegment(sketch, "E1428", {"start": v(2.28, -11.08) * mm, "end": v(2.28, -10.99) * mm});
            skLineSegment(sketch, "E1429", {"start": v(2.28, -10.99) * mm, "end": v(2.37, -10.99) * mm});
            skLineSegment(sketch, "E1430", {"start": v(2.37, -10.99) * mm, "end": v(2.37, -10.9) * mm});
            skLineSegment(sketch, "E1431", {"start": v(2.37, -10.9) * mm, "end": v(2.47, -10.9) * mm});
            skLineSegment(sketch, "E1432", {"start": v(2.47, -10.9) * mm, "end": v(2.47, -10.8) * mm});
            skLineSegment(sketch, "E1433", {"start": v(2.47, -10.8) * mm, "end": v(2.57, -10.8) * mm});
            skLineSegment(sketch, "E1434", {"start": v(2.57, -10.8) * mm, "end": v(2.57, -10.7) * mm});
            skLineSegment(sketch, "E1435", {"start": v(2.57, -10.7) * mm, "end": v(2.66, -10.7) * mm});
            skLineSegment(sketch, "E1436", {"start": v(2.66, -10.7) * mm, "end": v(2.66, -10.6) * mm});
            skLineSegment(sketch, "E1437", {"start": v(2.66, -10.6) * mm, "end": v(2.76, -10.6) * mm});
            skLineSegment(sketch, "E1438", {"start": v(2.76, -10.6) * mm, "end": v(2.76, -10.5) * mm});
            skLineSegment(sketch, "E1439", {"start": v(2.76, -10.5) * mm, "end": v(2.86, -10.5) * mm});
            skLineSegment(sketch, "E1440", {"start": v(2.86, -10.5) * mm, "end": v(2.86, -10.4) * mm});
            skLineSegment(sketch, "E1441", {"start": v(2.86, -10.4) * mm, "end": v(2.95, -10.4) * mm});
            skLineSegment(sketch, "E1442", {"start": v(2.95, -10.4) * mm, "end": v(2.95, -10.3) * mm});
            skLineSegment(sketch, "E1443", {"start": v(2.95, -10.3) * mm, "end": v(3.05, -10.3) * mm});
            skLineSegment(sketch, "E1444", {"start": v(3.05, -10.3) * mm, "end": v(3.05, -10.21) * mm});
            skLineSegment(sketch, "E1445", {"start": v(3.05, -10.21) * mm, "end": v(3.15, -10.21) * mm});
            skLineSegment(sketch, "E1446", {"start": v(3.15, -10.21) * mm, "end": v(3.15, -10.12) * mm});
            skLineSegment(sketch, "E1447", {"start": v(3.15, -10.12) * mm, "end": v(3.24, -10.12) * mm});
            skLineSegment(sketch, "E1448", {"start": v(3.24, -10.12) * mm, "end": v(3.24, -10.02) * mm});
            skLineSegment(sketch, "E1449", {"start": v(3.24, -10.02) * mm, "end": v(3.34, -10.02) * mm});
            skLineSegment(sketch, "E1450", {"start": v(3.34, -10.02) * mm, "end": v(3.34, -9.92) * mm});
            skLineSegment(sketch, "E1451", {"start": v(3.34, -9.92) * mm, "end": v(3.44, -9.92) * mm});
            skLineSegment(sketch, "E1452", {"start": v(3.44, -9.92) * mm, "end": v(3.44, -9.83) * mm});
            skLineSegment(sketch, "E1453", {"start": v(3.44, -9.83) * mm, "end": v(3.54, -9.73) * mm});
            skLineSegment(sketch, "E1454", {"start": v(3.54, -9.73) * mm, "end": v(3.73, -9.73) * mm});
            skLineSegment(sketch, "E1455", {"start": v(3.73, -9.73) * mm, "end": v(3.73, -9.54) * mm});
            skLineSegment(sketch, "E1456", {"start": v(3.73, -9.54) * mm, "end": v(3.92, -9.54) * mm});
            skLineSegment(sketch, "E1457", {"start": v(3.92, -9.54) * mm, "end": v(4.02, -9.44) * mm});
            skLineSegment(sketch, "E1458", {"start": v(4.02, -9.44) * mm, "end": v(4.12, -9.34) * mm});
            skLineSegment(sketch, "E1459", {"start": v(4.12, -9.34) * mm, "end": v(4.12, -9.24) * mm});
            skLineSegment(sketch, "E1460", {"start": v(4.12, -9.24) * mm, "end": v(4.21, -9.24) * mm});
            skLineSegment(sketch, "E1461", {"start": v(4.21, -9.24) * mm, "end": v(4.21, -9.15) * mm});
            skLineSegment(sketch, "E1462", {"start": v(4.21, -9.15) * mm, "end": v(4.3, -9.15) * mm});
            skLineSegment(sketch, "E1463", {"start": v(4.3, -9.15) * mm, "end": v(4.3, -9.05) * mm});
            skLineSegment(sketch, "E1464", {"start": v(4.3, -9.05) * mm, "end": v(4.4, -9.05) * mm});
            skLineSegment(sketch, "E1465", {"start": v(4.4, -9.05) * mm, "end": v(4.4, -8.95) * mm});
            skLineSegment(sketch, "E1466", {"start": v(4.4, -8.95) * mm, "end": v(4.5, -8.95) * mm});
            skLineSegment(sketch, "E1467", {"start": v(4.5, -8.95) * mm, "end": v(4.5, -8.86) * mm});
            skLineSegment(sketch, "E1468", {"start": v(4.5, -8.86) * mm, "end": v(4.6, -8.86) * mm});
            skLineSegment(sketch, "E1469", {"start": v(4.6, -8.86) * mm, "end": v(4.6, -8.76) * mm});
            skLineSegment(sketch, "E1470", {"start": v(4.6, -8.76) * mm, "end": v(4.9, -8.47) * mm});
            skLineSegment(sketch, "E1471", {"start": v(4.9, -8.47) * mm, "end": v(5.08, -8.47) * mm});
            skLineSegment(sketch, "E1472", {"start": v(5.08, -8.47) * mm, "end": v(5.18, -8.37) * mm});
            skLineSegment(sketch, "E1473", {"start": v(5.18, -8.37) * mm, "end": v(5.38, -8.18) * mm});
            skLineSegment(sketch, "E1474", {"start": v(5.38, -8.18) * mm, "end": v(5.38, -8.08) * mm});
            skLineSegment(sketch, "E1475", {"start": v(5.38, -8.08) * mm, "end": v(5.47, -8.08) * mm});
            skLineSegment(sketch, "E1476", {"start": v(5.47, -8.08) * mm, "end": v(5.47, -7.99) * mm});
            skLineSegment(sketch, "E1477", {"start": v(5.47, -7.99) * mm, "end": v(5.76, -7.7) * mm});
            skLineSegment(sketch, "E1478", {"start": v(5.76, -7.7) * mm, "end": v(5.96, -7.7) * mm});
            skLineSegment(sketch, "E1479", {"start": v(5.96, -7.7) * mm, "end": v(6.05, -7.6) * mm});
            skLineSegment(sketch, "E1480", {"start": v(6.05, -7.6) * mm, "end": v(6.44, -7.11) * mm});
            skLineSegment(sketch, "E1481", {"start": v(6.44, -7.11) * mm, "end": v(6.63, -7.11) * mm});
            skLineSegment(sketch, "E1482", {"start": v(6.63, -7.11) * mm, "end": v(6.73, -7.02) * mm});
            skLineSegment(sketch, "E1483", {"start": v(6.73, -7.02) * mm, "end": v(6.92, -6.82) * mm});
            skLineSegment(sketch, "E1484", {"start": v(6.92, -6.82) * mm, "end": v(6.92, -6.73) * mm});
            skLineSegment(sketch, "E1485", {"start": v(6.92, -6.73) * mm, "end": v(7.02, -6.73) * mm});
            skLineSegment(sketch, "E1486", {"start": v(7.02, -6.73) * mm, "end": v(7.02, -6.63) * mm});
            skLineSegment(sketch, "E1487", {"start": v(7.02, -6.63) * mm, "end": v(7.22, -6.44) * mm});
            skLineSegment(sketch, "E1488", {"start": v(7.22, -6.44) * mm, "end": v(7.4, -6.44) * mm});
            skLineSegment(sketch, "E1489", {"start": v(7.4, -6.44) * mm, "end": v(7.5, -6.34) * mm});
            skLineSegment(sketch, "E1490", {"start": v(7.5, -6.34) * mm, "end": v(7.8, -5.95) * mm});
            skLineSegment(sketch, "E1491", {"start": v(7.8, -5.95) * mm, "end": v(8, -5.95) * mm});
            skLineSegment(sketch, "E1492", {"start": v(8, -5.95) * mm, "end": v(8.09, -5.85) * mm});
            skLineSegment(sketch, "E1493", {"start": v(8.09, -5.85) * mm, "end": v(8.38, -5.47) * mm});
            skLineSegment(sketch, "E1494", {"start": v(8.38, -5.47) * mm, "end": v(8.57, -5.47) * mm});
            skLineSegment(sketch, "E1495", {"start": v(8.57, -5.47) * mm, "end": v(8.67, -5.37) * mm});
            skLineSegment(sketch, "E1496", {"start": v(8.67, -5.37) * mm, "end": v(8.77, -5.18) * mm});
            skLineSegment(sketch, "E1497", {"start": v(8.77, -5.18) * mm, "end": v(8.86, -5.08) * mm});
            skLineSegment(sketch, "E1498", {"start": v(8.86, -5.08) * mm, "end": v(9.06, -5.08) * mm});
            skLineSegment(sketch, "E1499", {"start": v(9.06, -5.08) * mm, "end": v(9.15, -4.98) * mm});
            skLineSegment(sketch, "E1500", {"start": v(9.15, -4.98) * mm, "end": v(9.44, -4.6) * mm});
            skLineSegment(sketch, "E1501", {"start": v(9.44, -4.6) * mm, "end": v(9.64, -4.6) * mm});
            skLineSegment(sketch, "E1502", {"start": v(9.64, -4.6) * mm, "end": v(9.73, -4.5) * mm});
            skLineSegment(sketch, "E1503", {"start": v(9.73, -4.5) * mm, "end": v(10.02, -4.11) * mm});
            skLineSegment(sketch, "E1504", {"start": v(10.02, -4.11) * mm, "end": v(10.22, -4.11) * mm});
            skLineSegment(sketch, "E1505", {"start": v(10.22, -4.11) * mm, "end": v(10.31, -4.01) * mm});
            skLineSegment(sketch, "E1506", {"start": v(10.31, -4.01) * mm, "end": v(10.7, -3.53) * mm});
            skLineSegment(sketch, "E1507", {"start": v(10.7, -3.53) * mm, "end": v(10.9, -3.53) * mm});
            skLineSegment(sketch, "E1508", {"start": v(10.9, -3.53) * mm, "end": v(11, -3.43) * mm});
            skLineSegment(sketch, "E1509", {"start": v(11.38, -2.95) * mm, "end": v(11, -2.95) * mm});
            skLineSegment(sketch, "E1510", {"start": v(11, -2.95) * mm, "end": v(10.9, -2.95) * mm});
            skLineSegment(sketch, "E1511", {"start": v(10.9, -2.95) * mm, "end": v(10.8, -2.95) * mm});
            skLineSegment(sketch, "E1512", {"start": v(10.8, -2.95) * mm, "end": v(10.7, -2.95) * mm});
            skLineSegment(sketch, "E1513", {"start": v(10.7, -2.95) * mm, "end": v(10.6, -2.95) * mm});
            skLineSegment(sketch, "E1514", {"start": v(10.6, -2.95) * mm, "end": v(10.5, -2.95) * mm});
            skLineSegment(sketch, "E1515", {"start": v(10.5, -2.95) * mm, "end": v(10.41, -2.95) * mm});
            skLineSegment(sketch, "E1516", {"start": v(10.41, -2.95) * mm, "end": v(10.31, -2.95) * mm});
            skLineSegment(sketch, "E1517", {"start": v(10.31, -2.95) * mm, "end": v(10.22, -2.95) * mm});
            skLineSegment(sketch, "E1518", {"start": v(10.22, -2.95) * mm, "end": v(10.12, -2.95) * mm});
            skLineSegment(sketch, "E1519", {"start": v(10.12, -2.95) * mm, "end": v(10.02, -2.95) * mm});
            skLineSegment(sketch, "E1520", {"start": v(10.02, -2.95) * mm, "end": v(9.93, -2.95) * mm});
            skLineSegment(sketch, "E1521", {"start": v(9.93, -2.95) * mm, "end": v(9.83, -2.95) * mm});
            skLineSegment(sketch, "E1522", {"start": v(9.83, -2.95) * mm, "end": v(9.73, -2.95) * mm});
            skLineSegment(sketch, "E1523", {"start": v(9.73, -2.95) * mm, "end": v(9.64, -2.95) * mm});
            skLineSegment(sketch, "E1524", {"start": v(9.64, -2.95) * mm, "end": v(9.54, -2.95) * mm});
            skLineSegment(sketch, "E1525", {"start": v(9.54, -2.95) * mm, "end": v(9.44, -2.95) * mm});
            skLineSegment(sketch, "E1526", {"start": v(9.44, -2.95) * mm, "end": v(9.35, -2.95) * mm});
            skLineSegment(sketch, "E1527", {"start": v(9.35, -2.95) * mm, "end": v(9.25, -2.95) * mm});
            skLineSegment(sketch, "E1528", {"start": v(9.25, -2.95) * mm, "end": v(9.15, -2.95) * mm});
            skLineSegment(sketch, "E1529", {"start": v(9.15, -2.95) * mm, "end": v(8.47, -2.95) * mm});
            skLineSegment(sketch, "E1530", {"start": v(8.47, -2.95) * mm, "end": v(8.18, -2.85) * mm});
            skLineSegment(sketch, "E1531", {"start": v(8.18, -2.85) * mm, "end": v(7.8, -2.66) * mm});
            skLineSegment(sketch, "E1532", {"start": v(7.8, -2.66) * mm, "end": v(7.6, -2.46) * mm});
            skLineSegment(sketch, "E1533", {"start": v(7.6, -2.46) * mm, "end": v(7.6, -2.37) * mm});
            skLineSegment(sketch, "E1534", {"start": v(7.6, -2.37) * mm, "end": v(7.5, -2.37) * mm});
            skLineSegment(sketch, "E1535", {"start": v(7.5, -2.37) * mm, "end": v(7.5, -2.27) * mm});
            skLineSegment(sketch, "E1536", {"start": v(7.5, -2.27) * mm, "end": v(7.12, -1.98) * mm});
            skLineSegment(sketch, "E1537", {"start": v(7.12, -1.98) * mm, "end": v(6.92, -2.46) * mm});
            skLineSegment(sketch, "E1538", {"start": v(6.92, -2.46) * mm, "end": v(6.73, -2.56) * mm});
            skLineSegment(sketch, "E1539", {"start": v(6.73, -2.56) * mm, "end": v(6.73, -2.76) * mm});
            skLineSegment(sketch, "E1540", {"start": v(6.73, -2.76) * mm, "end": v(6.63, -2.76) * mm});
            skLineSegment(sketch, "E1541", {"start": v(6.63, -2.76) * mm, "end": v(6.63, -2.95) * mm});
            skLineSegment(sketch, "E1542", {"start": v(6.63, -2.95) * mm, "end": v(6.54, -3.14) * mm});
            skLineSegment(sketch, "E1543", {"start": v(6.54, -3.14) * mm, "end": v(6.34, -3.24) * mm});
            skLineSegment(sketch, "E1544", {"start": v(6.34, -3.24) * mm, "end": v(6.25, -3.63) * mm});
            skLineSegment(sketch, "E1545", {"start": v(6.25, -3.63) * mm, "end": v(5.67, -4.11) * mm});
            skLineSegment(sketch, "E1546", {"start": v(5.67, -4.11) * mm, "end": v(5.28, -4.11) * mm});
            skLineSegment(sketch, "E1547", {"start": v(5.28, -4.11) * mm, "end": v(4.9, -3.92) * mm});
            skLineSegment(sketch, "E1548", {"start": v(4.9, -3.92) * mm, "end": v(4.7, -3.63) * mm});
            skLineSegment(sketch, "E1549", {"start": v(4.7, -3.63) * mm, "end": v(4.5, -3.24) * mm});
            skLineSegment(sketch, "E1550", {"start": v(4.5, -3.24) * mm, "end": v(4.4, -2.95) * mm});
            skLineSegment(sketch, "E1551", {"start": v(4.4, -2.95) * mm, "end": v(4.4, -2.56) * mm});
            skLineSegment(sketch, "E1552", {"start": v(4.4, -2.56) * mm, "end": v(4.3, -2.56) * mm});
            skLineSegment(sketch, "E1553", {"start": v(4.3, -2.56) * mm, "end": v(4.3, -2.17) * mm});
            skLineSegment(sketch, "E1554", {"start": v(4.3, -2.17) * mm, "end": v(4.21, -2.17) * mm});
            skLineSegment(sketch, "E1555", {"start": v(4.21, -2.17) * mm, "end": v(4.21, -1.79) * mm});
            skLineSegment(sketch, "E1556", {"start": v(4.21, -1.79) * mm, "end": v(4.12, -1.79) * mm});
            skLineSegment(sketch, "E1557", {"start": v(4.12, -1.79) * mm, "end": v(4.12, -1.2) * mm});
            skLineSegment(sketch, "E1558", {"start": v(4.12, -1.2) * mm, "end": v(4.02, -1.2) * mm});
            skLineSegment(sketch, "E1559", {"start": v(4.02, -1.2) * mm, "end": v(4.02, -0.82) * mm});
            skLineSegment(sketch, "E1560", {"start": v(4.02, -0.82) * mm, "end": v(3.92, -0.82) * mm});
            skLineSegment(sketch, "E1561", {"start": v(3.92, -0.82) * mm, "end": v(3.83, -1.1) * mm});
            skLineSegment(sketch, "E1562", {"start": v(3.83, -1.1) * mm, "end": v(3.83, -1.98) * mm});
            skLineSegment(sketch, "E1563", {"start": v(3.83, -1.98) * mm, "end": v(3.73, -1.98) * mm});
            skLineSegment(sketch, "E1564", {"start": v(3.73, -1.98) * mm, "end": v(3.73, -2.37) * mm});
            skLineSegment(sketch, "E1565", {"start": v(3.73, -2.37) * mm, "end": v(3.44, -2.76) * mm});
            skLineSegment(sketch, "E1566", {"start": v(3.44, -2.76) * mm, "end": v(2.86, -2.76) * mm});
            skLineSegment(sketch, "E1567", {"start": v(2.86, -2.76) * mm, "end": v(2.37, -2.46) * mm});
            skLineSegment(sketch, "E1568", {"start": v(2.37, -2.46) * mm, "end": v(2.28, -2.76) * mm});
            skLineSegment(sketch, "E1569", {"start": v(2.28, -2.76) * mm, "end": v(2.28, -3.05) * mm});
            skLineSegment(sketch, "E1570", {"start": v(2.28, -3.05) * mm, "end": v(2.18, -3.05) * mm});
            skLineSegment(sketch, "E1571", {"start": v(2.18, -3.05) * mm, "end": v(2.18, -3.43) * mm});
            skLineSegment(sketch, "E1572", {"start": v(2.18, -3.43) * mm, "end": v(2.08, -3.43) * mm});
            skLineSegment(sketch, "E1573", {"start": v(2.08, -3.43) * mm, "end": v(2.08, -4.01) * mm});
            skLineSegment(sketch, "E1574", {"start": v(2.08, -4.01) * mm, "end": v(1.99, -4.01) * mm});
            skLineSegment(sketch, "E1575", {"start": v(1.99, -4.01) * mm, "end": v(1.99, -4.5) * mm});
            skLineSegment(sketch, "E1576", {"start": v(1.99, -4.5) * mm, "end": v(1.89, -4.5) * mm});
            skLineSegment(sketch, "E1577", {"start": v(1.89, -4.5) * mm, "end": v(1.89, -5.08) * mm});
            skLineSegment(sketch, "E1578", {"start": v(1.89, -5.08) * mm, "end": v(1.8, -5.08) * mm});
            skLineSegment(sketch, "E1579", {"start": v(1.8, -5.08) * mm, "end": v(1.8, -5.66) * mm});
            skLineSegment(sketch, "E1580", {"start": v(1.8, -5.66) * mm, "end": v(1.7, -5.66) * mm});
            skLineSegment(sketch, "E1581", {"start": v(1.7, -5.66) * mm, "end": v(1.7, -6.15) * mm});
            skLineSegment(sketch, "E1582", {"start": v(1.7, -6.15) * mm, "end": v(1.6, -6.15) * mm});
            skLineSegment(sketch, "E1583", {"start": v(1.6, -6.15) * mm, "end": v(1.6, -6.63) * mm});
            skLineSegment(sketch, "E1584", {"start": v(1.6, -6.63) * mm, "end": v(1.5, -6.63) * mm});
            skLineSegment(sketch, "E1585", {"start": v(1.5, -6.63) * mm, "end": v(1.5, -7.11) * mm});
            skLineSegment(sketch, "E1586", {"start": v(1.5, -7.11) * mm, "end": v(1.4, -7.11) * mm});
            skLineSegment(sketch, "E1587", {"start": v(1.4, -7.11) * mm, "end": v(1.4, -7.6) * mm});
            skLineSegment(sketch, "E1588", {"start": v(1.4, -7.6) * mm, "end": v(1.21, -7.89) * mm});
            skLineSegment(sketch, "E1589", {"start": v(1.21, -7.89) * mm, "end": v(1.21, -8.28) * mm});
            skLineSegment(sketch, "E1590", {"start": v(1.21, -8.28) * mm, "end": v(1.11, -8.57) * mm});
            skLineSegment(sketch, "E1591", {"start": v(1.11, -8.57) * mm, "end": v(1.02, -8.57) * mm});
            skLineSegment(sketch, "E1592", {"start": v(1.02, -8.57) * mm, "end": v(1.02, -8.86) * mm});
            skLineSegment(sketch, "E1593", {"start": v(1.02, -8.86) * mm, "end": v(0.82, -9.24) * mm});
            skLineSegment(sketch, "E1594", {"start": v(0.82, -9.24) * mm, "end": v(0.73, -9.34) * mm});
            skLineSegment(sketch, "E1595", {"start": v(0.73, -9.34) * mm, "end": v(0.53, -9.44) * mm});
            skLineSegment(sketch, "E1596", {"start": v(0.53, -9.44) * mm, "end": v(0.15, -9.44) * mm});
            skLineSegment(sketch, "E1597", {"start": v(0.15, -9.44) * mm, "end": v(-0.15, -9.15) * mm});
            skLineSegment(sketch, "E1598", {"start": v(-0.15, -9.15) * mm, "end": v(-0.34, -8.66) * mm});
            skLineSegment(sketch, "E1599", {"start": v(-0.34, -8.66) * mm, "end": v(-0.34, -8.18) * mm});
            skLineSegment(sketch, "E1600", {"start": v(-0.34, -8.18) * mm, "end": v(-0.44, -8.18) * mm});
            skLineSegment(sketch, "E1601", {"start": v(-0.44, -8.18) * mm, "end": v(-0.44, -7.6) * mm});
            skLineSegment(sketch, "E1602", {"start": v(-0.44, -7.6) * mm, "end": v(-0.53, -7.6) * mm});
            skLineSegment(sketch, "E1603", {"start": v(-0.53, -7.6) * mm, "end": v(-0.53, -7.02) * mm});
            skLineSegment(sketch, "E1604", {"start": v(-0.53, -7.02) * mm, "end": v(-0.63, -7.02) * mm});
            skLineSegment(sketch, "E1605", {"start": v(-0.63, -7.02) * mm, "end": v(-0.63, -6.73) * mm});
            skLineSegment(sketch, "E1606", {"start": v(-0.63, -6.73) * mm, "end": v(-0.63, -6.44) * mm});
            skLineSegment(sketch, "E1607", {"start": v(-0.63, -6.44) * mm, "end": v(-0.63, -6.15) * mm});
            skLineSegment(sketch, "E1608", {"start": v(-0.63, -6.15) * mm, "end": v(-0.73, -6.15) * mm});
            skLineSegment(sketch, "E1609", {"start": v(-0.73, -6.15) * mm, "end": v(-0.73, -5.85) * mm});
            skLineSegment(sketch, "E1610", {"start": v(-0.73, -5.85) * mm, "end": v(-0.73, -5.18) * mm});
            skLineSegment(sketch, "E1611", {"start": v(-0.73, -5.18) * mm, "end": v(-0.82, -5.18) * mm});
            skLineSegment(sketch, "E1612", {"start": v(-0.82, -5.18) * mm, "end": v(-0.82, -4.89) * mm});
            skLineSegment(sketch, "E1613", {"start": v(-0.82, -4.89) * mm, "end": v(-0.82, -4.11) * mm});
            skLineSegment(sketch, "E1614", {"start": v(-0.82, -4.11) * mm, "end": v(-0.92, -4.11) * mm});
            skLineSegment(sketch, "E1615", {"start": v(-0.92, -4.11) * mm, "end": v(-0.92, -3.82) * mm});
            skLineSegment(sketch, "E1616", {"start": v(-0.92, -3.82) * mm, "end": v(-0.92, -2.85) * mm});
            skLineSegment(sketch, "E1617", {"start": v(-0.92, -2.85) * mm, "end": v(-1.02, -2.85) * mm});
            skLineSegment(sketch, "E1618", {"start": v(-1.02, -2.85) * mm, "end": v(-1.02, -2.56) * mm});
            skLineSegment(sketch, "E1619", {"start": v(-1.02, -2.56) * mm, "end": v(-1.02, -1.6) * mm});
            skLineSegment(sketch, "E1620", {"start": v(-1.02, -1.6) * mm, "end": v(-1.11, -1.6) * mm});
            skLineSegment(sketch, "E1621", {"start": v(-1.11, -1.6) * mm, "end": v(-1.11, -1.3) * mm});
            skLineSegment(sketch, "E1622", {"start": v(-1.11, -1.3) * mm, "end": v(-1.11, -0.92) * mm});
            skLineSegment(sketch, "E1623", {"start": v(-1.11, -0.92) * mm, "end": v(-1.11, -0.82) * mm});
            skLineSegment(sketch, "E1624", {"start": v(-1.11, -0.82) * mm, "end": v(-1.11, -0.72) * mm});
            skLineSegment(sketch, "E1625", {"start": v(-1.11, -0.72) * mm, "end": v(-1.11, -0.62) * mm});
            skLineSegment(sketch, "E1626", {"start": v(-1.11, -0.62) * mm, "end": v(-1.11, -0.24) * mm});
            skLineSegment(sketch, "E1627", {"start": v(-1.11, -0.24) * mm, "end": v(-1.21, -0.24) * mm});
            skLineSegment(sketch, "E1628", {"start": v(-1.21, -0.24) * mm, "end": v(-1.21, 0.05) * mm});
            skLineSegment(sketch, "E1629", {"start": v(-1.21, 0.05) * mm, "end": v(-1.21, 0.44) * mm});
            skLineSegment(sketch, "E1630", {"start": v(-1.21, 0.44) * mm, "end": v(-1.21, 0.54) * mm});
            skLineSegment(sketch, "E1631", {"start": v(-1.21, 0.54) * mm, "end": v(-1.21, 0.63) * mm});
            skLineSegment(sketch, "E1632", {"start": v(-1.21, 0.63) * mm, "end": v(-1.21, 0.73) * mm});
            skLineSegment(sketch, "E1633", {"start": v(-1.21, 0.73) * mm, "end": v(-1.21, 1.22) * mm});
            skLineSegment(sketch, "E1634", {"start": v(-1.21, 1.22) * mm, "end": v(-1.3, 1.22) * mm});
            skLineSegment(sketch, "E1635", {"start": v(-1.3, 1.22) * mm, "end": v(-1.3, 1.5) * mm});
            skLineSegment(sketch, "E1636", {"start": v(-1.3, 1.5) * mm, "end": v(-1.3, 1.9) * mm});
            skLineSegment(sketch, "E1637", {"start": v(-1.3, 1.9) * mm, "end": v(-1.3, 2) * mm});
            skLineSegment(sketch, "E1638", {"start": v(-1.3, 2) * mm, "end": v(-1.3, 2.09) * mm});
            skLineSegment(sketch, "E1639", {"start": v(-1.3, 2.09) * mm, "end": v(-1.3, 2.18) * mm});
            skLineSegment(sketch, "E1640", {"start": v(-1.3, 2.18) * mm, "end": v(-1.3, 2.77) * mm});
            skLineSegment(sketch, "E1641", {"start": v(-1.3, 2.77) * mm, "end": v(-1.4, 2.77) * mm});
            skLineSegment(sketch, "E1642", {"start": v(-1.4, 2.77) * mm, "end": v(-1.4, 3.06) * mm});
            skLineSegment(sketch, "E1643", {"start": v(-1.4, 3.06) * mm, "end": v(-1.4, 3.44) * mm});
            skLineSegment(sketch, "E1644", {"start": v(-1.4, 3.44) * mm, "end": v(-1.4, 3.54) * mm});
            skLineSegment(sketch, "E1645", {"start": v(-1.4, 3.54) * mm, "end": v(-1.4, 3.64) * mm});
            skLineSegment(sketch, "E1646", {"start": v(-1.4, 3.64) * mm, "end": v(-1.4, 3.73) * mm});
            skLineSegment(sketch, "E1647", {"start": v(-1.4, 3.73) * mm, "end": v(-1.4, 4.22) * mm});
            skLineSegment(sketch, "E1648", {"start": v(-1.4, 4.22) * mm, "end": v(-1.5, 4.22) * mm});
            skLineSegment(sketch, "E1649", {"start": v(-1.5, 4.22) * mm, "end": v(-1.5, 4.5) * mm});
            skLineSegment(sketch, "E1650", {"start": v(-1.5, 4.5) * mm, "end": v(-1.5, 5.38) * mm});
            skLineSegment(sketch, "E1651", {"start": v(-1.5, 5.38) * mm, "end": v(-1.6, 5.38) * mm});
            skLineSegment(sketch, "E1652", {"start": v(-1.6, 5.38) * mm, "end": v(-1.6, 5.67) * mm});
            skLineSegment(sketch, "E1653", {"start": v(-1.6, 5.67) * mm, "end": v(-1.6, 6.54) * mm});
            skLineSegment(sketch, "E1654", {"start": v(-1.6, 6.54) * mm, "end": v(-1.7, 6.54) * mm});
            skLineSegment(sketch, "E1655", {"start": v(-1.7, 6.54) * mm, "end": v(-1.8, 6.93) * mm});
            skLineSegment(sketch, "E1656", {"start": v(-19.7, -2.08) * mm, "end": v(-19.7, -2.95) * mm});
            skLineSegment(sketch, "E1657", {"start": v(20.3, -2.08) * mm, "end": v(20.3, -2.95) * mm});
            skLineSegment(sketch, "E1658", {"start": v(11, -3.43) * mm, "end": v(11.38, -2.95) * mm});
            skLineSegment(sketch, "E1659", {"start": v(-12.06, -2.94) * mm, "end": v(-11.46, -2.95) * mm});
            skLineSegment(sketch, "E1660", {"start": v(-11.38, -2.95) * mm, "end": v(-10.8, -3.43) * mm});
            skLineSegment(sketch, "E1661", {"start": v(-11.46, -2.95) * mm, "end": v(-11.67, -2.66) * mm});
            skSolve(sketch);
        }
        {
            var Q0;
            Q0 = qSketchRegion(id + "F3", true);
            extrude(context, id + "F4", {"entities" : qUnion([Q0]), "operationType" : NewBodyOperationType.ADD, "depth" : 1 * mm, "offsetDistance" : 25 * mm});
        }
        {
            var Q0;
            Q0=makeQuery(id+"F1.opRevolve","SWEPT_EDGE",EDGE,{"disambiguationData":[OSD([sQuery(id+"F0.wireOp",EDGE,"E0.top"),sQuery(id+"F0.wireOp",EDGE,"E0.left")])]});
            fillet(context, id + "F5", {"entities" : qUnion([Q0]), "radius" : 1 * mm, "tangentPropagation" : true, "allowEdgeOverflow" : false});
        }
    });
